FCSTD DOCUMENT  (FreeCAD 0.20R29410 (Git))
Label: PalasFidasFrogExample
License: All rights reserved
LicenseURL: https://en.wikipedia.org/wiki/All_rights_reserved
objects: Part::Feature×547, Part::Box×220, App::Part×142, Part::MultiFuse×119, Part::Cylinder×25, Part::Cut×22, Part::Extrusion×18, Sketcher::SketchObject×17, Part::Fillet×14, Part::FeaturePython×10, Part::Cone×5, Part::Torus×2, Part::Sphere×1, Mesh::Feature×1, Part::Compound×1
note: 1001 computed .brp shape members not serialized (recipe doc carries the construction recipe); baked Part::Feature solids carry a one-line shape summary decoded from their .brp

FEATURE [Sketcher::SketchObject] Sketch
  FullyConstrained = false
  Placement = pos=(0,0,0) rot=(0.57735,-0.57735,-0.57735;2.0944rad)
  sketch-geometry (10):
    g0: LineSegment StartX=-76.5603 StartY=-55.0385 StartZ=0 EndX=-76.5603 EndY=38.9615 EndZ=0
    g1: LineSegment StartX=-76.5603 StartY=-55.0385 StartZ=0 EndX=77.4397 EndY=-55.0385 EndZ=0
    g2: LineSegment StartX=77.4397 StartY=-55.0385 StartZ=0 EndX=77.4397 EndY=1.96148 EndZ=0
    g3: LineSegment StartX=77.4397 StartY=1.96148 StartZ=0 EndX=63.0634 EndY=6.2419 EndZ=0
    g4: LineSegment StartX=63.0634 StartY=6.2419 StartZ=0 EndX=61.4939 EndY=0.970589 EndZ=0
    g5: LineSegment StartX=61.4939 StartY=0.970589 StartZ=0 EndX=48.076 EndY=4.96564 EndZ=0
    g6: LineSegment StartX=48.076 StartY=4.96564 StartZ=0 EndX=40.4859 EndY=2.43786 EndZ=0
    g7: LineSegment StartX=-50.564 StartY=29.5472 StartZ=0 EndX=40.4859 EndY=2.43786 EndZ=0
    g8: LineSegment StartX=-76.5603 StartY=38.9615 StartZ=0 EndX=-58.1062 EndY=33.467 EndZ=0
    g9: LineSegment StartX=-58.1062 StartY=33.467 StartZ=0 EndX=-50.564 EndY=29.5472 EndZ=0
  constraints (27):
    c: Vertical(g0)
    c: Coincident(g1,g0)
    c: Horizontal(g1)
    c: Coincident(g2,g1)
    c: Vertical(g2)
    c: DistanceY(g0,g0) = 94
    c: DistanceX(g1,g1) = 154
    c: DistanceY(g2,g2) = 57
    c: Coincident(g3,g2)
    c: Coincident(g4,g3)
    c: Coincident(g5,g4)
    c: Coincident(g7,g6)
    c: Distance(g4) = 5.5
    c: Distance(g5) = 14
    c: Distance(g3) = 15
    c: Parallel(g7,g3)
    c: Angle(g4,g3) = 1.5708
    c: Parallel(g7,g5)
    c: Distance(g6) = 8
    c: Coincident(g6,g5)
    c: Distance(g7) = 95
    c: Angle(g6,g5) = 2.53073
    c: Coincident(g8,g0)
    c: Coincident(g9,g8)
    c: Coincident(g9,g7)
    c: Parallel(g8,g7)
    c: Distance(g9) = 8.5
FEATURE [Part::Extrusion] Extrude001
  Base = -> Sketch
  Dir = (-1,0,0)
  DirMode = 2
  FaceMakerClass = Part::FaceMakerBullseye
  LengthFwd = 235
  LengthRev = 0
  Placement = pos=(210,0,50) rot=(0,0,1;0rad)
  Solid = true
  Symmetric = false
FEATURE [Part::Extrusion] Extrude
  Base = -> Sketch
  Dir = (-1,0,0)
  DirMode = 2
  FaceMakerClass = Part::FaceMakerBullseye
  LengthFwd = 235
  LengthRev = 0
  Solid = true
  Symmetric = false
FEATURE [Part::Cut] Cut
  Base = -> Extrude
  Tool = -> Extrude001
FEATURE [Part::Cone] Cone
  Angle = 360
  AttacherType = Attacher::AttachEngine3D
  Height = 27
  Placement = pos=(-20,6.5,21) rot=(1,0,0;3.14159rad)
  Radius1 = 0
  Radius2 = 20
FEATURE [Part::Cut] Cut001
  Base = -> Cut
  Tool = -> Cone
FEATURE [Part::Cylinder] Cylinder
  Angle = 360
  AttacherType = Attacher::AttachEngine3D
  FirstAngle = 0
  Height = 2
  Placement = pos=(-20,6.5,-3) rot=(0,0,1;0rad)
  Radius = 10
  SecondAngle = 0
FEATURE [Part::Cylinder] Cylinder001
  Angle = 360
  AttacherType = Attacher::AttachEngine3D
  FirstAngle = 0
  Height = 2
  Placement = pos=(-20,6.5,-5) rot=(0,0,1;0rad)
  Radius = 19.5
  SecondAngle = 0
FEATURE [Part::FeaturePython] Tube  # WARN: FeaturePython — macro-defined, semantics opaque (R4)
  AttacherType = Attacher::AttachEngine3D
  Height = 85
  InnerRadius = 2.5
  OuterRadius = 5
  Placement = pos=(-20,6.5,-3) rot=(0,0,1;0rad)
FEATURE [Sketcher::SketchObject] Sketch001
  FullyConstrained = false
  Placement = pos=(0,0,0) rot=(0.57735,0.57735,0.57735;2.0944rad)
  sketch-geometry (4):
    g0: LineSegment StartX=-44.8885 StartY=-56.9571 StartZ=0 EndX=-44.8885 EndY=-44.9571 EndZ=0
    g1: LineSegment StartX=-44.8885 StartY=-56.9571 StartZ=0 EndX=-26.8885 EndY=-56.9571 EndZ=0
    g2: LineSegment StartX=-26.8885 StartY=-56.9571 StartZ=0 EndX=-26.8885 EndY=-44.9571 EndZ=0
    g3: ArcOfCircle CenterX=-35.8885 CenterY=-44.9571 CenterZ=0 NormalX=0 NormalY=0 NormalZ=1 AngleXU=0 Radius=9 StartAngle=0 EndAngle=3.14159
  constraints (11):
    c: Vertical(g0)
    c: Coincident(g1,g0)
    c: Horizontal(g1)
    c: Coincident(g2,g1)
    c: Vertical(g2)
    c: DistanceY(g0,g0) = 12
    c: DistanceY(g2,g2) = 12
    c: Coincident(g3,g0)
    c: Coincident(g3,g2)
    c: DistanceX(g1,g1) = 18
    c: Angle(g3) = 3.14159
FEATURE [Part::Extrusion] Extrude002  label="inlet"
  Base = -> Sketch001
  Dir = (1,-2e-16,2e-16)
  DirMode = 2
  FaceMakerClass = Part::FaceMakerBullseye
  LengthFwd = 15
  LengthRev = 0
  Placement = pos=(-15,18.5,0) rot=(0,0,1;0rad)
  Solid = true
  Symmetric = false
FEATURE [Part::MultiFuse] Fusion  label="Palas_base"
  Shapes = -> [Cut001,Cylinder,Cylinder001,Tube]
FEATURE [Part::Cut] Cut002
  Base = -> Fusion
  Tool = -> Extrude002
FEATURE [Part::Cylinder] Cylinder002
  Angle = 360
  AttacherType = Attacher::AttachEngine3D
  FirstAngle = 0
  Height = 5
  Placement = pos=(-20,-17.4,-45) rot=(0,1,0;1.5708rad)
  Radius = 9
  SecondAngle = 0
FEATURE [Part::Cut] Cut003  label="Palas_002"
  Base = -> Cut002
  Tool = -> Cylinder002
FEATURE [Part::Cylinder] Cylinder003
  Angle = 360
  AttacherType = Attacher::AttachEngine3D
  FirstAngle = 0
  Height = 15
  Placement = pos=(-35,-17.4,-45) rot=(0,1,0;1.5708rad)
  Radius = 6.5
  SecondAngle = 0
FEATURE [Part::Cut] Cut004
  Base = -> Cut003
  Tool = -> Cylinder003
FEATURE [Part::Feature] Part__Feature  label="USB_Mini_B_SMD_buchse"
  Placement = pos=(1,-56.5,-46.5) rot=(0.57735,0.57735,0.57735;2.0944rad)
  shape: bbox 8.901 x 10 x 3.979 mm, 476 faces (baked)
FEATURE [Part::Box] Box  label="Cube"
  AttacherType = Attacher::AttachEngine3D
  Height = 57
  Length = 5.5
  Placement = pos=(-5,46,-56) rot=(0,0,1;0rad)
  Width = 31.5
FEATURE [Part::MultiFuse] Fusion001  label="Palas003"
  Shapes = -> [Cut004,Part__Feature]
FEATURE [Part::Cut] Cut005  label="Palas"
  Base = -> Fusion001
  Tool = -> Box
FEATURE [Part::Feature] Part__Feature001  label="corps"
  shape: bbox 34 x 13.5 x 21 mm, 889 faces (baked)
FEATURE [Part::Feature] Part__Feature002  label="pin"
  Placement = pos=(-10.5,0,-19) rot=(0,0,1;0rad)
  shape: bbox 0.75 x 9 x 9.5 mm, 29 faces (baked)
FEATURE [Part::Feature] Part__Feature003  label="pin001"
  Placement = pos=(0,0,-19) rot=(0,0,1;0rad)
  shape: bbox 0.75 x 9 x 9.5 mm, 29 faces (baked)
FEATURE [Part::Feature] Part__Feature004  label="pin002"
  Placement = pos=(10.5,0,-19) rot=(0,0,1;0rad)
  shape: bbox 0.75 x 9 x 9.5 mm, 29 faces (baked)
FEATURE [App::Part] Array
  Group = -> [Part__Feature002,Part__Feature003,Part__Feature004]
  Origin = -> Origin001
FEATURE [Part::Feature] Part__Feature005  label="bouton001"
  shape: bbox 22.78 x 10.2 x 12.36 mm, 22 faces (baked)
FEATURE [App::Part] QY603_inter
  Group = -> [Part__Feature001,Array,Part__Feature005]
  Origin = -> Origin002
  Placement = pos=(-6,53,-37) rot=(-0.707107,0,-0.707107;3.14159rad)
FEATURE [Part::Feature] Part__Feature006  label="238-206706"
  shape: bbox 22.46 x 17.88 x 12.7 mm, 94 faces, 0 solids (baked)
FEATURE [Part::Feature] Part__Feature007  label="238-206707"
  shape: bbox 8.001 x 5.836 x 8.001 mm, 28 faces, 0 solids (baked)
FEATURE [Part::Feature] Part__Feature008  label="238-206708"
  shape: bbox 8 x 1.779 x 8 mm, 2 faces, 0 solids (baked)
FEATURE [Part::Feature] Part__Feature009  label="238-206709"
  shape: bbox 2e+100 x 2e+100 x 2e+100 mm, 1 faces, 0 solids (baked)
FEATURE [Part::Feature] Part__Feature010  label="238-206710"
  shape: bbox 8 x 6.139 x 8 mm, 1 faces, 0 solids (baked)
FEATURE [Part::Feature] Part__Feature011  label="238-206711"
  shape: bbox 8 x 1.922 x 8 mm, 1 faces, 0 solids (baked)
FEATURE [Part::Feature] Part__Feature012  label="238-206712"
  shape: bbox 8 x 0.418 x 8 mm, 1 faces, 0 solids (baked)
FEATURE [Part::Feature] Part__Feature013  label="238-206713"
  shape: bbox 0.1933 x 2 x 0.7938 mm, 6 faces, 0 solids (baked)
FEATURE [Part::Feature] Part__Feature014  label="238-206714"
  shape: bbox 0.5393 x 2 x 0.8141 mm, 12 faces, 0 solids (baked)
FEATURE [Part::Feature] Part__Feature015  label="238-206715"
  shape: bbox 0.5393 x 2 x 0.8345 mm, 17 faces, 0 solids (baked)
FEATURE [App::Part] _38_206706  label="dc"
  Group = -> [Part__Feature006,Part__Feature007,Part__Feature008,Part__Feature009,Part__Feature010,Part__Feature011,Part__Feature012,Part__Feature013,Part__Feature014,Part__Feature015]
  Origin = -> Origin003
  Placement = pos=(-7.5,67,-39) rot=(-0.57735,0.57735,-0.57735;4.18879rad)
FEATURE [Part::Box] Box001  label="Cube001"
  AttacherType = Attacher::AttachEngine3D
  Height = 1
  Length = 10
  Placement = pos=(-235,50,-14) rot=(0,0,1;0rad)
  Width = 14
FEATURE [Part::Box] Box002  label="Cube002"
  AttacherType = Attacher::AttachEngine3D
  Height = 1
  Length = 10
  Placement = pos=(-235,35,-14) rot=(0,0,1;0rad)
  Width = 14
FEATURE [Part::Box] Box003  label="Cube003"
  AttacherType = Attacher::AttachEngine3D
  Height = 1
  Length = 10
  Placement = pos=(-235,20,-14) rot=(0,0,1;0rad)
  Width = 14
FEATURE [Part::MultiFuse] Fusion002
  Shapes = -> [Box001,Box002,Box003]
FEATURE [Part::Box] Box004  label="Cube004"
  AttacherType = Attacher::AttachEngine3D
  Height = 1
  Length = 10
  Placement = pos=(-235,50,-14) rot=(0,0,1;0rad)
  Width = 14
FEATURE [Part::Box] Box005  label="Cube005"
  AttacherType = Attacher::AttachEngine3D
  Height = 1
  Length = 10
  Placement = pos=(-235,35,-14) rot=(0,0,1;0rad)
  Width = 14
FEATURE [Part::Box] Box006  label="Cube006"
  AttacherType = Attacher::AttachEngine3D
  Height = 1
  Length = 10
  Placement = pos=(-235,20,-14) rot=(0,0,1;0rad)
  Width = 14
FEATURE [Part::MultiFuse] Fusion003
  Placement = pos=(0,0,-2) rot=(0,0,1;0rad)
  Shapes = -> [Box004,Box005,Box006]
FEATURE [Part::Box] Box007  label="Cube007"
  AttacherType = Attacher::AttachEngine3D
  Height = 1
  Length = 10
  Placement = pos=(-235,50,-14) rot=(0,0,1;0rad)
  Width = 14
FEATURE [Part::Box] Box008  label="Cube008"
  AttacherType = Attacher::AttachEngine3D
  Height = 1
  Length = 10
  Placement = pos=(-235,35,-14) rot=(0,0,1;0rad)
  Width = 14
FEATURE [Part::Box] Box009  label="Cube009"
  AttacherType = Attacher::AttachEngine3D
  Height = 1
  Length = 10
  Placement = pos=(-235,20,-14) rot=(0,0,1;0rad)
  Width = 14
FEATURE [Part::MultiFuse] Fusion004
  Placement = pos=(0,0,-4) rot=(0,0,1;0rad)
  Shapes = -> [Box007,Box008,Box009]
FEATURE [Part::Box] Box010  label="Cube010"
  AttacherType = Attacher::AttachEngine3D
  Height = 1
  Length = 10
  Placement = pos=(-235,50,-14) rot=(0,0,1;0rad)
  Width = 14
FEATURE [Part::Box] Box011  label="Cube011"
  AttacherType = Attacher::AttachEngine3D
  Height = 1
  Length = 10
  Placement = pos=(-235,35,-14) rot=(0,0,1;0rad)
  Width = 14
FEATURE [Part::Box] Box012  label="Cube012"
  AttacherType = Attacher::AttachEngine3D
  Height = 1
  Length = 10
  Placement = pos=(-235,20,-14) rot=(0,0,1;0rad)
  Width = 14
FEATURE [Part::MultiFuse] Fusion005
  Placement = pos=(0,0,-6) rot=(0,0,1;0rad)
  Shapes = -> [Box010,Box011,Box012]
FEATURE [Part::Box] Box013  label="Cube013"
  AttacherType = Attacher::AttachEngine3D
  Height = 1
  Length = 10
  Placement = pos=(-235,50,-14) rot=(0,0,1;0rad)
  Width = 14
FEATURE [Part::Box] Box014  label="Cube014"
  AttacherType = Attacher::AttachEngine3D
  Height = 1
  Length = 10
  Placement = pos=(-235,35,-14) rot=(0,0,1;0rad)
  Width = 14
FEATURE [Part::Box] Box015  label="Cube015"
  AttacherType = Attacher::AttachEngine3D
  Height = 1
  Length = 10
  Placement = pos=(-235,20,-14) rot=(0,0,1;0rad)
  Width = 14
FEATURE [Part::MultiFuse] Fusion006
  Placement = pos=(0,0,-8) rot=(0,0,1;0rad)
  Shapes = -> [Box013,Box014,Box015]
FEATURE [Part::Box] Box016  label="Cube016"
  AttacherType = Attacher::AttachEngine3D
  Height = 1
  Length = 10
  Placement = pos=(-235,50,-14) rot=(0,0,1;0rad)
  Width = 14
FEATURE [Part::Box] Box017  label="Cube017"
  AttacherType = Attacher::AttachEngine3D
  Height = 1
  Length = 10
  Placement = pos=(-235,35,-14) rot=(0,0,1;0rad)
  Width = 14
FEATURE [Part::Box] Box018  label="Cube018"
  AttacherType = Attacher::AttachEngine3D
  Height = 1
  Length = 10
  Placement = pos=(-235,20,-14) rot=(0,0,1;0rad)
  Width = 14
FEATURE [Part::MultiFuse] Fusion007
  Placement = pos=(0,0,-10) rot=(0,0,1;0rad)
  Shapes = -> [Box016,Box017,Box018]
FEATURE [Part::Box] Box019  label="Cube019"
  AttacherType = Attacher::AttachEngine3D
  Height = 1
  Length = 10
  Placement = pos=(-235,50,-14) rot=(0,0,1;0rad)
  Width = 14
FEATURE [Part::Box] Box020  label="Cube020"
  AttacherType = Attacher::AttachEngine3D
  Height = 1
  Length = 10
  Placement = pos=(-235,35,-14) rot=(0,0,1;0rad)
  Width = 14
FEATURE [Part::Box] Box021  label="Cube021"
  AttacherType = Attacher::AttachEngine3D
  Height = 1
  Length = 10
  Placement = pos=(-235,20,-14) rot=(0,0,1;0rad)
  Width = 14
FEATURE [Part::MultiFuse] Fusion008
  Placement = pos=(0,0,-12) rot=(0,0,1;0rad)
  Shapes = -> [Box019,Box020,Box021]
FEATURE [Part::Box] Box022  label="Cube022"
  AttacherType = Attacher::AttachEngine3D
  Height = 1
  Length = 10
  Placement = pos=(-235,50,-14) rot=(0,0,1;0rad)
  Width = 14
FEATURE [Part::Box] Box023  label="Cube023"
  AttacherType = Attacher::AttachEngine3D
  Height = 1
  Length = 10
  Placement = pos=(-235,35,-14) rot=(0,0,1;0rad)
  Width = 14
FEATURE [Part::Box] Box024  label="Cube024"
  AttacherType = Attacher::AttachEngine3D
  Height = 1
  Length = 10
  Placement = pos=(-235,20,-14) rot=(0,0,1;0rad)
  Width = 14
FEATURE [Part::MultiFuse] Fusion009
  Placement = pos=(0,0,-14) rot=(0,0,1;0rad)
  Shapes = -> [Box022,Box023,Box024]
FEATURE [Part::Box] Box025  label="Cube025"
  AttacherType = Attacher::AttachEngine3D
  Height = 1
  Length = 10
  Placement = pos=(-235,50,-14) rot=(0,0,1;0rad)
  Width = 14
FEATURE [Part::Box] Box026  label="Cube026"
  AttacherType = Attacher::AttachEngine3D
  Height = 1
  Length = 10
  Placement = pos=(-235,35,-14) rot=(0,0,1;0rad)
  Width = 14
FEATURE [Part::Box] Box027  label="Cube027"
  AttacherType = Attacher::AttachEngine3D
  Height = 1
  Length = 10
  Placement = pos=(-235,20,-14) rot=(0,0,1;0rad)
  Width = 14
FEATURE [Part::MultiFuse] Fusion010
  Placement = pos=(0,0,-16) rot=(0,0,1;0rad)
  Shapes = -> [Box025,Box026,Box027]
FEATURE [Part::Box] Box028  label="Cube028"
  AttacherType = Attacher::AttachEngine3D
  Height = 1
  Length = 10
  Placement = pos=(-235,50,-14) rot=(0,0,1;0rad)
  Width = 14
FEATURE [Part::Box] Box029  label="Cube029"
  AttacherType = Attacher::AttachEngine3D
  Height = 1
  Length = 10
  Placement = pos=(-235,35,-14) rot=(0,0,1;0rad)
  Width = 14
FEATURE [Part::Box] Box030  label="Cube030"
  AttacherType = Attacher::AttachEngine3D
  Height = 1
  Length = 10
  Placement = pos=(-235,20,-14) rot=(0,0,1;0rad)
  Width = 14
FEATURE [Part::MultiFuse] Fusion011
  Placement = pos=(0,0,-18) rot=(0,0,1;0rad)
  Shapes = -> [Box028,Box029,Box030]
FEATURE [Part::MultiFuse] Fusion012
  Shapes = -> [Fusion002,Fusion003,Fusion004,Fusion005,Fusion006,Fusion007,Fusion008,Fusion009,Fusion010,Fusion011]
FEATURE [Part::Box] Box031  label="Cube031"
  AttacherType = Attacher::AttachEngine3D
  Height = 1
  Length = 10
  Placement = pos=(-235,50,-14) rot=(0,0,1;0rad)
  Width = 14
FEATURE [Part::Box] Box032  label="Cube032"
  AttacherType = Attacher::AttachEngine3D
  Height = 1
  Length = 10
  Placement = pos=(-235,35,-14) rot=(0,0,1;0rad)
  Width = 14
FEATURE [Part::Box] Box033  label="Cube033"
  AttacherType = Attacher::AttachEngine3D
  Height = 1
  Length = 10
  Placement = pos=(-235,20,-14) rot=(0,0,1;0rad)
  Width = 14
FEATURE [Part::Box] Box034  label="Cube034"
  AttacherType = Attacher::AttachEngine3D
  Height = 1
  Length = 10
  Placement = pos=(-235,50,-14) rot=(0,0,1;0rad)
  Width = 14
FEATURE [Part::Box] Box035  label="Cube035"
  AttacherType = Attacher::AttachEngine3D
  Height = 1
  Length = 10
  Placement = pos=(-235,35,-14) rot=(0,0,1;0rad)
  Width = 14
FEATURE [Part::Box] Box036  label="Cube036"
  AttacherType = Attacher::AttachEngine3D
  Height = 1
  Length = 10
  Placement = pos=(-235,20,-14) rot=(0,0,1;0rad)
  Width = 14
FEATURE [Part::Box] Box037  label="Cube037"
  AttacherType = Attacher::AttachEngine3D
  Height = 1
  Length = 10
  Placement = pos=(-235,50,-14) rot=(0,0,1;0rad)
  Width = 14
FEATURE [Part::Box] Box038  label="Cube038"
  AttacherType = Attacher::AttachEngine3D
  Height = 1
  Length = 10
  Placement = pos=(-235,35,-14) rot=(0,0,1;0rad)
  Width = 14
FEATURE [Part::Box] Box039  label="Cube039"
  AttacherType = Attacher::AttachEngine3D
  Height = 1
  Length = 10
  Placement = pos=(-235,20,-14) rot=(0,0,1;0rad)
  Width = 14
FEATURE [Part::Box] Box040  label="Cube040"
  AttacherType = Attacher::AttachEngine3D
  Height = 1
  Length = 10
  Placement = pos=(-235,50,-14) rot=(0,0,1;0rad)
  Width = 14
FEATURE [Part::Box] Box041  label="Cube041"
  AttacherType = Attacher::AttachEngine3D
  Height = 1
  Length = 10
  Placement = pos=(-235,35,-14) rot=(0,0,1;0rad)
  Width = 14
FEATURE [Part::Box] Box042  label="Cube042"
  AttacherType = Attacher::AttachEngine3D
  Height = 1
  Length = 10
  Placement = pos=(-235,20,-14) rot=(0,0,1;0rad)
  Width = 14
FEATURE [Part::Box] Box043  label="Cube043"
  AttacherType = Attacher::AttachEngine3D
  Height = 1
  Length = 10
  Placement = pos=(-235,50,-14) rot=(0,0,1;0rad)
  Width = 14
FEATURE [Part::Box] Box044  label="Cube044"
  AttacherType = Attacher::AttachEngine3D
  Height = 1
  Length = 10
  Placement = pos=(-235,35,-14) rot=(0,0,1;0rad)
  Width = 14
FEATURE [Part::Box] Box045  label="Cube045"
  AttacherType = Attacher::AttachEngine3D
  Height = 1
  Length = 10
  Placement = pos=(-235,20,-14) rot=(0,0,1;0rad)
  Width = 14
FEATURE [Part::Box] Box046  label="Cube046"
  AttacherType = Attacher::AttachEngine3D
  Height = 1
  Length = 10
  Placement = pos=(-235,50,-14) rot=(0,0,1;0rad)
  Width = 14
FEATURE [Part::Box] Box047  label="Cube047"
  AttacherType = Attacher::AttachEngine3D
  Height = 1
  Length = 10
  Placement = pos=(-235,35,-14) rot=(0,0,1;0rad)
  Width = 14
FEATURE [Part::Box] Box048  label="Cube048"
  AttacherType = Attacher::AttachEngine3D
  Height = 1
  Length = 10
  Placement = pos=(-235,20,-14) rot=(0,0,1;0rad)
  Width = 14
FEATURE [Part::Box] Box049  label="Cube049"
  AttacherType = Attacher::AttachEngine3D
  Height = 1
  Length = 10
  Placement = pos=(-235,50,-14) rot=(0,0,1;0rad)
  Width = 14
FEATURE [Part::Box] Box050  label="Cube050"
  AttacherType = Attacher::AttachEngine3D
  Height = 1
  Length = 10
  Placement = pos=(-235,35,-14) rot=(0,0,1;0rad)
  Width = 14
FEATURE [Part::Box] Box051  label="Cube051"
  AttacherType = Attacher::AttachEngine3D
  Height = 1
  Length = 10
  Placement = pos=(-235,20,-14) rot=(0,0,1;0rad)
  Width = 14
FEATURE [Part::Box] Box052  label="Cube052"
  AttacherType = Attacher::AttachEngine3D
  Height = 1
  Length = 10
  Placement = pos=(-235,50,-14) rot=(0,0,1;0rad)
  Width = 14
FEATURE [Part::Box] Box053  label="Cube053"
  AttacherType = Attacher::AttachEngine3D
  Height = 1
  Length = 10
  Placement = pos=(-235,35,-14) rot=(0,0,1;0rad)
  Width = 14
FEATURE [Part::Box] Box054  label="Cube054"
  AttacherType = Attacher::AttachEngine3D
  Height = 1
  Length = 10
  Placement = pos=(-235,20,-14) rot=(0,0,1;0rad)
  Width = 14
FEATURE [Part::Box] Box055  label="Cube055"
  AttacherType = Attacher::AttachEngine3D
  Height = 1
  Length = 10
  Placement = pos=(-235,50,-14) rot=(0,0,1;0rad)
  Width = 14
FEATURE [Part::Box] Box056  label="Cube056"
  AttacherType = Attacher::AttachEngine3D
  Height = 1
  Length = 10
  Placement = pos=(-235,35,-14) rot=(0,0,1;0rad)
  Width = 14
FEATURE [Part::Box] Box057  label="Cube057"
  AttacherType = Attacher::AttachEngine3D
  Height = 1
  Length = 10
  Placement = pos=(-235,20,-14) rot=(0,0,1;0rad)
  Width = 14
FEATURE [Part::Box] Box058  label="Cube058"
  AttacherType = Attacher::AttachEngine3D
  Height = 1
  Length = 10
  Placement = pos=(-235,50,-14) rot=(0,0,1;0rad)
  Width = 14
FEATURE [Part::Box] Box059  label="Cube059"
  AttacherType = Attacher::AttachEngine3D
  Height = 1
  Length = 10
  Placement = pos=(-235,35,-14) rot=(0,0,1;0rad)
  Width = 14
FEATURE [Part::Box] Box060  label="Cube060"
  AttacherType = Attacher::AttachEngine3D
  Height = 1
  Length = 10
  Placement = pos=(-235,20,-14) rot=(0,0,1;0rad)
  Width = 14
FEATURE [Part::MultiFuse] Fusion013
  Shapes = -> [Box031,Box032,Box033]
FEATURE [Part::MultiFuse] Fusion014
  Placement = pos=(0,0,-2) rot=(0,0,1;0rad)
  Shapes = -> [Box034,Box035,Box036]
FEATURE [Part::MultiFuse] Fusion015
  Placement = pos=(0,0,-4) rot=(0,0,1;0rad)
  Shapes = -> [Box037,Box038,Box039]
FEATURE [Part::MultiFuse] Fusion016
  Placement = pos=(0,0,-6) rot=(0,0,1;0rad)
  Shapes = -> [Box040,Box041,Box042]
FEATURE [Part::MultiFuse] Fusion017
  Placement = pos=(0,0,-8) rot=(0,0,1;0rad)
  Shapes = -> [Box043,Box044,Box045]
FEATURE [Part::MultiFuse] Fusion018
  Placement = pos=(0,0,-10) rot=(0,0,1;0rad)
  Shapes = -> [Box046,Box047,Box048]
FEATURE [Part::MultiFuse] Fusion019
  Placement = pos=(0,0,-12) rot=(0,0,1;0rad)
  Shapes = -> [Box049,Box050,Box051]
FEATURE [Part::MultiFuse] Fusion020
  Placement = pos=(0,0,-14) rot=(0,0,1;0rad)
  Shapes = -> [Box052,Box053,Box054]
FEATURE [Part::MultiFuse] Fusion021
  Placement = pos=(0,0,-16) rot=(0,0,1;0rad)
  Shapes = -> [Box055,Box056,Box057]
FEATURE [Part::MultiFuse] Fusion022
  Placement = pos=(0,0,-18) rot=(0,0,1;0rad)
  Shapes = -> [Box058,Box059,Box060]
FEATURE [Part::MultiFuse] Fusion023
  Placement = pos=(0,0,-20) rot=(0,0,1;0rad)
  Shapes = -> [Fusion013,Fusion014,Fusion015,Fusion016,Fusion017,Fusion018,Fusion019,Fusion020,Fusion021,Fusion022]
FEATURE [Part::MultiFuse] Fusion024
  Shapes = -> [Fusion012,Fusion023]
FEATURE [Part::Cut] Cut006
  Base = -> Cut005
  Tool = -> Fusion024
FEATURE [Part::Box] Box062  label="Cube062"
  AttacherType = Attacher::AttachEngine3D
  Height = 1
  Length = 10
  Placement = pos=(-235,35,-14) rot=(0,0,1;0rad)
  Width = 14
FEATURE [Part::Box] Box065  label="Cube065"
  AttacherType = Attacher::AttachEngine3D
  Height = 1
  Length = 10
  Placement = pos=(-235,35,-14) rot=(0,0,1;0rad)
  Width = 14
FEATURE [Part::Box] Box066  label="Cube066"
  AttacherType = Attacher::AttachEngine3D
  Height = 1
  Length = 10
  Placement = pos=(-235,20,-14) rot=(0,0,1;0rad)
  Width = 14
FEATURE [Part::Box] Box068  label="Cube068"
  AttacherType = Attacher::AttachEngine3D
  Height = 1
  Length = 10
  Placement = pos=(-235,35,-14) rot=(0,0,1;0rad)
  Width = 14
FEATURE [Part::Box] Box069  label="Cube069"
  AttacherType = Attacher::AttachEngine3D
  Height = 1
  Length = 10
  Placement = pos=(-235,20,-14) rot=(0,0,1;0rad)
  Width = 14
FEATURE [Part::Box] Box071  label="Cube071"
  AttacherType = Attacher::AttachEngine3D
  Height = 1
  Length = 10
  Placement = pos=(-235,35,-14) rot=(0,0,1;0rad)
  Width = 14
FEATURE [Part::Box] Box072  label="Cube072"
  AttacherType = Attacher::AttachEngine3D
  Height = 1
  Length = 10
  Placement = pos=(-235,20,-14) rot=(0,0,1;0rad)
  Width = 14
FEATURE [Part::Box] Box074  label="Cube074"
  AttacherType = Attacher::AttachEngine3D
  Height = 1
  Length = 10
  Placement = pos=(-235,35,-14) rot=(0,0,1;0rad)
  Width = 14
FEATURE [Part::Box] Box075  label="Cube075"
  AttacherType = Attacher::AttachEngine3D
  Height = 1
  Length = 10
  Placement = pos=(-235,20,-14) rot=(0,0,1;0rad)
  Width = 14
FEATURE [Part::Box] Box077  label="Cube077"
  AttacherType = Attacher::AttachEngine3D
  Height = 1
  Length = 10
  Placement = pos=(-235,35,-14) rot=(0,0,1;0rad)
  Width = 14
FEATURE [Part::Box] Box078  label="Cube078"
  AttacherType = Attacher::AttachEngine3D
  Height = 1
  Length = 10
  Placement = pos=(-235,20,-14) rot=(0,0,1;0rad)
  Width = 14
FEATURE [Part::Box] Box080  label="Cube080"
  AttacherType = Attacher::AttachEngine3D
  Height = 1
  Length = 10
  Placement = pos=(-235,35,-14) rot=(0,0,1;0rad)
  Width = 14
FEATURE [Part::Box] Box081  label="Cube081"
  AttacherType = Attacher::AttachEngine3D
  Height = 1
  Length = 10
  Placement = pos=(-235,20,-14) rot=(0,0,1;0rad)
  Width = 14
FEATURE [Part::Box] Box083  label="Cube083"
  AttacherType = Attacher::AttachEngine3D
  Height = 1
  Length = 10
  Placement = pos=(-235,35,-14) rot=(0,0,1;0rad)
  Width = 14
FEATURE [Part::Box] Box084  label="Cube084"
  AttacherType = Attacher::AttachEngine3D
  Height = 1
  Length = 10
  Placement = pos=(-235,20,-14) rot=(0,0,1;0rad)
  Width = 14
FEATURE [Part::Box] Box086  label="Cube086"
  AttacherType = Attacher::AttachEngine3D
  Height = 1
  Length = 10
  Placement = pos=(-235,35,-14) rot=(0,0,1;0rad)
  Width = 14
FEATURE [Part::Box] Box087  label="Cube087"
  AttacherType = Attacher::AttachEngine3D
  Height = 1
  Length = 10
  Placement = pos=(-235,20,-14) rot=(0,0,1;0rad)
  Width = 14
FEATURE [Part::Box] Box089  label="Cube089"
  AttacherType = Attacher::AttachEngine3D
  Height = 1
  Length = 10
  Placement = pos=(-235,35,-14) rot=(0,0,1;0rad)
  Width = 14
FEATURE [Part::Box] Box090  label="Cube090"
  AttacherType = Attacher::AttachEngine3D
  Height = 1
  Length = 10
  Placement = pos=(-235,20,-14) rot=(0,0,1;0rad)
  Width = 14
FEATURE [Part::Box] Box092  label="Cube092"
  AttacherType = Attacher::AttachEngine3D
  Height = 1
  Length = 10
  Placement = pos=(-235,35,-14) rot=(0,0,1;0rad)
  Width = 14
FEATURE [Part::Box] Box093  label="Cube093"
  AttacherType = Attacher::AttachEngine3D
  Height = 1
  Length = 10
  Placement = pos=(-235,20,-14) rot=(0,0,1;0rad)
  Width = 14
FEATURE [Part::Box] Box095  label="Cube095"
  AttacherType = Attacher::AttachEngine3D
  Height = 1
  Length = 10
  Placement = pos=(-235,35,-14) rot=(0,0,1;0rad)
  Width = 14
FEATURE [Part::Box] Box096  label="Cube096"
  AttacherType = Attacher::AttachEngine3D
  Height = 1
  Length = 10
  Placement = pos=(-235,20,-14) rot=(0,0,1;0rad)
  Width = 14
FEATURE [Part::Box] Box098  label="Cube098"
  AttacherType = Attacher::AttachEngine3D
  Height = 1
  Length = 10
  Placement = pos=(-235,35,-14) rot=(0,0,1;0rad)
  Width = 14
FEATURE [Part::Box] Box099  label="Cube099"
  AttacherType = Attacher::AttachEngine3D
  Height = 1
  Length = 10
  Placement = pos=(-235,20,-14) rot=(0,0,1;0rad)
  Width = 14
FEATURE [Part::Box] Box101  label="Cube101"
  AttacherType = Attacher::AttachEngine3D
  Height = 1
  Length = 10
  Placement = pos=(-235,35,-14) rot=(0,0,1;0rad)
  Width = 14
FEATURE [Part::Box] Box102  label="Cube102"
  AttacherType = Attacher::AttachEngine3D
  Height = 1
  Length = 10
  Placement = pos=(-235,20,-14) rot=(0,0,1;0rad)
  Width = 14
FEATURE [Part::Box] Box104  label="Cube104"
  AttacherType = Attacher::AttachEngine3D
  Height = 1
  Length = 10
  Placement = pos=(-235,35,-14) rot=(0,0,1;0rad)
  Width = 14
FEATURE [Part::Box] Box105  label="Cube105"
  AttacherType = Attacher::AttachEngine3D
  Height = 1
  Length = 10
  Placement = pos=(-235,20,-14) rot=(0,0,1;0rad)
  Width = 14
FEATURE [Part::Box] Box107  label="Cube107"
  AttacherType = Attacher::AttachEngine3D
  Height = 1
  Length = 10
  Placement = pos=(-235,35,-14) rot=(0,0,1;0rad)
  Width = 14
FEATURE [Part::Box] Box108  label="Cube108"
  AttacherType = Attacher::AttachEngine3D
  Height = 1
  Length = 10
  Placement = pos=(-235,20,-14) rot=(0,0,1;0rad)
  Width = 14
FEATURE [Part::Box] Box110  label="Cube110"
  AttacherType = Attacher::AttachEngine3D
  Height = 1
  Length = 10
  Placement = pos=(-235,35,-14) rot=(0,0,1;0rad)
  Width = 14
FEATURE [Part::Box] Box111  label="Cube111"
  AttacherType = Attacher::AttachEngine3D
  Height = 1
  Length = 10
  Placement = pos=(-235,20,-14) rot=(0,0,1;0rad)
  Width = 14
FEATURE [Part::Box] Box113  label="Cube113"
  AttacherType = Attacher::AttachEngine3D
  Height = 1
  Length = 10
  Placement = pos=(-235,35,-14) rot=(0,0,1;0rad)
  Width = 14
FEATURE [Part::Box] Box114  label="Cube114"
  AttacherType = Attacher::AttachEngine3D
  Height = 1
  Length = 10
  Placement = pos=(-235,20,-14) rot=(0,0,1;0rad)
  Width = 14
FEATURE [Part::Box] Box116  label="Cube116"
  AttacherType = Attacher::AttachEngine3D
  Height = 1
  Length = 10
  Placement = pos=(-235,35,-14) rot=(0,0,1;0rad)
  Width = 14
FEATURE [Part::Box] Box117  label="Cube117"
  AttacherType = Attacher::AttachEngine3D
  Height = 1
  Length = 10
  Placement = pos=(-235,20,-14) rot=(0,0,1;0rad)
  Width = 14
FEATURE [Part::Box] Box119  label="Cube119"
  AttacherType = Attacher::AttachEngine3D
  Height = 1
  Length = 10
  Placement = pos=(-235,35,-14) rot=(0,0,1;0rad)
  Width = 14
FEATURE [Part::Box] Box120  label="Cube120"
  AttacherType = Attacher::AttachEngine3D
  Height = 1
  Length = 10
  Placement = pos=(-235,20,-14) rot=(0,0,1;0rad)
  Width = 14
FEATURE [Part::MultiFuse] Fusion026
  Placement = pos=(0,0,-2) rot=(0,0,1;0rad)
  Shapes = -> [Box065,Box066]
FEATURE [Part::MultiFuse] Fusion027
  Placement = pos=(0,0,-4) rot=(0,0,1;0rad)
  Shapes = -> [Box068,Box069]
FEATURE [Part::MultiFuse] Fusion028
  Placement = pos=(0,0,-6) rot=(0,0,1;0rad)
  Shapes = -> [Box071,Box072]
FEATURE [Part::MultiFuse] Fusion029
  Placement = pos=(0,0,-8) rot=(0,0,1;0rad)
  Shapes = -> [Box074,Box075]
FEATURE [Part::MultiFuse] Fusion030
  Placement = pos=(0,0,-10) rot=(0,0,1;0rad)
  Shapes = -> [Box077,Box078]
FEATURE [Part::MultiFuse] Fusion031
  Placement = pos=(0,0,-12) rot=(0,0,1;0rad)
  Shapes = -> [Box080,Box081]
FEATURE [Part::MultiFuse] Fusion032
  Placement = pos=(0,0,-14) rot=(0,0,1;0rad)
  Shapes = -> [Box083,Box084]
FEATURE [Part::MultiFuse] Fusion033
  Placement = pos=(0,0,-16) rot=(0,0,1;0rad)
  Shapes = -> [Box086,Box087]
FEATURE [Part::MultiFuse] Fusion034
  Placement = pos=(0,0,-18) rot=(0,0,1;0rad)
  Shapes = -> [Box089,Box090]
FEATURE [Part::MultiFuse] Fusion036
  Shapes = -> [Box092,Box093]
FEATURE [Part::MultiFuse] Fusion037
  Placement = pos=(0,0,-2) rot=(0,0,1;0rad)
  Shapes = -> [Box095,Box096]
FEATURE [Part::MultiFuse] Fusion038
  Placement = pos=(0,0,-4) rot=(0,0,1;0rad)
  Shapes = -> [Box098,Box099]
FEATURE [Part::MultiFuse] Fusion039
  Placement = pos=(0,0,-6) rot=(0,0,1;0rad)
  Shapes = -> [Box101,Box102]
FEATURE [Part::MultiFuse] Fusion040
  Placement = pos=(0,0,-8) rot=(0,0,1;0rad)
  Shapes = -> [Box104,Box105]
FEATURE [Part::MultiFuse] Fusion041
  Placement = pos=(0,0,-10) rot=(0,0,1;0rad)
  Shapes = -> [Box107,Box108]
FEATURE [Part::MultiFuse] Fusion042
  Placement = pos=(0,0,-12) rot=(0,0,1;0rad)
  Shapes = -> [Box110,Box111]
FEATURE [Part::MultiFuse] Fusion043
  Placement = pos=(0,0,-14) rot=(0,0,1;0rad)
  Shapes = -> [Box113,Box114]
FEATURE [Part::MultiFuse] Fusion044
  Placement = pos=(0,0,-16) rot=(0,0,1;0rad)
  Shapes = -> [Box116,Box117]
FEATURE [Part::MultiFuse] Fusion045
  Placement = pos=(0,0,-18) rot=(0,0,1;0rad)
  Shapes = -> [Box119,Box120]
FEATURE [Part::MultiFuse] Fusion046
  Placement = pos=(0,0,-20) rot=(0,0,1;0rad)
  Shapes = -> [Fusion036,Fusion037,Fusion038,Fusion039,Fusion040,Fusion041,Fusion042,Fusion043,Fusion044,Fusion045]
FEATURE [Part::Box] Box063  label="Cube063"
  AttacherType = Attacher::AttachEngine3D
  Height = 1
  Length = 10
  Placement = pos=(-235,20,-14) rot=(0,0,1;0rad)
  Width = 14
FEATURE [Part::MultiFuse] Fusion025
  Shapes = -> [Box062,Box063]
FEATURE [Part::MultiFuse] Fusion035
  Shapes = -> [Fusion025,Fusion026,Fusion027,Fusion028,Fusion029,Fusion030,Fusion031,Fusion032,Fusion033,Fusion034]
FEATURE [Part::MultiFuse] Fusion047
  Placement = pos=(-253,-157,0) rot=(0,0,-1;1.5708rad)
  Shapes = -> [Fusion035,Fusion046]
FEATURE [Part::Box] Box123  label="Cube123"
  AttacherType = Attacher::AttachEngine3D
  Height = 1
  Length = 10
  Placement = pos=(-235,35,-14) rot=(0,0,1;0rad)
  Width = 14
FEATURE [Part::Box] Box124  label="Cube124"
  AttacherType = Attacher::AttachEngine3D
  Height = 1
  Length = 10
  Placement = pos=(-235,20,-14) rot=(0,0,1;0rad)
  Width = 14
FEATURE [Part::Box] Box125  label="Cube125"
  AttacherType = Attacher::AttachEngine3D
  Height = 1
  Length = 10
  Placement = pos=(-235,35,-14) rot=(0,0,1;0rad)
  Width = 14
FEATURE [Part::Box] Box126  label="Cube126"
  AttacherType = Attacher::AttachEngine3D
  Height = 1
  Length = 10
  Placement = pos=(-235,20,-14) rot=(0,0,1;0rad)
  Width = 14
FEATURE [Part::Box] Box127  label="Cube127"
  AttacherType = Attacher::AttachEngine3D
  Height = 1
  Length = 10
  Placement = pos=(-235,35,-14) rot=(0,0,1;0rad)
  Width = 14
FEATURE [Part::Box] Box128  label="Cube128"
  AttacherType = Attacher::AttachEngine3D
  Height = 1
  Length = 10
  Placement = pos=(-235,20,-14) rot=(0,0,1;0rad)
  Width = 14
FEATURE [Part::Box] Box129  label="Cube129"
  AttacherType = Attacher::AttachEngine3D
  Height = 1
  Length = 10
  Placement = pos=(-235,35,-14) rot=(0,0,1;0rad)
  Width = 14
FEATURE [Part::Box] Box130  label="Cube130"
  AttacherType = Attacher::AttachEngine3D
  Height = 1
  Length = 10
  Placement = pos=(-235,20,-14) rot=(0,0,1;0rad)
  Width = 14
FEATURE [Part::Box] Box131  label="Cube131"
  AttacherType = Attacher::AttachEngine3D
  Height = 1
  Length = 10
  Placement = pos=(-235,35,-14) rot=(0,0,1;0rad)
  Width = 14
FEATURE [Part::Box] Box132  label="Cube132"
  AttacherType = Attacher::AttachEngine3D
  Height = 1
  Length = 10
  Placement = pos=(-235,20,-14) rot=(0,0,1;0rad)
  Width = 14
FEATURE [Part::Box] Box133  label="Cube133"
  AttacherType = Attacher::AttachEngine3D
  Height = 1
  Length = 10
  Placement = pos=(-235,35,-14) rot=(0,0,1;0rad)
  Width = 14
FEATURE [Part::Box] Box134  label="Cube134"
  AttacherType = Attacher::AttachEngine3D
  Height = 1
  Length = 10
  Placement = pos=(-235,20,-14) rot=(0,0,1;0rad)
  Width = 14
FEATURE [Part::Box] Box135  label="Cube135"
  AttacherType = Attacher::AttachEngine3D
  Height = 1
  Length = 10
  Placement = pos=(-235,35,-14) rot=(0,0,1;0rad)
  Width = 14
FEATURE [Part::Box] Box136  label="Cube136"
  AttacherType = Attacher::AttachEngine3D
  Height = 1
  Length = 10
  Placement = pos=(-235,20,-14) rot=(0,0,1;0rad)
  Width = 14
FEATURE [Part::Box] Box137  label="Cube137"
  AttacherType = Attacher::AttachEngine3D
  Height = 1
  Length = 10
  Placement = pos=(-235,35,-14) rot=(0,0,1;0rad)
  Width = 14
FEATURE [Part::Box] Box138  label="Cube138"
  AttacherType = Attacher::AttachEngine3D
  Height = 1
  Length = 10
  Placement = pos=(-235,20,-14) rot=(0,0,1;0rad)
  Width = 14
FEATURE [Part::Box] Box139  label="Cube139"
  AttacherType = Attacher::AttachEngine3D
  Height = 1
  Length = 10
  Placement = pos=(-235,35,-14) rot=(0,0,1;0rad)
  Width = 14
FEATURE [Part::Box] Box140  label="Cube140"
  AttacherType = Attacher::AttachEngine3D
  Height = 1
  Length = 10
  Placement = pos=(-235,20,-14) rot=(0,0,1;0rad)
  Width = 14
FEATURE [Part::Box] Box142  label="Cube142"
  AttacherType = Attacher::AttachEngine3D
  Height = 1
  Length = 10
  Placement = pos=(-235,20,-14) rot=(0,0,1;0rad)
  Width = 14
FEATURE [Part::Box] Box143  label="Cube143"
  AttacherType = Attacher::AttachEngine3D
  Height = 1
  Length = 10
  Placement = pos=(-235,35,-14) rot=(0,0,1;0rad)
  Width = 14
FEATURE [Part::Box] Box144  label="Cube144"
  AttacherType = Attacher::AttachEngine3D
  Height = 1
  Length = 10
  Placement = pos=(-235,20,-14) rot=(0,0,1;0rad)
  Width = 14
FEATURE [Part::Box] Box145  label="Cube145"
  AttacherType = Attacher::AttachEngine3D
  Height = 1
  Length = 10
  Placement = pos=(-235,35,-14) rot=(0,0,1;0rad)
  Width = 14
FEATURE [Part::Box] Box146  label="Cube146"
  AttacherType = Attacher::AttachEngine3D
  Height = 1
  Length = 10
  Placement = pos=(-235,20,-14) rot=(0,0,1;0rad)
  Width = 14
FEATURE [Part::Box] Box147  label="Cube147"
  AttacherType = Attacher::AttachEngine3D
  Height = 1
  Length = 10
  Placement = pos=(-235,35,-14) rot=(0,0,1;0rad)
  Width = 14
FEATURE [Part::Box] Box148  label="Cube148"
  AttacherType = Attacher::AttachEngine3D
  Height = 1
  Length = 10
  Placement = pos=(-235,20,-14) rot=(0,0,1;0rad)
  Width = 14
FEATURE [Part::Box] Box149  label="Cube149"
  AttacherType = Attacher::AttachEngine3D
  Height = 1
  Length = 10
  Placement = pos=(-235,35,-14) rot=(0,0,1;0rad)
  Width = 14
FEATURE [Part::Box] Box150  label="Cube150"
  AttacherType = Attacher::AttachEngine3D
  Height = 1
  Length = 10
  Placement = pos=(-235,20,-14) rot=(0,0,1;0rad)
  Width = 14
FEATURE [Part::Box] Box151  label="Cube151"
  AttacherType = Attacher::AttachEngine3D
  Height = 1
  Length = 10
  Placement = pos=(-235,35,-14) rot=(0,0,1;0rad)
  Width = 14
FEATURE [Part::Box] Box152  label="Cube152"
  AttacherType = Attacher::AttachEngine3D
  Height = 1
  Length = 10
  Placement = pos=(-235,20,-14) rot=(0,0,1;0rad)
  Width = 14
FEATURE [Part::Box] Box153  label="Cube153"
  AttacherType = Attacher::AttachEngine3D
  Height = 1
  Length = 10
  Placement = pos=(-235,35,-14) rot=(0,0,1;0rad)
  Width = 14
FEATURE [Part::Box] Box154  label="Cube154"
  AttacherType = Attacher::AttachEngine3D
  Height = 1
  Length = 10
  Placement = pos=(-235,20,-14) rot=(0,0,1;0rad)
  Width = 14
FEATURE [Part::Box] Box155  label="Cube155"
  AttacherType = Attacher::AttachEngine3D
  Height = 1
  Length = 10
  Placement = pos=(-235,35,-14) rot=(0,0,1;0rad)
  Width = 14
FEATURE [Part::Box] Box156  label="Cube156"
  AttacherType = Attacher::AttachEngine3D
  Height = 1
  Length = 10
  Placement = pos=(-235,20,-14) rot=(0,0,1;0rad)
  Width = 14
FEATURE [Part::Box] Box157  label="Cube157"
  AttacherType = Attacher::AttachEngine3D
  Height = 1
  Length = 10
  Placement = pos=(-235,35,-14) rot=(0,0,1;0rad)
  Width = 14
FEATURE [Part::Box] Box158  label="Cube158"
  AttacherType = Attacher::AttachEngine3D
  Height = 1
  Length = 10
  Placement = pos=(-235,20,-14) rot=(0,0,1;0rad)
  Width = 14
FEATURE [Part::Box] Box159  label="Cube159"
  AttacherType = Attacher::AttachEngine3D
  Height = 1
  Length = 10
  Placement = pos=(-235,35,-14) rot=(0,0,1;0rad)
  Width = 14
FEATURE [Part::Box] Box160  label="Cube160"
  AttacherType = Attacher::AttachEngine3D
  Height = 1
  Length = 10
  Placement = pos=(-235,20,-14) rot=(0,0,1;0rad)
  Width = 14
FEATURE [Part::MultiFuse] Fusion049
  Placement = pos=(0,0,-2) rot=(0,0,1;0rad)
  Shapes = -> [Box123,Box124]
FEATURE [Part::MultiFuse] Fusion050
  Placement = pos=(0,0,-4) rot=(0,0,1;0rad)
  Shapes = -> [Box125,Box126]
FEATURE [Part::MultiFuse] Fusion051
  Placement = pos=(0,0,-6) rot=(0,0,1;0rad)
  Shapes = -> [Box127,Box128]
FEATURE [Part::MultiFuse] Fusion052
  Placement = pos=(0,0,-8) rot=(0,0,1;0rad)
  Shapes = -> [Box129,Box130]
FEATURE [Part::MultiFuse] Fusion053
  Placement = pos=(0,0,-10) rot=(0,0,1;0rad)
  Shapes = -> [Box131,Box132]
FEATURE [Part::MultiFuse] Fusion054
  Placement = pos=(0,0,-12) rot=(0,0,1;0rad)
  Shapes = -> [Box133,Box134]
FEATURE [Part::MultiFuse] Fusion055
  Placement = pos=(0,0,-14) rot=(0,0,1;0rad)
  Shapes = -> [Box135,Box136]
FEATURE [Part::MultiFuse] Fusion056
  Placement = pos=(0,0,-16) rot=(0,0,1;0rad)
  Shapes = -> [Box137,Box138]
FEATURE [Part::MultiFuse] Fusion057
  Placement = pos=(0,0,-18) rot=(0,0,1;0rad)
  Shapes = -> [Box139,Box140]
FEATURE [Part::MultiFuse] Fusion058
  Shapes = -> [Fusion049,Fusion050,Fusion051,Fusion052,Fusion053,Fusion054,Fusion055,Fusion056,Fusion057]
FEATURE [Part::MultiFuse] Fusion060
  Placement = pos=(0,0,-2) rot=(0,0,1;0rad)
  Shapes = -> [Box143,Box144]
FEATURE [Part::MultiFuse] Fusion061
  Placement = pos=(0,0,-4) rot=(0,0,1;0rad)
  Shapes = -> [Box145,Box146]
FEATURE [Part::MultiFuse] Fusion062
  Placement = pos=(0,0,-6) rot=(0,0,1;0rad)
  Shapes = -> [Box147,Box148]
FEATURE [Part::MultiFuse] Fusion063
  Placement = pos=(0,0,-8) rot=(0,0,1;0rad)
  Shapes = -> [Box149,Box150]
FEATURE [Part::MultiFuse] Fusion064
  Placement = pos=(0,0,-10) rot=(0,0,1;0rad)
  Shapes = -> [Box151,Box152]
FEATURE [Part::MultiFuse] Fusion065
  Placement = pos=(0,0,-12) rot=(0,0,1;0rad)
  Shapes = -> [Box153,Box154]
FEATURE [Part::MultiFuse] Fusion067
  Placement = pos=(0,0,-16) rot=(0,0,1;0rad)
  Shapes = -> [Box157,Box158]
FEATURE [Part::MultiFuse] Fusion068
  Placement = pos=(0,0,-18) rot=(0,0,1;0rad)
  Shapes = -> [Box159,Box160]
FEATURE [Part::MultiFuse] Fusion066
  Placement = pos=(0,0,-14) rot=(0,0,1;0rad)
  Shapes = -> [Box155,Box156]
FEATURE [Part::Box] Box141  label="Cube141"
  AttacherType = Attacher::AttachEngine3D
  Height = 1
  Length = 10
  Placement = pos=(-235,35,-14) rot=(0,0,1;0rad)
  Width = 14
FEATURE [Part::MultiFuse] Fusion059
  Shapes = -> [Box141,Box142]
FEATURE [Part::MultiFuse] Fusion069
  Placement = pos=(0,0,-20) rot=(0,0,1;0rad)
  Shapes = -> [Fusion059,Fusion060,Fusion061,Fusion062,Fusion063,Fusion064,Fusion065,Fusion066,Fusion067,Fusion068]
FEATURE [Part::MultiFuse] Fusion070
  Placement = pos=(-253,-157,40) rot=(0,0,-1;1.5708rad)
  Shapes = -> [Fusion058,Fusion069]
FEATURE [Part::MultiFuse] Fusion071  label="vent2"
  Placement = pos=(10,0,4) rot=(0,0,1;0rad)
  Shapes = -> [Fusion047,Fusion070]
FEATURE [Part::Cut] Cut007
  Base = -> Cut006
  Tool = -> Fusion071
FEATURE [Part::Box] Box161  label="Cube161"
  AttacherType = Attacher::AttachEngine3D
  Height = 1
  Length = 10
  Placement = pos=(-235,35,-14) rot=(0,0,1;0rad)
  Width = 14
FEATURE [Part::Box] Box162  label="Cube162"
  AttacherType = Attacher::AttachEngine3D
  Height = 1
  Length = 10
  Placement = pos=(-235,20,-14) rot=(0,0,1;0rad)
  Width = 14
FEATURE [Part::Box] Box163  label="Cube163"
  AttacherType = Attacher::AttachEngine3D
  Height = 1
  Length = 10
  Placement = pos=(-235,35,-14) rot=(0,0,1;0rad)
  Width = 14
FEATURE [Part::Box] Box164  label="Cube164"
  AttacherType = Attacher::AttachEngine3D
  Height = 1
  Length = 10
  Placement = pos=(-235,20,-14) rot=(0,0,1;0rad)
  Width = 14
FEATURE [Part::Box] Box165  label="Cube165"
  AttacherType = Attacher::AttachEngine3D
  Height = 1
  Length = 10
  Placement = pos=(-235,35,-14) rot=(0,0,1;0rad)
  Width = 14
FEATURE [Part::Box] Box166  label="Cube166"
  AttacherType = Attacher::AttachEngine3D
  Height = 1
  Length = 10
  Placement = pos=(-235,20,-14) rot=(0,0,1;0rad)
  Width = 14
FEATURE [Part::Box] Box167  label="Cube167"
  AttacherType = Attacher::AttachEngine3D
  Height = 1
  Length = 10
  Placement = pos=(-235,35,-14) rot=(0,0,1;0rad)
  Width = 14
FEATURE [Part::Box] Box168  label="Cube168"
  AttacherType = Attacher::AttachEngine3D
  Height = 1
  Length = 10
  Placement = pos=(-235,20,-14) rot=(0,0,1;0rad)
  Width = 14
FEATURE [Part::Box] Box169  label="Cube169"
  AttacherType = Attacher::AttachEngine3D
  Height = 1
  Length = 10
  Placement = pos=(-235,35,-14) rot=(0,0,1;0rad)
  Width = 14
FEATURE [Part::Box] Box170  label="Cube170"
  AttacherType = Attacher::AttachEngine3D
  Height = 1
  Length = 10
  Placement = pos=(-235,20,-14) rot=(0,0,1;0rad)
  Width = 14
FEATURE [Part::Box] Box171  label="Cube171"
  AttacherType = Attacher::AttachEngine3D
  Height = 1
  Length = 10
  Placement = pos=(-235,35,-14) rot=(0,0,1;0rad)
  Width = 14
FEATURE [Part::Box] Box172  label="Cube172"
  AttacherType = Attacher::AttachEngine3D
  Height = 1
  Length = 10
  Placement = pos=(-235,20,-14) rot=(0,0,1;0rad)
  Width = 14
FEATURE [Part::Box] Box173  label="Cube173"
  AttacherType = Attacher::AttachEngine3D
  Height = 1
  Length = 10
  Placement = pos=(-235,35,-14) rot=(0,0,1;0rad)
  Width = 14
FEATURE [Part::Box] Box174  label="Cube174"
  AttacherType = Attacher::AttachEngine3D
  Height = 1
  Length = 10
  Placement = pos=(-235,20,-14) rot=(0,0,1;0rad)
  Width = 14
FEATURE [Part::Box] Box175  label="Cube175"
  AttacherType = Attacher::AttachEngine3D
  Height = 1
  Length = 10
  Placement = pos=(-235,35,-14) rot=(0,0,1;0rad)
  Width = 14
FEATURE [Part::Box] Box176  label="Cube176"
  AttacherType = Attacher::AttachEngine3D
  Height = 1
  Length = 10
  Placement = pos=(-235,20,-14) rot=(0,0,1;0rad)
  Width = 14
FEATURE [Part::Box] Box177  label="Cube177"
  AttacherType = Attacher::AttachEngine3D
  Height = 1
  Length = 10
  Placement = pos=(-235,35,-14) rot=(0,0,1;0rad)
  Width = 14
FEATURE [Part::Box] Box178  label="Cube178"
  AttacherType = Attacher::AttachEngine3D
  Height = 1
  Length = 10
  Placement = pos=(-235,20,-14) rot=(0,0,1;0rad)
  Width = 14
FEATURE [Part::Box] Box179  label="Cube179"
  AttacherType = Attacher::AttachEngine3D
  Height = 1
  Length = 10
  Placement = pos=(-235,35,-14) rot=(0,0,1;0rad)
  Width = 14
FEATURE [Part::Box] Box180  label="Cube180"
  AttacherType = Attacher::AttachEngine3D
  Height = 1
  Length = 10
  Placement = pos=(-235,20,-14) rot=(0,0,1;0rad)
  Width = 14
FEATURE [Part::Box] Box181  label="Cube181"
  AttacherType = Attacher::AttachEngine3D
  Height = 1
  Length = 10
  Placement = pos=(-235,35,-14) rot=(0,0,1;0rad)
  Width = 14
FEATURE [Part::Box] Box182  label="Cube182"
  AttacherType = Attacher::AttachEngine3D
  Height = 1
  Length = 10
  Placement = pos=(-235,20,-14) rot=(0,0,1;0rad)
  Width = 14
FEATURE [Part::Box] Box183  label="Cube183"
  AttacherType = Attacher::AttachEngine3D
  Height = 1
  Length = 10
  Placement = pos=(-235,35,-14) rot=(0,0,1;0rad)
  Width = 14
FEATURE [Part::Box] Box184  label="Cube184"
  AttacherType = Attacher::AttachEngine3D
  Height = 1
  Length = 10
  Placement = pos=(-235,20,-14) rot=(0,0,1;0rad)
  Width = 14
FEATURE [Part::Box] Box185  label="Cube185"
  AttacherType = Attacher::AttachEngine3D
  Height = 1
  Length = 10
  Placement = pos=(-235,35,-14) rot=(0,0,1;0rad)
  Width = 14
FEATURE [Part::Box] Box186  label="Cube186"
  AttacherType = Attacher::AttachEngine3D
  Height = 1
  Length = 10
  Placement = pos=(-235,20,-14) rot=(0,0,1;0rad)
  Width = 14
FEATURE [Part::Box] Box187  label="Cube187"
  AttacherType = Attacher::AttachEngine3D
  Height = 1
  Length = 10
  Placement = pos=(-235,35,-14) rot=(0,0,1;0rad)
  Width = 14
FEATURE [Part::Box] Box188  label="Cube188"
  AttacherType = Attacher::AttachEngine3D
  Height = 1
  Length = 10
  Placement = pos=(-235,20,-14) rot=(0,0,1;0rad)
  Width = 14
FEATURE [Part::Box] Box189  label="Cube189"
  AttacherType = Attacher::AttachEngine3D
  Height = 1
  Length = 10
  Placement = pos=(-235,35,-14) rot=(0,0,1;0rad)
  Width = 14
FEATURE [Part::Box] Box190  label="Cube190"
  AttacherType = Attacher::AttachEngine3D
  Height = 1
  Length = 10
  Placement = pos=(-235,20,-14) rot=(0,0,1;0rad)
  Width = 14
FEATURE [Part::Box] Box191  label="Cube191"
  AttacherType = Attacher::AttachEngine3D
  Height = 1
  Length = 10
  Placement = pos=(-235,35,-14) rot=(0,0,1;0rad)
  Width = 14
FEATURE [Part::Box] Box192  label="Cube192"
  AttacherType = Attacher::AttachEngine3D
  Height = 1
  Length = 10
  Placement = pos=(-235,20,-14) rot=(0,0,1;0rad)
  Width = 14
FEATURE [Part::Box] Box193  label="Cube193"
  AttacherType = Attacher::AttachEngine3D
  Height = 1
  Length = 10
  Placement = pos=(-235,35,-14) rot=(0,0,1;0rad)
  Width = 14
FEATURE [Part::Box] Box194  label="Cube194"
  AttacherType = Attacher::AttachEngine3D
  Height = 1
  Length = 10
  Placement = pos=(-235,20,-14) rot=(0,0,1;0rad)
  Width = 14
FEATURE [Part::Box] Box195  label="Cube195"
  AttacherType = Attacher::AttachEngine3D
  Height = 1
  Length = 10
  Placement = pos=(-235,35,-14) rot=(0,0,1;0rad)
  Width = 14
FEATURE [Part::Box] Box196  label="Cube196"
  AttacherType = Attacher::AttachEngine3D
  Height = 1
  Length = 10
  Placement = pos=(-235,20,-14) rot=(0,0,1;0rad)
  Width = 14
FEATURE [Part::Box] Box197  label="Cube197"
  AttacherType = Attacher::AttachEngine3D
  Height = 1
  Length = 10
  Placement = pos=(-235,35,-14) rot=(0,0,1;0rad)
  Width = 14
FEATURE [Part::Box] Box198  label="Cube198"
  AttacherType = Attacher::AttachEngine3D
  Height = 1
  Length = 10
  Placement = pos=(-235,20,-14) rot=(0,0,1;0rad)
  Width = 14
FEATURE [Part::Box] Box199  label="Cube199"
  AttacherType = Attacher::AttachEngine3D
  Height = 1
  Length = 10
  Placement = pos=(-235,35,-14) rot=(0,0,1;0rad)
  Width = 14
FEATURE [Part::Box] Box200  label="Cube200"
  AttacherType = Attacher::AttachEngine3D
  Height = 1
  Length = 10
  Placement = pos=(-235,20,-14) rot=(0,0,1;0rad)
  Width = 14
FEATURE [Part::MultiFuse] Fusion072
  Shapes = -> [Box161,Box162]
FEATURE [Part::MultiFuse] Fusion073
  Placement = pos=(0,0,-2) rot=(0,0,1;0rad)
  Shapes = -> [Box163,Box164]
FEATURE [Part::MultiFuse] Fusion074
  Placement = pos=(0,0,-4) rot=(0,0,1;0rad)
  Shapes = -> [Box165,Box166]
FEATURE [Part::MultiFuse] Fusion075
  Placement = pos=(0,0,-6) rot=(0,0,1;0rad)
  Shapes = -> [Box167,Box168]
FEATURE [Part::MultiFuse] Fusion076
  Placement = pos=(0,0,-8) rot=(0,0,1;0rad)
  Shapes = -> [Box169,Box170]
FEATURE [Part::MultiFuse] Fusion077
  Placement = pos=(0,0,-10) rot=(0,0,1;0rad)
  Shapes = -> [Box171,Box172]
FEATURE [Part::MultiFuse] Fusion078
  Placement = pos=(0,0,-12) rot=(0,0,1;0rad)
  Shapes = -> [Box173,Box174]
FEATURE [Part::MultiFuse] Fusion079
  Placement = pos=(0,0,-14) rot=(0,0,1;0rad)
  Shapes = -> [Box175,Box176]
FEATURE [Part::MultiFuse] Fusion080
  Placement = pos=(0,0,-16) rot=(0,0,1;0rad)
  Shapes = -> [Box177,Box178]
FEATURE [Part::MultiFuse] Fusion081
  Placement = pos=(0,0,-18) rot=(0,0,1;0rad)
  Shapes = -> [Box179,Box180]
FEATURE [Part::MultiFuse] Fusion082
  Shapes = -> [Fusion072,Fusion073,Fusion074,Fusion075,Fusion076,Fusion077,Fusion078,Fusion079,Fusion080,Fusion081]
FEATURE [Part::MultiFuse] Fusion083
  Shapes = -> [Box181,Box182]
FEATURE [Part::MultiFuse] Fusion084
  Placement = pos=(0,0,-2) rot=(0,0,1;0rad)
  Shapes = -> [Box183,Box184]
FEATURE [Part::MultiFuse] Fusion085
  Placement = pos=(0,0,-4) rot=(0,0,1;0rad)
  Shapes = -> [Box185,Box186]
FEATURE [Part::MultiFuse] Fusion086
  Placement = pos=(0,0,-6) rot=(0,0,1;0rad)
  Shapes = -> [Box187,Box188]
FEATURE [Part::MultiFuse] Fusion087
  Placement = pos=(0,0,-8) rot=(0,0,1;0rad)
  Shapes = -> [Box189,Box190]
FEATURE [Part::MultiFuse] Fusion088
  Placement = pos=(0,0,-10) rot=(0,0,1;0rad)
  Shapes = -> [Box191,Box192]
FEATURE [Part::MultiFuse] Fusion089
  Placement = pos=(0,0,-12) rot=(0,0,1;0rad)
  Shapes = -> [Box193,Box194]
FEATURE [Part::MultiFuse] Fusion090
  Placement = pos=(0,0,-14) rot=(0,0,1;0rad)
  Shapes = -> [Box195,Box196]
FEATURE [Part::MultiFuse] Fusion091
  Placement = pos=(0,0,-16) rot=(0,0,1;0rad)
  Shapes = -> [Box197,Box198]
FEATURE [Part::MultiFuse] Fusion092
  Placement = pos=(0,0,-18) rot=(0,0,1;0rad)
  Shapes = -> [Box199,Box200]
FEATURE [Part::MultiFuse] Fusion093
  Placement = pos=(0,0,-20) rot=(0,0,1;0rad)
  Shapes = -> [Fusion083,Fusion084,Fusion085,Fusion086,Fusion087,Fusion088,Fusion089,Fusion090,Fusion091,Fusion092]
FEATURE [Part::MultiFuse] Fusion094
  Placement = pos=(-253,-157,0) rot=(0,0,-1;1.5708rad)
  Shapes = -> [Fusion082,Fusion093]
FEATURE [Part::MultiFuse] Fusion117  label="vent003"
  Placement = pos=(8,77,21) rot=(-1,0,0;1.5708rad)
  Shapes = -> [Fusion094]
FEATURE [Part::Cut] Cut008
  Base = -> Cut007
  Tool = -> Fusion117
FEATURE [Part::Cylinder] Cylinder004
  Angle = 360
  AttacherType = Attacher::AttachEngine3D
  FirstAngle = 0
  Height = 10
  Placement = pos=(-226.5,68,-58) rot=(0,0,1;0rad)
  Radius = 5
  SecondAngle = 0
FEATURE [Part::Fillet] Fillet  label="stand1"
  Base = -> Cylinder004
  Edges = 1 edges r=2: [Edge2]
FEATURE [Part::Cylinder] Cylinder005
  Angle = 360
  AttacherType = Attacher::AttachEngine3D
  FirstAngle = 0
  Height = 10
  Placement = pos=(-226.5,68,-58) rot=(0,0,1;0rad)
  Radius = 5
  SecondAngle = 0
FEATURE [Part::Fillet] Fillet001  label="stand002"
  Base = -> Cylinder005
  Edges = 1 edges r=2: [Edge2]
  Placement = pos=(13,-124,0) rot=(0,0,1;0rad)
FEATURE [Part::Cylinder] Cylinder006
  Angle = 360
  AttacherType = Attacher::AttachEngine3D
  FirstAngle = 0
  Height = 10
  Placement = pos=(-226.5,68,-58) rot=(0,0,1;0rad)
  Radius = 5
  SecondAngle = 0
FEATURE [Part::Fillet] Fillet002  label="stand003"
  Base = -> Cylinder006
  Edges = 1 edges r=2: [Edge2]
  Placement = pos=(205,-124,0) rot=(0,0,1;0rad)
FEATURE [Part::Cylinder] Cylinder007
  Angle = 360
  AttacherType = Attacher::AttachEngine3D
  FirstAngle = 0
  Height = 10
  Placement = pos=(-226.5,68,-58) rot=(0,0,1;0rad)
  Radius = 6
  SecondAngle = 0
FEATURE [Part::Fillet] Fillet003  label="stand004"
  Base = -> Cylinder007
  Edges = 1 edges r=1: [Edge2]
  Placement = pos=(105.5,-123,0) rot=(0,0,1;0rad)
FEATURE [Part::Cylinder] Cylinder008
  Angle = 360
  AttacherType = Attacher::AttachEngine3D
  FirstAngle = 0
  Height = 10
  Placement = pos=(-226.5,68,-58) rot=(0,0,1;0rad)
  Radius = 6
  SecondAngle = 0
FEATURE [Part::Fillet] Fillet004  label="stand005"
  Base = -> Cylinder008
  Edges = 1 edges r=1: [Edge2]
  Placement = pos=(58.25,-120.25,0) rot=(0,0,1;0rad)
FEATURE [Part::Cylinder] Cylinder009
  Angle = 360
  AttacherType = Attacher::AttachEngine3D
  FirstAngle = 0
  Height = 10
  Placement = pos=(-226.5,68,-58) rot=(0,0,1;0rad)
  Radius = 6
  SecondAngle = 0
FEATURE [Part::Fillet] Fillet005  label="stand006"
  Base = -> Cylinder009
  Edges = 1 edges r=1: [Edge2]
  Placement = pos=(211,-2,0) rot=(0,0,1;0rad)
FEATURE [Part::MultiFuse] Fusion118  label="Palas004"
  Shapes = -> [Fillet,Fillet001,Fillet002,Fillet003,Fillet004,Fillet005,Cut008]
FEATURE [App::Part] Part  label="Palas_Base"
  Group = -> [QY603_inter,_38_206706,Extrude,Extrude001,Extrude002,Fusion016,Fusion019,Fusion013,Fusion017,Fusion015,Fusion014,Fusion018,Box054,Box184,Box001,Cone,Cylinder001,Cylinder,Cylinder002,Cylinder003,Cut004,Cut005,Fusion020,Fusion021,Fusion001,Cut,Cut003,Cut001,Cut002,Fusion,Box002,Box003,Box,Tube,Sketch,Box111,Box114,Box110,Box113,Box107,Box108,Box105,Box116,Box117,Box183,Box124,Box125,Box123,Box119,+261 more]
  Origin = -> Origin
  Placement = pos=(70,76,-101) rot=(0,0,1;0rad)
FEATURE [Part::Feature] Part__Feature016  label="Z_-16147B_ZH-16147B-01"
  shape: bbox 438.9 x 219.4 x 405.1 mm, 3210 faces (baked)
FEATURE [Part::Feature] Part__Feature017  label="INSERTS-4"
  Placement = pos=(-180.975,-168.256,-155.575) rot=(0,0,1;0rad)
  shape: bbox 7.519 x 8.463 x 7.519 mm, 71 faces (baked)
FEATURE [Part::Feature] Part__Feature018  label="INSERTS-005"
  Placement = pos=(-170.872,-174.835,-145.472) rot=(0,0,1;3.14159rad)
  shape: bbox 7.519 x 8.463 x 7.519 mm, 71 faces (baked)
FEATURE [Part::Feature] Part__Feature019  label="INSERTS-006"
  Placement = pos=(-205.994,-3.7592,-180.594) rot=(0,0,1;3.14159rad)
  shape: bbox 7.519 x 8.463 x 7.519 mm, 71 faces (baked)
FEATURE [Part::Feature] Part__Feature020  label="INSERTS-007"
  Placement = pos=(-180.975,-168.083,155.575) rot=(1,0,0;3.14159rad)
  shape: bbox 7.519 x 8.463 x 7.519 mm, 71 faces (baked)
FEATURE [Part::Feature] Part__Feature021  label="INSERTS-008"
  Placement = pos=(-170.872,-175.008,145.472) rot=(0,1,0;3.14159rad)
  shape: bbox 7.519 x 8.463 x 7.519 mm, 71 faces (baked)
FEATURE [Part::Feature] Part__Feature022  label="INSERTS-009"
  Placement = pos=(-205.994,-3.93217,180.594) rot=(0,1,0;3.14159rad)
  shape: bbox 7.519 x 8.463 x 7.519 mm, 71 faces (baked)
FEATURE [Part::Feature] Part__Feature023  label="INSERTS-010"
  Placement = pos=(180.975,-168.083,-155.575) rot=(0,0,1;3.14159rad)
  shape: bbox 7.519 x 8.463 x 7.519 mm, 71 faces (baked)
FEATURE [Part::Feature] Part__Feature024  label="INSERTS-011"
  Placement = pos=(170.872,-175.008,-145.472) rot=(0,0,1;0rad)
  shape: bbox 7.519 x 8.463 x 7.519 mm, 71 faces (baked)
FEATURE [Part::Feature] Part__Feature025  label="INSERTS-012"
  Placement = pos=(205.994,-3.93217,-180.594) rot=(0,0,1;0rad)
  shape: bbox 7.519 x 8.463 x 7.519 mm, 71 faces (baked)
FEATURE [Part::Feature] Part__Feature026  label="INSERTS-013"
  Placement = pos=(180.975,-168.256,155.575) rot=(0,1,0;3.14159rad)
  shape: bbox 7.519 x 8.463 x 7.519 mm, 71 faces (baked)
FEATURE [Part::Feature] Part__Feature027  label="INSERTS-014"
  Placement = pos=(170.872,-174.835,145.472) rot=(1,0,0;3.14159rad)
  shape: bbox 7.519 x 8.463 x 7.519 mm, 71 faces (baked)
FEATURE [Part::Feature] Part__Feature028  label="INSERTS-015"
  Placement = pos=(205.994,-3.7592,180.594) rot=(1,0,0;3.14159rad)
  shape: bbox 7.519 x 8.463 x 7.519 mm, 71 faces (baked)
FEATURE [Part::Feature] Part__Feature029  label="LABEL-104"
  Placement = pos=(-1.221e-12,-20.3197,-180.67) rot=(1,0,0;1.56207rad)
  shape: bbox 63.5 x 38.1 x 0.3833 mm, 10 faces (baked)
FEATURE [Part::Feature] Part__Feature030  label="Z_-16141C_ZH-16141C-01"
  shape: bbox 448.9 x 49.63 x 409 mm, 1738 faces (baked)
FEATURE [Part::Feature] Part__Feature031  label="ZH-1614G"
  Placement = pos=(0,0.635,6.9e-15) rot=(0,0,1;0rad)
  shape: bbox 434.5 x 6.35 x 383.7 mm, 136 faces (baked)
FEATURE [Part::Feature] Part__Feature032  label="ZH-01F_ZH-01F-01"
  Placement = pos=(-158.172,-191.294,-145.472) rot=(0,0,1;0rad)
  shape: bbox 75.05 x 15.88 x 54.71 mm, 393 faces (baked)
FEATURE [Part::Feature] Part__Feature033  label="pan cross head_ai_SCREWS-046"
  Placement = pos=(-170.872,-191.294,-145.472) rot=(-0.002139,-0.002139,0.999995;1.5708rad)
  shape: bbox 10.25 x 22.43 x 10.25 mm, 92 faces (baked)
FEATURE [Part::Feature] Part__Feature034  label="pan cross head_ai_SCREWS-047"
  Placement = pos=(-170.872,-191.294,145.472) rot=(0.002139,0.002139,0.999995;1.5708rad)
  shape: bbox 10.25 x 22.43 x 10.25 mm, 92 faces (baked)
FEATURE [Part::Feature] Part__Feature035  label="ZH-01F_ZH-01F-002"
  Placement = pos=(-158.172,-191.294,145.472) rot=(0,0,1;0rad)
  shape: bbox 75.05 x 15.88 x 54.71 mm, 393 faces (baked)
FEATURE [Part::Feature] Part__Feature036  label="pan cross head_ai_SCREWS-048"
  Placement = pos=(170.872,-191.294,-145.472) rot=(0.707106,0.707106,-0.001512;3.14462rad)
  shape: bbox 10.25 x 22.43 x 10.25 mm, 92 faces (baked)
FEATURE [Part::Feature] Part__Feature037  label="pan cross head_ai_SCREWS-049"
  Placement = pos=(170.872,-191.294,145.472) rot=(0.707106,0.707106,0.001512;3.13857rad)
  shape: bbox 10.25 x 22.43 x 10.25 mm, 92 faces (baked)
FEATURE [Part::Feature] Part__Feature038  label="ZH-01F_ZH-01F-003"
  Placement = pos=(158.172,-191.294,-145.472) rot=(0,1,0;3.14159rad)
  shape: bbox 75.05 x 15.88 x 54.71 mm, 393 faces (baked)
FEATURE [Part::Feature] Part__Feature039  label="ZH-01F_ZH-01F-004"
  Placement = pos=(158.172,-191.294,145.472) rot=(0,1,0;3.14159rad)
  shape: bbox 75.05 x 15.88 x 54.71 mm, 393 faces (baked)
FEATURE [Part::Feature] Part__Feature040  label="SCREWS-047_default"
  Placement = pos=(-205.994,12.0142,-180.594) rot=(-1,0,0;1.5708rad)
  shape: bbox 9.234 x 22.51 x 9.177 mm, 32 faces (baked)
FEATURE [Part::Feature] Part__Feature041  label="SCREWS-047_default001"
  Placement = pos=(205.994,12.0142,-180.594) rot=(-1,0,0;1.5708rad)
  shape: bbox 9.234 x 22.51 x 9.177 mm, 32 faces (baked)
FEATURE [Part::Feature] Part__Feature042  label="SCREWS-047_default002"
  Placement = pos=(-205.994,12.0142,180.594) rot=(-1,0,0;1.5708rad)
  shape: bbox 9.234 x 22.51 x 9.177 mm, 32 faces (baked)
FEATURE [Part::Feature] Part__Feature043  label="SCREWS-047_default003"
  Placement = pos=(205.994,12.0142,180.594) rot=(-1,0,0;1.5708rad)
  shape: bbox 9.234 x 22.51 x 9.177 mm, 32 faces (baked)
FEATURE [App::Part] Z__16141CG_ZH_16141CG_01  label="Z_-16141CG_ZH-16141CG-01"
  Group = -> [Part__Feature030,Part__Feature031]
  Origin = -> Origin005
  Placement = pos=(0,144.582,-60.2035) rot=(-1,0,0;0.785398rad)
FEATURE [App::Part] Z__16147BI_ZH_16147BI_01  label="Z_-16147BI_ZH-16147BI-01"
  Group = -> [Part__Feature016,Part__Feature017,Part__Feature018,Part__Feature019,Part__Feature020,Part__Feature021,Part__Feature022,Part__Feature023,Part__Feature024,Part__Feature025,Part__Feature026,Part__Feature027,Part__Feature028,Part__Feature029]
  Origin = -> Origin004
FEATURE [App::Part] ZH_161407_33  label="ZH-161407-33"
  Group = -> [Z__16147BI_ZH_16147BI_01,Z__16141CG_ZH_16141CG_01,Part__Feature032,Part__Feature033,Part__Feature034,Part__Feature035,Part__Feature036,Part__Feature037,Part__Feature038,Part__Feature039,Part__Feature040,Part__Feature041,Part__Feature042,Part__Feature043]
  Origin = -> Origin006
  Placement = pos=(0,0,0) rot=(1,0,0;1.5708rad)
FEATURE [Sketcher::SketchObject] Sketch002
  FullyConstrained = true
  sketch-geometry (66):
    g0: LineSegment StartX=195 StartY=171 StartZ=0 EndX=-195 EndY=171 EndZ=0
    g1: LineSegment StartX=-195 StartY=171 StartZ=0 EndX=-195 EndY=-171 EndZ=0
    g2: LineSegment StartX=-195 StartY=-171 StartZ=0 EndX=195 EndY=-171 EndZ=0
    g3: LineSegment StartX=195 StartY=-171 StartZ=0 EndX=195 EndY=171 EndZ=0
    g4: Circle CenterX=-165 CenterY=-141 CenterZ=0 NormalX=0 NormalY=0 NormalZ=1 AngleXU=0 Radius=2.25
    g5: Circle CenterX=-165 CenterY=-111 CenterZ=0 NormalX=0 NormalY=0 NormalZ=1 AngleXU=0 Radius=2.25
    g6: Circle CenterX=-165 CenterY=-81 CenterZ=0 NormalX=0 NormalY=0 NormalZ=1 AngleXU=0 Radius=2.25
    g7: Circle CenterX=-165 CenterY=-51 CenterZ=0 NormalX=0 NormalY=0 NormalZ=1 AngleXU=0 Radius=2.25
    g8: Circle CenterX=-120 CenterY=-141 CenterZ=0 NormalX=0 NormalY=0 NormalZ=1 AngleXU=0 Radius=1.75
    g9: Circle CenterX=-120 CenterY=-111 CenterZ=0 NormalX=0 NormalY=0 NormalZ=1 AngleXU=0 Radius=1.75
    g10: Circle CenterX=-120 CenterY=-81 CenterZ=0 NormalX=0 NormalY=0 NormalZ=1 AngleXU=0 Radius=1.75
    g11: Circle CenterX=-120 CenterY=-51 CenterZ=0 NormalX=0 NormalY=0 NormalZ=1 AngleXU=0 Radius=1.75
    g12: Circle CenterX=-75 CenterY=-51 CenterZ=0 NormalX=0 NormalY=0 NormalZ=1 AngleXU=0 Radius=2.25
    g13: Circle CenterX=-75 CenterY=-81 CenterZ=0 NormalX=0 NormalY=0 NormalZ=1 AngleXU=0 Radius=2.25
    g14: Circle CenterX=-75 CenterY=-111 CenterZ=0 NormalX=0 NormalY=0 NormalZ=1 AngleXU=0 Radius=2.25
    g15: Circle CenterX=-75 CenterY=-141 CenterZ=0 NormalX=0 NormalY=0 NormalZ=1 AngleXU=0 Radius=2.25
    g16: Circle CenterX=-30 CenterY=-51 CenterZ=0 NormalX=0 NormalY=0 NormalZ=1 AngleXU=0 Radius=1.75
    g17: Circle CenterX=-30 CenterY=-81 CenterZ=0 NormalX=0 NormalY=0 NormalZ=1 AngleXU=0 Radius=1.75
    g18: Circle CenterX=-30 CenterY=-111 CenterZ=0 NormalX=0 NormalY=0 NormalZ=1 AngleXU=0 Radius=1.75
    g19: Circle CenterX=-30 CenterY=-141 CenterZ=0 NormalX=0 NormalY=0 NormalZ=1 AngleXU=0 Radius=1.75
    g20: Circle CenterX=60 CenterY=-51 CenterZ=0 NormalX=0 NormalY=0 NormalZ=1 AngleXU=0 Radius=1.75
    g21: Circle CenterX=60 CenterY=-81 CenterZ=0 NormalX=0 NormalY=0 NormalZ=1 AngleXU=0 Radius=1.75
    g22: Circle CenterX=60 CenterY=-111 CenterZ=0 NormalX=0 NormalY=0 NormalZ=1 AngleXU=0 Radius=1.75
    g23: Circle CenterX=60 CenterY=-141 CenterZ=0 NormalX=0 NormalY=0 NormalZ=1 AngleXU=0 Radius=1.75
    g24: Circle CenterX=15 CenterY=-51 CenterZ=0 NormalX=0 NormalY=0 NormalZ=1 AngleXU=0 Radius=2.25
    g25: Circle CenterX=15 CenterY=-81 CenterZ=0 NormalX=0 NormalY=0 NormalZ=1 AngleXU=0 Radius=2.25
    g26: Circle CenterX=15 CenterY=-111 CenterZ=0 NormalX=0 NormalY=0 NormalZ=1 AngleXU=0 Radius=2.25
    g27: Circle CenterX=15 CenterY=-141 CenterZ=0 NormalX=0 NormalY=0 NormalZ=1 AngleXU=0 Radius=2.25
    g28: Circle CenterX=-180.98 CenterY=155.6 CenterZ=0 NormalX=0 NormalY=0 NormalZ=1 AngleXU=0 Radius=2.5
    g29: Circle CenterX=180.98 CenterY=-155.6 CenterZ=0 NormalX=0 NormalY=0 NormalZ=1 AngleXU=0 Radius=2.5
    g30: Circle CenterX=-180.98 CenterY=-155.6 CenterZ=0 NormalX=0 NormalY=0 NormalZ=1 AngleXU=0 Radius=2.5
    g31: Circle CenterX=105 CenterY=-51 CenterZ=0 NormalX=0 NormalY=0 NormalZ=1 AngleXU=0 Radius=2.25
    g32: Circle CenterX=105 CenterY=-81 CenterZ=0 NormalX=0 NormalY=0 NormalZ=1 AngleXU=0 Radius=2.25
    g33: Circle CenterX=105 CenterY=-111 CenterZ=0 NormalX=0 NormalY=0 NormalZ=1 AngleXU=0 Radius=2.25
    g34: Circle CenterX=105 CenterY=-141 CenterZ=0 NormalX=0 NormalY=0 NormalZ=1 AngleXU=0 Radius=2.25
    g35: Circle CenterX=150 CenterY=-51 CenterZ=0 NormalX=0 NormalY=0 NormalZ=1 AngleXU=0 Radius=1.75
    g36: Circle CenterX=150 CenterY=-81 CenterZ=0 NormalX=0 NormalY=0 NormalZ=1 AngleXU=0 Radius=1.75
    g37: Circle CenterX=150 CenterY=-111 CenterZ=0 NormalX=0 NormalY=0 NormalZ=1 AngleXU=0 Radius=1.75
    g38: Circle CenterX=150 CenterY=-141 CenterZ=0 NormalX=0 NormalY=0 NormalZ=1 AngleXU=0 Radius=1.75
    g39: Circle CenterX=-170.4 CenterY=36 CenterZ=0 NormalX=0 NormalY=0 NormalZ=1 AngleXU=0 Radius=4.6
    g40: Circle CenterX=75 CenterY=36 CenterZ=0 NormalX=0 NormalY=0 NormalZ=1 AngleXU=0 Radius=4.6
    g41: Circle CenterX=-14 CenterY=-7 CenterZ=0 NormalX=0 NormalY=0 NormalZ=1 AngleXU=0 Radius=4.6
    g42: Circle CenterX=-63 CenterY=-7 CenterZ=0 NormalX=0 NormalY=0 NormalZ=1 AngleXU=0 Radius=4.6
    g43: Circle CenterX=-114 CenterY=-7 CenterZ=0 NormalX=0 NormalY=0 NormalZ=1 AngleXU=0 Radius=4.6
    g44: Circle CenterX=-114 CenterY=158 CenterZ=0 NormalX=0 NormalY=0 NormalZ=1 AngleXU=0 Radius=4.6
    g45: Circle CenterX=-63 CenterY=158 CenterZ=0 NormalX=0 NormalY=0 NormalZ=1 AngleXU=0 Radius=4.6
    g46: Circle CenterX=-13 CenterY=157.997 CenterZ=0 NormalX=0 NormalY=0 NormalZ=1 AngleXU=0 Radius=4.6
    g47: Circle CenterX=180.98 CenterY=155.6 CenterZ=0 NormalX=0 NormalY=0 NormalZ=1 AngleXU=0 Radius=2.5
    g48: Circle CenterX=181 CenterY=101.6 CenterZ=0 NormalX=0 NormalY=0 NormalZ=1 AngleXU=0 Radius=1.75
    g49: Circle CenterX=181 CenterY=76.2 CenterZ=0 NormalX=0 NormalY=0 NormalZ=1 AngleXU=0 Radius=1.75
    g50: Circle CenterX=181 CenterY=50.8 CenterZ=0 NormalX=0 NormalY=0 NormalZ=1 AngleXU=0 Radius=1.75
    g51: Circle CenterX=181 CenterY=25.4 CenterZ=0 NormalX=0 NormalY=0 NormalZ=1 AngleXU=0 Radius=1.75
    g52: Circle CenterX=84 CenterY=101.6 CenterZ=0 NormalX=0 NormalY=0 NormalZ=1 AngleXU=0 Radius=1.75
    g53: Circle CenterX=84 CenterY=76.2 CenterZ=0 NormalX=0 NormalY=0 NormalZ=1 AngleXU=0 Radius=1.75
    g54: Circle CenterX=84 CenterY=50.8 CenterZ=0 NormalX=0 NormalY=0 NormalZ=1 AngleXU=0 Radius=1.75
    g55: Circle CenterX=84 CenterY=25.4 CenterZ=0 NormalX=0 NormalY=0 NormalZ=1 AngleXU=0 Radius=1.75
    g56: Circle CenterX=84 CenterY=0 CenterZ=0 NormalX=0 NormalY=0 NormalZ=1 AngleXU=0 Radius=1.75
    g57: Circle CenterX=181 CenterY=7.3e-15 CenterZ=0 NormalX=0 NormalY=0 NormalZ=1 AngleXU=0 Radius=1.75
    g58: Circle CenterX=181 CenterY=127 CenterZ=0 NormalX=0 NormalY=0 NormalZ=1 AngleXU=0 Radius=1.75
    g59: Circle CenterX=155.6 CenterY=127 CenterZ=0 NormalX=0 NormalY=0 NormalZ=1 AngleXU=0 Radius=1.75
    g60: Circle CenterX=130.2 CenterY=127 CenterZ=0 NormalX=0 NormalY=0 NormalZ=1 AngleXU=0 Radius=1.75
    g61: Circle CenterX=104.8 CenterY=127 CenterZ=0 NormalX=0 NormalY=0 NormalZ=1 AngleXU=0 Radius=1.75
    g62: Circle CenterX=84 CenterY=127 CenterZ=0 NormalX=0 NormalY=0 NormalZ=1 AngleXU=0 Radius=1.75
    g63: Circle CenterX=104.8 CenterY=0 CenterZ=0 NormalX=0 NormalY=0 NormalZ=1 AngleXU=0 Radius=1.75
    g64: Circle CenterX=130.2 CenterY=0 CenterZ=0 NormalX=0 NormalY=0 NormalZ=1 AngleXU=0 Radius=1.75
    g65: Circle CenterX=155.6 CenterY=0 CenterZ=0 NormalX=0 NormalY=0 NormalZ=1 AngleXU=0 Radius=1.75
  constraints (173):
    c: Coincident(g0,g1)
    c: Coincident(g1,g2)
    c: Coincident(g2,g3)
    c: Coincident(g3,g0)
    c: Horizontal(g2)
    c: Vertical(g1)
    c: Distance(g0) = 390
    c: DistanceY(g1,g1) = 342
    c: Diameter(g4) = 4.5
    c: Distance(g4,g1) = 30
    c: Distance(g4,g2) = 30
    c: Diameter(g5) = 4.5
    c: Distance(g5,g1) = 30
    c: Distance(g5,g2) = 60
    c: Diameter(g6) = 4.5
    c: Distance(g6,g1) = 30
    c: Distance(g6,g2) = 90
    c: Diameter(g7) = 4.5
    c: Distance(g7,g1) = 30
    c: Distance(g7,g2) = 120
    c: Equal(g11,g10)
    c: Equal(g11,g9)
    c: Equal(g11,g8)
    c: Equal(g11, g16-g23) x8
    c: Diameter(g11) = 3.5
    c: Symmetric(g0,g0,g-2)
    c: Symmetric(g2,g0,g-1)
    c: Distance(g11,g1) = 75
    c: Distance(g10,g1) = 75
    c: Distance(g9,g1) = 75
    c: Distance(g8,g1) = 75
    c: Distance(g12,g1) = 120
    c: Distance(g13,g1) = 120
    c: Distance(g14,g1) = 120
    c: Distance(g15,g1) = 120
    c: Distance(g8,g2) = 30
    c: Distance(g9,g2) = 60
    c: Distance(g10,g2) = 90
    c: Distance(g11,g2) = 120
    c: Distance(g12,g2) = 120
    c: Distance(g13,g2) = 90
    c: Distance(g14,g2) = 60
    c: Distance(g15,g2) = 30
    c: Distance(g16,g1) = 165
    c: Distance(g17,g1) = 165
    c: Distance(g18,g1) = 165
    c: Distance(g19,g1) = 165
    c: Distance(g19,g2) = 30
    c: Distance(g18,g2) = 60
    c: Distance(g17,g2) = 90
    c: Distance(g16,g2) = 120
    c: Distance(g20,g1) = 255
    c: Distance(g21,g1) = 255
    c: Distance(g22,g1) = 255
    c: Distance(g23,g1) = 255
    c: Distance(g23,g2) = 30
    c: Distance(g22,g2) = 60
    c: Distance(g21,g2) = 90
    c: Distance(g20,g2) = 120
    c: Distance(g27,g1) = 210
    c: Distance(g26,g1) = 210
    c: Distance(g25,g1) = 210
    c: Distance(g24,g1) = 210
    c: Distance(g24,g2) = 120
    c: Distance(g25,g2) = 90
    c: Distance(g26,g2) = 60
    c: Distance(g27,g2) = 30
    c: Equal(g12,g13)
    c: Equal(g12,g14)
    c: Equal(g12,g15)
    c: Equal(g12,g27)
    c: Equal(g12,g26)
    c: Equal(g12,g25)
    c: Equal(g12,g24)
    c: Diameter(g12) = 4.5
    c: Diameter(g28) = 5
    c: Distance(g28,g1) = 14.02
    c: Diameter(g29) = 5
    c: Diameter(g30) = 5
    c: Symmetric(g29,g30,g-2)
    c: Distance(g34,g2) = 30
    c: Distance(g33,g2) = 60
    c: Distance(g32,g2) = 90
    c: Distance(g31,g2) = 120
    c: Distance(g31,g1) = 300
    c: Distance(g32,g1) = 300
    c: Distance(g33,g1) = 300
    c: Distance(g34,g1) = 300
    c: Equal(g35,g36)
    c: Equal(g35,g37)
    c: Equal(g35,g38)
    c: Diameter(g35) = 3.5
    c: Distance(g38,g2) = 30
    c: Distance(g37,g2) = 60
    c: Distance(g36,g2) = 90
    c: Distance(g35,g2) = 120
    c: Distance(g35,g1) = 345
    c: Distance(g36,g1) = 345
    c: Distance(g37,g1) = 345
    c: Distance(g38,g1) = 345
    c: Equal(g31,g32)
    c: Equal(g31,g33)
    c: Equal(g31,g34)
    c: Diameter(g31) = 4.5
    c: Distance(g39,g1) = 24.6
    c: Distance(g39,g0) = 135
    c: Equal(g40,g39)
    c: Diameter(g40) = 9.2
    c: Distance(g40,g0) = 135
    c: Distance(g40,g1) = 270
    c: Equal(g45,g44)
    c: Equal(g45,g46)
    c: Equal(g45,g41)
    c: Equal(g45,g42)
    c: Equal(g45,g43)
    c: Diameter(g45) = 9.2
    c: Distance(g43,g1) = 81
    c: Distance(g43,g42) = 51
    c: Distance(g43,g0) = 178
    c: Distance(g42,g0) = 178
    c: Distance(g43,g41) = 100
    c: Distance(g41,g0) = 178
    c: Distance(g44,g1) = 81
    c: Distance(g44,g43) = 165
    c: Distance(g44,g45) = 51
    c: Distance(g45,g42) = 165
    c: Distance(g46,g45) = 50
    c: Distance(g46,g41) = 165
    c: DistanceY(g-1,g28) = 155.6
    c: Symmetric(g28,g30,g-1)
    c: Diameter(g47) = 5
    c: Symmetric(g28,g47,g-2)
    c: PointOnObject(g56,g-1)
    c: Equal(g48, g49-g62) x14
    c: Diameter(g48) = 3.5
    c: Distance(g58,g3) = 14
    c: Distance(g58,g0) = 44
    c: Distance(g48,g3) = 14
    c: Distance(g58,g48) = 25.4
    c: Distance(g48,g49) = 25.4
    c: Distance(g49,g3) = 14
    c: Distance(g50,g49) = 25.4
    c: Distance(g50,g3) = 14
    c: Distance(g51,g50) = 25.4
    c: Distance(g51,g3) = 14
    c: Distance(g51,g57) = 25.4
    c: Distance(g57,g3) = 14
    c: Distance(g59,g0) = 44
    c: Distance(g59,g58) = 25.4
    c: Distance(g59,g60) = 25.4
    c: Distance(g60,g0) = 44
    c: Distance(g61,g0) = 44
    c: Distance(g62,g0) = 44
    c: Distance(g61,g60) = 25.4
    c: Distance(g48,g52) = 97
    c: Distance(g62,g58) = 97
    c: DistanceY(g52,g62) = 25.4
    c: DistanceY(g53,g52) = 25.4
    c: DistanceY(g54,g53) = 25.4
    c: DistanceY(g55,g54) = 25.4
    c: Distance(g53,g49) = 97
    c: Distance(g54,g50) = 97
    c: Distance(g51,g55) = 97
    c: Distance(g55,g56) = 25.4
    c: PointOnObject(g64,g-1)
    c: Diameter(g63) = 3.5
    c: Distance(g57,g65) = 25.4
    c: Diameter(g65) = 3.5
    c: PointOnObject(g65,g-1)
    c: PointOnObject(g63,g-1)
    c: Diameter(g64) = 3.5
    c: Distance(g64,g65) = 25.4
    c: Distance(g64,g63) = 25.4
FEATURE [Part::Extrusion] Extrude003  label="Base"
  Base = -> Sketch002
  Dir = (0,0,1)
  DirMode = 2
  FaceMakerClass = Part::FaceMakerBullseye
  LengthFwd = 6.5
  LengthRev = 0
  Placement = pos=(0,0,-164) rot=(0,0,1;0rad)
  Solid = true
  Symmetric = false
FEATURE [Part::Cone] Cone001
  Angle = 360
  AttacherType = Attacher::AttachEngine3D
  Height = 70.25
  Placement = pos=(-308,0,6.8e-14) rot=(0,1,0;1.5708rad)
  Radius1 = 1.75
  Radius2 = 15.23
FEATURE [Part::Cone] Cone002
  Angle = 360
  AttacherType = Attacher::AttachEngine3D
  Height = 70.25
  Placement = pos=(-308,0,6.8e-14) rot=(0,1,0;1.5708rad)
  Radius1 = 1.5
  Radius2 = 12.95
FEATURE [Part::Cut] Cut009  label="cone"
  Base = -> Cone001
  Tool = -> Cone002
FEATURE [Part::FeaturePython] Tube001  # WARN: FeaturePython — macro-defined, semantics opaque (R4)
  AttacherType = Attacher::AttachEngine3D
  Height = 3
  InnerRadius = 11
  OuterRadius = 13.75
  Placement = pos=(-237.75,0,-1.05e-13) rot=(0,-1,0;1.5708rad)
FEATURE [Part::FeaturePython] Tube002  # WARN: FeaturePython — macro-defined, semantics opaque (R4)
  AttacherType = Attacher::AttachEngine3D
  Height = 3
  InnerRadius = 12.5
  OuterRadius = 13.75
  Placement = pos=(-237.75,0,-1.05e-13) rot=(0,-1,0;1.5708rad)
FEATURE [Part::Cut] Cut010  label="cone_base"
  Base = -> Cut009
  Tool = -> Tube001
FEATURE [Sketcher::SketchObject] Sketch004
  FullyConstrained = true
  Placement = pos=(0,0,0) rot=(0.57735,0.57735,0.57735;2.0944rad)
  sketch-geometry (9):
    g0: LineSegment StartX=-1.4 StartY=12.5849 StartZ=0 EndX=1.4 EndY=12.5849 EndZ=0
    g1: LineSegment StartX=1.4 StartY=12.5849 StartZ=0 EndX=1.4 EndY=0.826805 EndZ=0
    g2: LineSegment StartX=1.4 StartY=0.826805 StartZ=0 EndX=12.027 EndY=-5.30872 EndZ=0
    g3: LineSegment StartX=12.027 StartY=-5.30872 StartZ=0 EndX=10.627 EndY=-7.73359 EndZ=0
    g4: LineSegment StartX=10.627 StartY=-7.73359 StartZ=0 EndX=0 EndY=-1.59807 EndZ=0
    g5: LineSegment StartX=0 StartY=-1.59807 StartZ=0 EndX=-10.5983 EndY=-7.71698 EndZ=0
    g6: LineSegment StartX=-10.5983 StartY=-7.71698 StartZ=0 EndX=-11.9983 EndY=-5.29211 EndZ=0
    g7: LineSegment StartX=-11.9983 StartY=-5.29211 StartZ=0 EndX=-1.4 EndY=0.826805 EndZ=0
    g8: LineSegment StartX=-1.4 StartY=0.826805 StartZ=0 EndX=-1.4 EndY=12.5849 EndZ=0
  constraints (27):
    c: Coincident(g1,g0)
    c: Vertical(g1)
    c: Coincident(g2,g1)
    c: Coincident(g3,g2)
    c: Coincident(g4,g3)
    c: PointOnObject(g4,g-2)
    c: Coincident(g5,g4)
    c: Coincident(g7,g6)
    c: Coincident(g8,g7)
    c: Coincident(g8,g0)
    c: Vertical(g8)
    c: Angle(g2,g1) = 2.0944
    c: Angle(g5,g4) = 2.0944
    c: Angle(g8,g7) = 2.0944
    c: Distance(g0) = 2.8
    c: Coincident(g6,g5)
    c: Distance(g6) = 2.8
    c: Symmetric(g0,g0,g-2)
    c: Distance(g3) = 2.8
    c: Perpendicular(g7,g6)
    c: Perpendicular(g3,g4)
    c: Perpendicular(g5,g6)
    c: Block(g0)
    c: Block(g8)
    c: Block(g1)
    c: Block(g7)
    c: Block(g4)
FEATURE [Part::Extrusion] Extrude004
  Base = -> Sketch004
  Dir = (1,2e-16,-2e-16)
  DirMode = 2
  FaceMakerClass = Part::FaceMakerBullseye
  LengthFwd = 3
  LengthRev = 0
  Placement = pos=(-240.75,0,0) rot=(0,0,1;0rad)
  Solid = true
  Symmetric = false
FEATURE [Part::FeaturePython] Tube003  # WARN: FeaturePython — macro-defined, semantics opaque (R4)
  AttacherType = Attacher::AttachEngine3D
  Height = 17
  InnerRadius = 2
  OuterRadius = 4.08
  Placement = pos=(-240.75,0,0) rot=(0,1,0;1.5708rad)
FEATURE [Part::FeaturePython] Tube004  # WARN: FeaturePython — macro-defined, semantics opaque (R4)
  AttacherType = Attacher::AttachEngine3D
  Height = 9.5
  InnerRadius = 2
  OuterRadius = 4.08
  Placement = pos=(-210.5,0,0) rot=(0,1,0;1.5708rad)
FEATURE [Part::FeaturePython] Tube005  # WARN: FeaturePython — macro-defined, semantics opaque (R4)
  AttacherType = Attacher::AttachEngine3D
  Height = 270
  InnerRadius = 1
  OuterRadius = 2
  Placement = pos=(-304.75,0,0) rot=(0,1,0;1.5708rad)
FEATURE [Part::MultiFuse] Fusion119  label="Inlet02"
  Shapes = -> [Tube002,Cut010,Extrude004,Tube003,Tube004]
FEATURE [Part::MultiFuse] Fusion120  label="Inlet"
  Placement = pos=(-10,0,-30) rot=(0,0,1;0rad)
  Shapes = -> [Fusion119,Tube005]
FEATURE [Part::Feature] Part__Feature044  label="Body"
  shape: bbox 15.5 x 16.75 x 29 mm, 21 faces (baked)
FEATURE [Part::Feature] Part__Feature045  label="Body001"
  Placement = pos=(0,0,2) rot=(0,0,1;0rad)
  shape: bbox 17.44 x 17.44 x 14.25 mm, 14 faces (baked)
FEATURE [Part::Feature] Part__Feature046  label="Body002"
  Placement = pos=(0,0,-5.5) rot=(0,0,1;0rad)
  shape: bbox 19 x 19 x 4.75 mm, 25 faces (baked)
FEATURE [Part::Feature] Part__Feature047  label="Body003"
  shape: bbox 16.75 x 16.75 x 0.9 mm, 4 faces (baked)
FEATURE [App::Part] PG7_Gland1
  Group = -> [Part__Feature044,Part__Feature045,Part__Feature046,Part__Feature047]
  Origin = -> Origin007
  Placement = pos=(-211.5,0,-30) rot=(0,1,0;4.71239rad)
FEATURE [Part::MultiFuse] Fusion121  label="Inlet_PG&"
  Placement = pos=(0,0,-10) rot=(0,0,1;0rad)
  Shapes = -> [Fusion120,PG7_Gland1]
FEATURE [Part::Feature] Part__Feature048  label="Board"
  shape: bbox 25.4 x 25.4 x 1.57 mm, 211 faces (baked)
FEATURE [Part::Feature] Part__Feature049  label="QFN24_4MM"
  Placement = pos=(12.1412,14.4526,1.57) rot=(0,0,1;3.92699rad)
  shape: bbox 5.657 x 5.657 x 0.9 mm, 172 faces (baked)
FEATURE [Part::Feature] Part__Feature050  label="Part 5"
  shape: bbox 0.48 x 0.6603 x 0.6 mm, 14 faces (baked)
FEATURE [Part::Feature] Part__Feature051  label="Part 6"
  shape: bbox 0.48 x 0.6603 x 0.6 mm, 14 faces (baked)
FEATURE [Part::Feature] Part__Feature052  label="Part 4"
  shape: bbox 0.48 x 0.6603 x 0.6 mm, 14 faces (baked)
FEATURE [Part::Feature] Part__Feature053  label="Part 3"
  shape: bbox 0.48 x 0.6603 x 0.6 mm, 14 faces (baked)
FEATURE [Part::Feature] Part__Feature054  label="Part 2"
  shape: bbox 0.48 x 0.6603 x 0.6 mm, 14 faces (baked)
FEATURE [Part::Feature] Part__Feature055  label="Part 1"
  shape: bbox 3 x 1.4 x 1 mm, 10 faces (baked)
FEATURE [Part::Feature] Part__Feature056  label="Pin1"
  shape: bbox 0.6224 x 1.252 x 1.252 mm, 37 faces (baked)
FEATURE [Part::Feature] Part__Feature057  label="Pin2"
  shape: bbox 0.6224 x 1.252 x 1.252 mm, 37 faces (baked)
FEATURE [Part::Feature] Part__Feature058  label="CeramicBody"
  shape: bbox 1.8 x 1.23 x 1.23 mm, 10 faces (baked)
FEATURE [Part::Feature] Part__Feature059  label="0603-NO (1)"
  Placement = pos=(23.241,6.223,1.57) rot=(0,0,1;0rad)
  shape: bbox 1.7 x 0.9 x 0.55 mm, 52 faces, 3 solids (baked)
FEATURE [Part::Feature] Part__Feature060  label="0603-NO (2)"
  Placement = pos=(13.3858,8.4328,1.57) rot=(0,0,1;0rad)
  shape: bbox 1.7 x 0.9 x 0.55 mm, 52 faces, 3 solids (baked)
FEATURE [Part::Feature] Part__Feature061  label="0603-NO (3)"
  Placement = pos=(1.905,18.923,1.57) rot=(0,0,1;3.14159rad)
  shape: bbox 1.7 x 0.9 x 0.55 mm, 52 faces, 3 solids (baked)
FEATURE [Part::Feature] Part__Feature062  label="Pin1 (1)"
  shape: bbox 0.6224 x 1.252 x 1.252 mm, 37 faces (baked)
FEATURE [Part::Feature] Part__Feature063  label="Pin2 (1)"
  shape: bbox 0.6224 x 1.252 x 1.252 mm, 37 faces (baked)
FEATURE [Part::Feature] Part__Feature064  label="CeramicBody (1)"
  shape: bbox 1.8 x 1.23 x 1.23 mm, 10 faces (baked)
FEATURE [Part::Feature] Part__Feature065  label="Pin1 (2)"
  shape: bbox 0.6224 x 1.252 x 1.252 mm, 37 faces (baked)
FEATURE [Part::Feature] Part__Feature066  label="Pin2 (2)"
  shape: bbox 0.6224 x 1.252 x 1.252 mm, 37 faces (baked)
FEATURE [Part::Feature] Part__Feature067  label="CeramicBody (2)"
  shape: bbox 1.8 x 1.23 x 1.23 mm, 10 faces (baked)
FEATURE [Part::Feature] Part__Feature068  label="CHIPLED_0603_NOOUTLINE"
  Placement = pos=(23.368,8.509,1.57) rot=(0,0,1;1.5708rad)
  shape: bbox 1.616 x 0.8 x 0.4 mm, 133 faces (baked)
FEATURE [Part::Feature] Part__Feature069  label="CHIPLED_0603_NOOUTLINE (1)"
  Placement = pos=(1.905,16.764,1.57) rot=(0,0,-1;1.5708rad)
  shape: bbox 1.616 x 0.8 x 0.4 mm, 133 faces (baked)
FEATURE [Part::Feature] Part__Feature070  label="JST_SH4"
  Placement = pos=(22.86,12.7,1.57) rot=(0,0,1;1.5708rad)
  shape: bbox 4.95 x 6 x 2.96 mm, 229 faces, 7 solids (baked)
FEATURE [Part::Feature] Part__Feature071  label="JST_SH4 (1)"
  Placement = pos=(2.54,12.7,1.57) rot=(0,0,-1;1.5708rad)
  shape: bbox 4.95 x 6 x 2.96 mm, 229 faces, 7 solids (baked)
FEATURE [Part::Feature] Part__Feature072  label="NEO3535_REVERSE"
  Placement = pos=(12.7,23.114,0) rot=(0,1,0;3.14159rad)
  shape: bbox 5.88 x 2.8 x 1.78 mm, 41 faces, 5 solids (baked)
FEATURE [Part::Feature] Part__Feature073  label="RESPACK_4X0603"
  Placement = pos=(22.86,18.415,1.57) rot=(0,0,1;3.14159rad)
  shape: bbox 3.2 x 1.6 x 0.61 mm, 172 faces (baked)
FEATURE [Part::Feature] Part__Feature074  label="SOT363"
  Placement = pos=(17.399,12.192,1.57) rot=(0,0,-1;1.5708rad)
  shape: bbox 2.208 x 2.208 x 1.121 mm, 178 faces, 4 solids (baked)
FEATURE [Sketcher::SketchObject] Sketch005
  FullyConstrained = true
  sketch-geometry (39):
    g0: LineSegment StartX=3 StartY=43.5 StartZ=0 EndX=3 EndY=34.5 EndZ=0
    g1: LineSegment StartX=3 StartY=34.5 StartZ=0 EndX=70.5 EndY=34.5 EndZ=0
    g2: LineSegment StartX=3 StartY=43.5 StartZ=0 EndX=10.5 EndY=43.5 EndZ=0
    g3: LineSegment StartX=3 StartY=71 StartZ=0 EndX=10.5 EndY=71 EndZ=0
    g4: LineSegment StartX=3 StartY=71 StartZ=0 EndX=3 EndY=80 EndZ=0
    g5: LineSegment StartX=70.5 StartY=80 StartZ=0 EndX=70.5 EndY=71 EndZ=0
    g6: LineSegment StartX=70.5 StartY=71 StartZ=0 EndX=62.5 EndY=71 EndZ=0
    g7: LineSegment StartX=62.5 StartY=71 StartZ=0 EndX=62.5 EndY=43 EndZ=0
    g8: LineSegment StartX=62.5 StartY=43 StartZ=0 EndX=70.5 EndY=43 EndZ=0
    g9: LineSegment StartX=70.5 StartY=43 StartZ=0 EndX=70.5 EndY=34.5 EndZ=0
    g10: GeomPoint X=70.5 Y=34.5 Z=0
    g11: GeomPoint X=70.5 Y=34.5 Z=0
    g12: GeomPoint X=70.5 Y=34.5 Z=0
    g13: GeomPoint X=70.5 Y=34.5 Z=0
    g14: GeomPoint X=70.5 Y=34.5 Z=0
    g15: LineSegment StartX=10.5 StartY=43.5 StartZ=0 EndX=10.5 EndY=71 EndZ=0
    g16: Circle CenterX=7.5 CenterY=75.5 CenterZ=0 NormalX=0 NormalY=0 NormalZ=1 AngleXU=0 Radius=1.6
    g17: Circle CenterX=7.5 CenterY=39 CenterZ=0 NormalX=0 NormalY=0 NormalZ=1 AngleXU=0 Radius=1.6
    g18: Circle CenterX=66.5 CenterY=39 CenterZ=0 NormalX=0 NormalY=0 NormalZ=1 AngleXU=0 Radius=1.6
    g19: Circle CenterX=66.5 CenterY=75.5 CenterZ=0 NormalX=0 NormalY=0 NormalZ=1 AngleXU=0 Radius=1.6
    g20: Circle CenterX=14.2 CenterY=70.46 CenterZ=0 NormalX=0 NormalY=0 NormalZ=1 AngleXU=0 Radius=1.6
    g21: Circle CenterX=38.54 CenterY=77.84 CenterZ=0 NormalX=0 NormalY=0 NormalZ=1 AngleXU=0 Radius=1.6
    g22: Circle CenterX=58.86 CenterY=77.84 CenterZ=0 NormalX=0 NormalY=0 NormalZ=1 AngleXU=0 Radius=1.6
    g23: Circle CenterX=38.54 CenterY=57.52 CenterZ=0 NormalX=0 NormalY=0 NormalZ=1 AngleXU=0 Radius=1.6
    g24: Circle CenterX=58.86 CenterY=57.52 CenterZ=0 NormalX=0 NormalY=0 NormalZ=1 AngleXU=0 Radius=1.6
    g25: Circle CenterX=38.54 CenterY=52.33 CenterZ=0 NormalX=0 NormalY=0 NormalZ=1 AngleXU=0 Radius=1.6
    g26: Circle CenterX=58.86 CenterY=52.33 CenterZ=0 NormalX=0 NormalY=0 NormalZ=1 AngleXU=0 Radius=1.6
    g27: Circle CenterX=38.54 CenterY=39.63 CenterZ=0 NormalX=0 NormalY=0 NormalZ=1 AngleXU=0 Radius=1.6
    g28: Circle CenterX=58.86 CenterY=39.63 CenterZ=0 NormalX=0 NormalY=0 NormalZ=1 AngleXU=0 Radius=1.6
    g29: Circle CenterX=30.43 CenterY=38.46 CenterZ=0 NormalX=0 NormalY=0 NormalZ=1 AngleXU=0 Radius=1.6
    g30: ArcOfCircle CenterX=48.54 CenterY=70.34 CenterZ=0 NormalX=0 NormalY=0 NormalZ=1 AngleXU=0 Radius=5 StartAngle=-9e-16 EndAngle=3.14159
    g31: ArcOfCircle CenterX=48.54 CenterY=42.63 CenterZ=0 NormalX=0 NormalY=0 NormalZ=1 AngleXU=0 Radius=5 StartAngle=3.14159 EndAngle=6.28319
    g32: LineSegment StartX=43.54 StartY=70.34 StartZ=0 EndX=43.54 EndY=42.63 EndZ=0
    g33: LineSegment StartX=53.54 StartY=42.63 StartZ=0 EndX=53.54 EndY=70.34 EndZ=0
    g34: ArcOfCircle CenterX=22.2 CenterY=70.34 CenterZ=0 NormalX=0 NormalY=0 NormalZ=1 AngleXU=0 Radius=5 StartAngle=0 EndAngle=3.14159
    g35: ArcOfCircle CenterX=22.2 CenterY=42.63 CenterZ=0 NormalX=0 NormalY=0 NormalZ=1 AngleXU=0 Radius=5 StartAngle=3.14159 EndAngle=6.28319
    g36: LineSegment StartX=17.2 StartY=70.34 StartZ=0 EndX=17.2 EndY=42.63 EndZ=0
    g37: LineSegment StartX=27.2 StartY=42.63 StartZ=0 EndX=27.2 EndY=70.34 EndZ=0
    g38: LineSegment StartX=3 StartY=80 StartZ=0 EndX=70.5 EndY=80 EndZ=0
  constraints (103):
    c: Vertical(g0)
    c: Coincident(g1,g0)
    c: Horizontal(g1)
    c: Coincident(g2,g0)
    c: Coincident(g4,g3)
    c: Vertical(g4)
    c: Coincident(g6,g5)
    c: Horizontal(g6)
    c: Coincident(g7,g6)
    c: Vertical(g7)
    c: Horizontal(g8)
    c: Horizontal(g2)
    c: Coincident(g10,g9)
    c: Coincident(g11,g1)
    c: Coincident(g12,g9)
    c: Coincident(g13,g1)
    c: Coincident(g14,g9)
    c: Coincident(g9,g1)
    c: Vertical(g9)
    c: Coincident(g15,g2)
    c: Coincident(g15,g3)
    c: Vertical(g15)
    c: Horizontal(g3)
    c: Vertical(g5)
    c: Coincident(g8,g9)
    c: Coincident(g7,g8)
    c: DistanceX(g8,g8) = 8
    c: Radius(g16) = 1.6
    c: DistanceY(g17) = 39
    c: Radius(g17) = 1.6
    c: DistanceX(g18) = 66.5
    c: DistanceY(g17,g18) = 0
    c: Radius(g18) = 1.6
    c: DistanceX(g19,g18) = 0
    c: Radius(g19) = 1.6
    c: DistanceY(g16) = 75.5
    c: DistanceY(g16,g19) = 0
    c: DistanceY(g3,g5) = 0
    c: Radius(g21) = 1.6
    c: DistanceY(g21,g22) = 0
    c: Radius(g22) = 1.6
    c: DistanceX(g21,g22) = 20.32
    c: DistanceX(g23,g21) = 0
    c: Radius(g23) = 1.6
    c: DistanceY(g23,g21) = 20.32
    c: DistanceY(g24,g23) = 0
    c: DistanceX(g24,g22) = 0
    c: Radius(g24) = 1.6
    c: DistanceX(g25,g23) = 0
    c: Radius(g25) = 1.6
    c: DistanceY(g25,g26) = 0
    c: DistanceX(g24,g26) = 0
    c: Radius(g26) = 1.6
    c: DistanceX(g25,g27) = 0
    c: DistanceX(g28,g26) = 0
    c: DistanceY(g27,g25) = 12.7
    c: DistanceY(g28,g27) = 0
    c: Radius(g28) = 1.6
    c: Radius(g27) = 1.6
    c: Radius(g29) = 1.6
    c: DistanceY(g29,g20) = 32
    c: Radius(g20) = 1.6
    c: Tangent(g30,g32) = -1.5708
    c: Tangent(g32,g31) = -1.5708
    c: Tangent(g31,g33) = -1.5708
    c: Tangent(g33,g30) = -1.5708
    c: Equal(g30,g31)
    c: Vertical(g32)
    c: DistanceY(g27,g31) = 3
    c: Radius(g30) = 5
    c: Tangent(g34,g36) = -1.5708
    c: Tangent(g36,g35) = -1.5708
    c: Tangent(g35,g37) = -1.5708
    c: Tangent(g37,g34) = -1.5708
    c: Equal(g34,g35)
    c: Vertical(g36)
    c: Radius(g34) = 5
    c: DistanceY(g34,g30) = 0
    c: DistanceY(g31,g35) = 0
    c: DistanceX(g16,g17) = 0
    c: DistanceX(g0,g3) = 0
    c: Coincident(g38,g4)
    c: Coincident(g38,g5)
    c: Horizontal(g38)
    c: DistanceX(g29) = 30.43
    c: DistanceX(g20) = 14.2
    c: DistanceY(g20) = 70.46
    c: DistanceX(g27) = 38.54
    c: DistanceY(g27) = 39.63
    c: DistanceY(g23) = 57.52
    c: DistanceY(g3,g16) = 4.5
    c: DistanceY(g16,g4) = 4.5
    c: DistanceY(g0,g17) = 4.5
    c: DistanceX(g0,g17) = 4.5
    c: DistanceX(g17) = 7.5
    c: DistanceY(g17,g0) = 4.5
    c: DistanceX(g16,g3) = 3
    c: DistanceX(g19,g5) = 4
    c: DistanceX(g6,g19) = 4
    c: DistanceY(g18,g8) = 4
    c: DistanceX(g25,g31) = 10
    c: DistanceY(g30,g21) = 7.5
    c: DistanceX(g20,g34) = 8
FEATURE [Part::Extrusion] Extrude005  label="sensorHold"
  Base = -> Sketch005
  Dir = (0,0,1)
  DirMode = 2
  FaceMakerClass = Part::FaceMakerBullseye
  LengthFwd = 4
  LengthRev = 0
  Placement = pos=(0,0,16) rot=(0,0,1;0rad)
  Solid = true
  Symmetric = false
FEATURE [Part::Fillet] Fillet006  label="sensorHold001"
  Base = -> Extrude005
  Edges = 12 edges r=3: [Edge1,Edge2,Edge5,Edge8,Edge11,Edge14,Edge17,Edge20,Edge23,Edge26,Edge29,Edge32]
FEATURE [App::Part] _603_NO  label="0603-NO"
  Group = -> [Part__Feature056,Part__Feature057,Part__Feature058]
  Origin = -> Origin010
  Placement = pos=(16.51,8.382,1.57) rot=(0,0,1;0rad)
FEATURE [App::Part] _6700497  label="36700497"
  Group = -> [Part__Feature050,Part__Feature051,Part__Feature052,Part__Feature053,Part__Feature054,Part__Feature055]
  Origin = -> Origin008
  Placement = pos=(0,0,0) rot=(0,0,1;3.14159rad)
FEATURE [App::Part] SOT23_5  label="SOT23-5"
  Group = -> [_6700497]
  Origin = -> Origin009
  Placement = pos=(2.54,6.985,1.57) rot=(0,0,1;3.14159rad)
FEATURE [App::Part] _805_NO  label="0805-NO"
  Group = -> [Part__Feature062,Part__Feature063,Part__Feature064]
  Origin = -> Origin011
  Placement = pos=(7.874,13.589,1.57) rot=(0,0,1;1.5708rad)
FEATURE [App::Part] _805_NO__1_  label="0805-NO (1)"
  Group = -> [Part__Feature065,Part__Feature066,Part__Feature067]
  Origin = -> Origin012
  Placement = pos=(12.827,6.223,1.57) rot=(0,0,1;3.14159rad)
FEATURE [App::Part] Packages
  Group = -> [Part__Feature049,SOT23_5,_603_NO,Part__Feature059,Part__Feature060,Part__Feature061,_805_NO,_805_NO__1_,Part__Feature068,Part__Feature069,Part__Feature070,Part__Feature071,Part__Feature072,Part__Feature073,Part__Feature074]
  Origin = -> Origin013
FEATURE [App::Part] Adafruit_I2C_QT_Rotary_Encoder_v2  label="gps"
  Group = -> [Part__Feature048,Packages,Sketch005,Extrude005,Fillet006]
  Origin = -> Origin014
  Placement = pos=(-421,98,65) rot=(0,0,1;0rad)
FEATURE [Part::Box] Box202  label="Cube202"
  AttacherType = Attacher::AttachEngine3D
  Height = 50
  Length = 60
  Placement = pos=(-450,39,25) rot=(0,0,1;0rad)
  Width = 90
FEATURE [Part::Box] Box203  label="Cube203"
  AttacherType = Attacher::AttachEngine3D
  Height = 46
  Length = 50
  Placement = pos=(-445,44,30) rot=(0,0,1;0rad)
  Width = 80
FEATURE [Part::Cut] Cut011
  Base = -> Box202
  Tool = -> Box203
FEATURE [Part::Feature] Part__Feature075  label="Body004"
  shape: bbox 15.5 x 16.75 x 29 mm, 21 faces (baked)
FEATURE [Part::Feature] Part__Feature076  label="Body005"
  Placement = pos=(0,0,2) rot=(0,0,1;0rad)
  shape: bbox 17.44 x 17.44 x 14.25 mm, 14 faces (baked)
FEATURE [Part::Feature] Part__Feature077  label="Body006"
  Placement = pos=(0,0,-5.5) rot=(0,0,1;0rad)
  shape: bbox 19 x 19 x 4.75 mm, 25 faces (baked)
FEATURE [Part::Feature] Part__Feature078  label="Body007"
  shape: bbox 16.75 x 16.75 x 0.9 mm, 4 faces (baked)
FEATURE [App::Part] PG7_Gland002
  Group = -> [Part__Feature075,Part__Feature076,Part__Feature077,Part__Feature078]
  Origin = -> Origin016
  Placement = pos=(-433,57,24) rot=(-0.258819,0.965926,0;3.14159rad)
FEATURE [Part::Box] Box204  label="Cube204"
  AttacherType = Attacher::AttachEngine3D
  Height = 4
  Length = 5
  Placement = pos=(-421,118,61) rot=(0,0,1;0rad)
  Width = 6
FEATURE [Part::Box] Box205  label="Cube205"
  AttacherType = Attacher::AttachEngine3D
  Height = 4
  Length = 5
  Placement = pos=(-400,118,61) rot=(0,0,1;0rad)
  Width = 6
FEATURE [Part::Box] Box206  label="Cube206"
  AttacherType = Attacher::AttachEngine3D
  Height = 4
  Length = 6
  Placement = pos=(-401,98,61) rot=(0,0,1;0rad)
  Width = 5
FEATURE [Part::Cylinder] Cylinder101
  Angle = 360
  AttacherType = Attacher::AttachEngine3D
  FirstAngle = 0
  Height = 15
  Placement = pos=(-47.7,61,61.5) rot=(0,0,1;0rad)
  Radius = 3
  SecondAngle = 0
FEATURE [Part::Cylinder] Cylinder102
  Angle = 360
  AttacherType = Attacher::AttachEngine3D
  FirstAngle = 0
  Height = 15
  Placement = pos=(-79.3,61,61.5) rot=(0,0,1;0rad)
  Radius = 3
  SecondAngle = 0
FEATURE [Part::Torus] Torus003
  Angle1 = -180
  Angle2 = 180
  Angle3 = 180
  AttacherType = Attacher::AttachEngine3D
  Placement = pos=(-63.5,61,76.5) rot=(0,0.707107,0.707107;3.14159rad)
  Radius1 = 15.8
  Radius2 = 3
FEATURE [Part::FeaturePython] Tube006  # WARN: FeaturePython — macro-defined, semantics opaque (R4)
  AttacherType = Attacher::AttachEngine3D
  Height = 10
  InnerRadius = 2
  OuterRadius = 4
  Placement = pos=(-76.3,61,59) rot=(0,-1,0;1.5708rad)
FEATURE [Part::FeaturePython] Tube007  # WARN: FeaturePython — macro-defined, semantics opaque (R4)
  AttacherType = Attacher::AttachEngine3D
  Height = 10
  InnerRadius = 2
  OuterRadius = 4
  Placement = pos=(-40.7,61,59) rot=(0,-1,0;1.5708rad)
FEATURE [App::Part] Part002  label="pipe_hold"
  Group = -> [Torus003,Cylinder101,Cylinder102,Tube006,Tube007]
  Origin = -> Origin038
  Placement = pos=(-481,40,-66) rot=(0,0,1;4.71239rad)
FEATURE [Part::Box] Box207  label="Cube207"
  AttacherType = Attacher::AttachEngine3D
  Height = 12
  Length = 10
  Placement = pos=(-425,84,13) rot=(0,0,1;0rad)
  Width = 6.5
FEATURE [Part::Box] Box208  label="Cube208"
  AttacherType = Attacher::AttachEngine3D
  Height = 5.5
  Length = 10
  Placement = pos=(-425,93.5,19) rot=(1,0,0;1.5708rad)
  Width = 6
FEATURE [Part::Box] Box209  label="Cube209"
  AttacherType = Attacher::AttachEngine3D
  Height = 5.5
  Length = 10
  Placement = pos=(-425,119.5,19) rot=(1,0,0;1.5708rad)
  Width = 6
FEATURE [Part::Box] Box210  label="Cube210"
  AttacherType = Attacher::AttachEngine3D
  Height = 12
  Length = 10
  Placement = pos=(-425,117,13) rot=(0,0,1;0rad)
  Width = 6.5
FEATURE [Part::MultiFuse] Fusion122
  Placement = pos=(-15,0,0) rot=(0,0,1;0rad)
  Shapes = -> [Box207,Box208,Box209,Box210,Part002]
FEATURE [Part::Box] Box211  label="Cube211"
  AttacherType = Attacher::AttachEngine3D
  Height = 12
  Length = 10
  Placement = pos=(-425,84,13) rot=(0,0,1;0rad)
  Width = 6.5
FEATURE [Part::Box] Box212  label="Cube212"
  AttacherType = Attacher::AttachEngine3D
  Height = 5.5
  Length = 10
  Placement = pos=(-425,93.5,19) rot=(1,0,0;1.5708rad)
  Width = 6
FEATURE [Part::Box] Box213  label="Cube213"
  AttacherType = Attacher::AttachEngine3D
  Height = 5.5
  Length = 10
  Placement = pos=(-425,119.5,19) rot=(1,0,0;1.5708rad)
  Width = 6
FEATURE [Part::Box] Box214  label="Cube214"
  AttacherType = Attacher::AttachEngine3D
  Height = 12
  Length = 10
  Placement = pos=(-425,117,13) rot=(0,0,1;0rad)
  Width = 6.5
FEATURE [Part::Cylinder] Cylinder103
  Angle = 360
  AttacherType = Attacher::AttachEngine3D
  FirstAngle = 0
  Height = 15
  Placement = pos=(-47.7,61,61.5) rot=(0,0,1;0rad)
  Radius = 3
  SecondAngle = 0
FEATURE [Part::Cylinder] Cylinder104
  Angle = 360
  AttacherType = Attacher::AttachEngine3D
  FirstAngle = 0
  Height = 15
  Placement = pos=(-79.3,61,61.5) rot=(0,0,1;0rad)
  Radius = 3
  SecondAngle = 0
FEATURE [Part::Torus] Torus004
  Angle1 = -180
  Angle2 = 180
  Angle3 = 180
  AttacherType = Attacher::AttachEngine3D
  Placement = pos=(-63.5,61,76.5) rot=(0,0.707107,0.707107;3.14159rad)
  Radius1 = 15.8
  Radius2 = 3
FEATURE [Part::FeaturePython] Tube008  # WARN: FeaturePython — macro-defined, semantics opaque (R4)
  AttacherType = Attacher::AttachEngine3D
  Height = 10
  InnerRadius = 2
  OuterRadius = 4
  Placement = pos=(-76.3,61,59) rot=(0,-1,0;1.5708rad)
FEATURE [Part::FeaturePython] Tube009  # WARN: FeaturePython — macro-defined, semantics opaque (R4)
  AttacherType = Attacher::AttachEngine3D
  Height = 10
  InnerRadius = 2
  OuterRadius = 4
  Placement = pos=(-40.7,61,59) rot=(0,-1,0;1.5708rad)
FEATURE [App::Part] Part003  label="pipe_hold001"
  Group = -> [Torus004,Cylinder103,Cylinder104,Tube008,Tube009]
  Origin = -> Origin039
  Placement = pos=(-481,40,-66) rot=(0,0,1;4.71239rad)
FEATURE [Part::MultiFuse] Fusion123
  Placement = pos=(15,0,0) rot=(0,0,1;0rad)
  Shapes = -> [Box211,Box212,Box213,Box214,Part003]
FEATURE [Part::MultiFuse] Fusion124  label="Holder_Bottom"
  Shapes = -> [Box204,Box205,Box206,Fusion122,Fusion123,Cut011]
FEATURE [Part::Cylinder] Cylinder105
  Angle = 360
  AttacherType = Attacher::AttachEngine3D
  FirstAngle = 0
  Height = 10
  Placement = pos=(-398.15,100.55,100) rot=(0,0,1;0rad)
  Radius = 1.25
  SecondAngle = 0
FEATURE [Part::Cylinder] Cylinder106
  Angle = 360
  AttacherType = Attacher::AttachEngine3D
  FirstAngle = 0
  Height = 10
  Placement = pos=(-418.46,100.54,100) rot=(0,0,1;0rad)
  Radius = 1.25
  SecondAngle = 0
FEATURE [Part::Cylinder] Cylinder107
  Angle = 360
  AttacherType = Attacher::AttachEngine3D
  FirstAngle = 0
  Height = 10
  Placement = pos=(-418.46,120.86,100) rot=(0,0,1;0rad)
  Radius = 1.25
  SecondAngle = 0
FEATURE [Part::Cylinder] Cylinder108
  Angle = 360
  AttacherType = Attacher::AttachEngine3D
  FirstAngle = 0
  Height = 10
  Placement = pos=(-398.14,120.86,100) rot=(0,0,1;0rad)
  Radius = 1.25
  SecondAngle = 0
FEATURE [Part::MultiFuse] Fusion125  label="m2_cylinder"
  Placement = pos=(0,0,-43) rot=(0,0,1;0rad)
  Shapes = -> [Cylinder105,Cylinder106,Cylinder107,Cylinder108]
FEATURE [Part::Cut] Cut012  label="Holder_btm"
  Base = -> Fusion124
  Tool = -> Fusion125
FEATURE [Part::Fillet] Fillet007
  Base = -> Cut012
  Edges = 8 edges r=4: [Edge7,Edge8,Edge9,Edge10,Edge61,Edge63,Edge64,Edge66]
FEATURE [Part::Fillet] Fillet008
  Base = -> Fillet007
  Edges = 72 edges r=1: [Edge5,Edge6,Edge7,Edge8,Edge13,Edge14,Edge15,Edge16,Edge17,Edge18,Edge19,Edge23,Edge24,Edge25,Edge26,Edge27,Edge28,Edge29,Edge34,Edge35,Edge36,Edge37,Edge38,Edge39,Edge40,Edge44,Edge45,Edge46,Edge59,Edge60,Edge61,Edge64,Edge65,Edge67,Edge68,Edge87,Edge89,Edge93,Edge94,Edge95,Edge96,Edge97,Edge98,+29 more]
FEATURE [App::Part] Part001  label="GPS_holder"
  Group = -> [Adafruit_I2C_QT_Rotary_Encoder_v2,PG7_Gland002,Box207,Box202,Box205,Box206,Box203,Box204,Part002,Part003,Cut011,Fusion123,Fusion124,Fusion122,Fusion125,Cylinder107,Cylinder105,Cylinder108,Cylinder106,Box208,Box209,Box211,Box210,Box213,Box214,Box212,Cut012,Fillet007,Fillet008]
  Origin = -> Origin015
FEATURE [Part::Fillet] Fillet009  label="Base_fillet"
  Base = -> Extrude003
  Edges = 4 edges r=30: [Edge1,Edge2,Edge5,Edge8]
FEATURE [Part::Box] Box215  label="Cube215"
  AttacherType = Attacher::AttachEngine3D
  Height = 75
  Length = 85
  Placement = pos=(90,15,0) rot=(0,0,1;0rad)
  Width = 100
FEATURE [Part::Feature] Part__Feature079  label="CUI_VGS-35C-12"
  shape: bbox 82 x 30 x 99 mm, 244 faces (baked)
FEATURE [Part::Feature] Part__Feature080  label="CUI_VGS-35C-013"
  shape: bbox 49.5 x 17 x 16 mm, 923 faces (baked)
FEATURE [Part::Feature] Part__Feature081  label="CUI_VGS-35C-014"
  shape: bbox 4.624 x 1.433 x 4.618 mm, 8 faces (baked)
FEATURE [Part::Feature] Part__Feature082  label="CUI_VGS-35C-015"
  shape: bbox 5.413 x 8.147 x 5.413 mm, 53 faces (baked)
FEATURE [Part::Feature] Part__Feature083  label="CUI_VGS-35C-016"
  shape: bbox 5.8 x 4.834 x 5.8 mm, 40 faces (baked)
FEATURE [Part::Feature] Part__Feature084  label="CUI_VGS-35C-017"
  shape: bbox 3 x 7.6 x 3.04 mm, 12 faces (baked)
FEATURE [Part::Feature] Part__Feature085  label="CUI_VGS-35C-018"
  shape: bbox 81 x 29 x 76 mm, 406 faces (baked)
FEATURE [Part::Feature] Part__Feature086  label="CUI_VGS-35C-019"
  shape: bbox 7 x 0.55 x 7 mm, 6 faces (baked)
FEATURE [Part::Feature] Part__Feature087  label="CUI_VGS-35C-020"
  shape: bbox 6.811 x 11.02 x 8.111 mm, 138 faces (baked)
FEATURE [Part::Feature] Part__Feature088  label="CUI_VGS-35C-021"
  shape: bbox 78.62 x 1.622 x 92.02 mm, 385 faces (baked)
FEATURE [App::Part] CUI_VGS_35C_12  label="CUI_VGS-35C-022"
  Group = -> [Part__Feature079,Part__Feature080,Part__Feature081,Part__Feature082,Part__Feature083,Part__Feature084,Part__Feature085,Part__Feature086,Part__Feature087,Part__Feature088]
  Origin = -> Origin041
  Placement = pos=(131,66,-140) rot=(1,0,0;1.5708rad)
FEATURE [Part::Feature] Part__Feature089  label="CUI_VGS-50C-5"
  shape: bbox 78.62 x 1.622 x 92.02 mm, 385 faces (baked)
FEATURE [Part::Feature] Part__Feature090  label="CUI_VGS-50C-006"
  shape: bbox 82 x 30 x 99 mm, 244 faces (baked)
FEATURE [Part::Feature] Part__Feature091  label="CUI_VGS-50C-007"
  shape: bbox 81 x 29 x 76 mm, 406 faces (baked)
FEATURE [Part::Feature] Part__Feature092  label="CUI_VGS-50C-008"
  shape: bbox 6.811 x 11.02 x 8.111 mm, 138 faces (baked)
FEATURE [Part::Feature] Part__Feature093  label="CUI_VGS-50C-009"
  shape: bbox 3 x 7.6 x 3.04 mm, 12 faces (baked)
FEATURE [Part::Feature] Part__Feature094  label="CUI_VGS-50C-010"
  shape: bbox 5.413 x 8.147 x 5.413 mm, 53 faces (baked)
FEATURE [Part::Feature] Part__Feature095  label="CUI_VGS-50C-011"
  shape: bbox 7 x 0.55 x 7 mm, 6 faces (baked)
FEATURE [Part::Feature] Part__Feature096  label="CUI_VGS-50C-012"
  shape: bbox 4.624 x 1.433 x 4.618 mm, 8 faces (baked)
FEATURE [Part::Feature] Part__Feature097  label="CUI_VGS-50C-013"
  shape: bbox 49.5 x 17 x 16 mm, 923 faces (baked)
FEATURE [Part::Feature] Part__Feature098  label="CUI_VGS-50C-014"
  shape: bbox 5.8 x 4.834 x 5.8 mm, 40 faces (baked)
FEATURE [App::Part] CUI_VGS_50C_5  label="CUI_VGS-50C-015"
  Group = -> [Part__Feature089,Part__Feature090,Part__Feature091,Part__Feature092,Part__Feature093,Part__Feature094,Part__Feature095,Part__Feature096,Part__Feature097,Part__Feature098]
  Origin = -> Origin042
  Placement = pos=(131,88,-85) rot=(1,0,0;1.5708rad)
FEATURE [Sketcher::SketchObject] Sketch006
  FullyConstrained = true
  sketch-geometry (22):
    g0: LineSegment StartX=78.5 StartY=133.75 StartZ=0 EndX=78.5 EndY=118.75 EndZ=0
    g1: LineSegment StartX=78.5 StartY=118.75 StartZ=0 EndX=175 EndY=118.75 EndZ=0
    g2: LineSegment StartX=175 StartY=118.75 StartZ=0 EndX=175 EndY=6.15 EndZ=0
    g3: LineSegment StartX=175 StartY=6.15 StartZ=0 EndX=78.5 EndY=6.15 EndZ=0
    g4: LineSegment StartX=78.5 StartY=6.15 StartZ=0 EndX=78.5 EndY=-8.85 EndZ=0
    g5: LineSegment StartX=78.5 StartY=-8.85 StartZ=0 EndX=189 EndY=-8.85 EndZ=0
    g6: LineSegment StartX=189 StartY=-8.85 StartZ=0 EndX=189 EndY=133.75 EndZ=0
    g7: LineSegment StartX=189 StartY=133.75 StartZ=0 EndX=78.5 EndY=133.75 EndZ=0
    g8: Circle CenterX=84 CenterY=0 CenterZ=0 NormalX=0 NormalY=0 NormalZ=1 AngleXU=0 Radius=1.75
    g9: Circle CenterX=104.8 CenterY=0 CenterZ=0 NormalX=0 NormalY=0 NormalZ=1 AngleXU=0 Radius=1.75
    g10: Circle CenterX=130.2 CenterY=0 CenterZ=0 NormalX=0 NormalY=0 NormalZ=1 AngleXU=0 Radius=1.75
    g11: Circle CenterX=155.6 CenterY=0 CenterZ=0 NormalX=0 NormalY=0 NormalZ=1 AngleXU=0 Radius=1.75
    g12: Circle CenterX=181 CenterY=0 CenterZ=0 NormalX=0 NormalY=0 NormalZ=1 AngleXU=0 Radius=1.75
    g13: Circle CenterX=181 CenterY=25.4 CenterZ=0 NormalX=0 NormalY=0 NormalZ=1 AngleXU=0 Radius=1.75
    g14: Circle CenterX=181 CenterY=50.8 CenterZ=0 NormalX=0 NormalY=0 NormalZ=1 AngleXU=0 Radius=1.75
    g15: Circle CenterX=181 CenterY=76.2 CenterZ=0 NormalX=0 NormalY=0 NormalZ=1 AngleXU=0 Radius=1.75
    g16: Circle CenterX=181 CenterY=101.6 CenterZ=0 NormalX=0 NormalY=0 NormalZ=1 AngleXU=0 Radius=1.75
    g17: Circle CenterX=181 CenterY=127 CenterZ=0 NormalX=0 NormalY=0 NormalZ=1 AngleXU=0 Radius=1.75
    g18: Circle CenterX=155.6 CenterY=127 CenterZ=0 NormalX=0 NormalY=0 NormalZ=1 AngleXU=0 Radius=1.75
    g19: Circle CenterX=130.2 CenterY=127 CenterZ=0 NormalX=0 NormalY=0 NormalZ=1 AngleXU=0 Radius=1.75
    g20: Circle CenterX=104.8 CenterY=127 CenterZ=0 NormalX=0 NormalY=0 NormalZ=1 AngleXU=0 Radius=1.75
    g21: Circle CenterX=84 CenterY=127 CenterZ=0 NormalX=0 NormalY=0 NormalZ=1 AngleXU=0 Radius=1.75
  constraints (60):
    c: Vertical(g0)
    c: Coincident(g1,g0)
    c: Horizontal(g1)
    c: Vertical(g2)
    c: Horizontal(g3)
    c: Vertical(g4)
    c: Horizontal(g5)
    c: Coincident(g6,g5)
    c: Vertical(g6)
    c: Coincident(g7,g0)
    c: Horizontal(g7)
    c: Distance(g0) = 15
    c: Distance(g4) = 15
    c: Coincident(g2,g1)
    c: Coincident(g7,g6)
    c: Coincident(g3,g4)
    c: Coincident(g4,g5)
    c: Distance(g0,g-2) = 78.5
    c: Distance(g3,g-2) = 78.5
    c: Distance(g2,g-2) = 175
    c: Distance(g5,g-2) = 189
    c: Distance(g0,g-1) = 118.75
    c: Distance(g3,g-1) = 6.15
    c: Coincident(g2,g3)
    c: PointOnObject(g8,g-1)
    c: PointOnObject(g9,g-1)
    c: PointOnObject(g10,g-1)
    c: PointOnObject(g11,g-1)
    c: PointOnObject(g12,g-1)
    c: Equal(g8, g9-g12) x4
    c: Diameter(g8) = 3.5
    c: Distance(g12,g6) = 8
    c: Distance(g12,g11) = 25.4
    c: Distance(g10,g11) = 25.4
    c: Distance(g10,g9) = 25.4
    c: Distance(g8,g9) = 20.8
    c: Equal(g13, g14-g17) x4
    c: Diameter(g13) = 3.5
    c: Distance(g13,g6) = 8
    c: Distance(g13,g12) = 25.4
    c: Distance(g14,g6) = 8
    c: Distance(g14,g13) = 25.4
    c: Distance(g15,g14) = 25.4
    c: Distance(g15,g6) = 8
    c: Distance(g16,g6) = 8
    c: Distance(g15,g16) = 25.4
    c: Distance(g17,g16) = 25.4
    c: Distance(g17,g6) = 8
    c: Equal(g18,g19)
    c: Equal(g18,g20)
    c: Equal(g18,g21)
    c: Diameter(g18) = 3.5
    c: Distance(g17,g18) = 25.4
    c: Distance(g19,g18) = 25.4
    c: Distance(g20,g19) = 25.4
    c: Distance(g20,g21) = 20.8
    c: Distance(g18,g-1) = 127
    c: Distance(g19,g-1) = 127
    c: Distance(g20,g-1) = 127
    c: Distance(g21,g-1) = 127
FEATURE [Part::Extrusion] Extrude006  label="power_base"
  Base = -> Sketch006
  Dir = (0,0,1)
  DirMode = 2
  FaceMakerClass = Part::FaceMakerBullseye
  LengthFwd = 10
  LengthRev = 0
  Placement = pos=(0,0,-157) rot=(0,0,1;0rad)
  Solid = true
  Symmetric = false
FEATURE [Sketcher::SketchObject] Sketch007
  FullyConstrained = true
  Placement = pos=(200,0,0) rot=(0.57735,0.57735,0.57735;2.0944rad)
  sketch-geometry (16):
    g0: LineSegment StartX=19 StartY=-147 StartZ=0 EndX=19 EndY=-133 EndZ=0
    g1: LineSegment StartX=19 StartY=-133 StartZ=0 EndX=40 EndY=-133 EndZ=0
    g2: LineSegment StartX=56 StartY=-147 StartZ=0 EndX=19 EndY=-147 EndZ=0
    g3: LineSegment StartX=40 StartY=-78 StartZ=0 EndX=56 EndY=-78 EndZ=0
    g4: LineSegment StartX=56 StartY=-78 StartZ=0 EndX=56 EndY=-147 EndZ=0
    g5: LineSegment StartX=94.75 StartY=-147 StartZ=0 EndX=94.75 EndY=-131.25 EndZ=0
    g6: LineSegment StartX=94.75 StartY=-131.25 StartZ=0 EndX=115.65 EndY=-131.25 EndZ=0
    g7: LineSegment StartX=129.65 StartY=-147 StartZ=0 EndX=94.75 EndY=-147 EndZ=0
    g8: LineSegment StartX=115.65 StartY=-78 StartZ=0 EndX=129.65 EndY=-78 EndZ=0
    g9: LineSegment StartX=129.65 StartY=-78 StartZ=0 EndX=129.65 EndY=-147 EndZ=0
    g10: Circle CenterX=26.1 CenterY=-141.25 CenterZ=0 NormalX=0 NormalY=0 NormalZ=1 AngleXU=0 Radius=1.5
    g11: Circle CenterX=100.5 CenterY=-141.25 CenterZ=0 NormalX=0 NormalY=0 NormalZ=1 AngleXU=0 Radius=1.5
    g12: Circle CenterX=48.1 CenterY=-86.25 CenterZ=0 NormalX=0 NormalY=0 NormalZ=1 AngleXU=0 Radius=1.5
    g13: Circle CenterX=122.5 CenterY=-86.25 CenterZ=0 NormalX=0 NormalY=0 NormalZ=1 AngleXU=0 Radius=1.5
    g14: LineSegment StartX=40 StartY=-78 StartZ=0 EndX=40 EndY=-133 EndZ=0
    g15: LineSegment StartX=115.65 StartY=-78 StartZ=0 EndX=115.65 EndY=-131.25 EndZ=0
  constraints (48):
    c: Vertical(g0)
    c: Coincident(g1,g0)
    c: Horizontal(g1)
    c: Coincident(g2,g0)
    c: Horizontal(g3)
    c: Coincident(g4,g3)
    c: Vertical(g4)
    c: Vertical(g5)
    c: Coincident(g6,g5)
    c: Coincident(g7,g5)
    c: Horizontal(g8)
    c: Coincident(g9,g8)
    c: Vertical(g9)
    c: Distance(g0,g-2) = 19
    c: DistanceY(g0,g0) = 14
    c: Distance(g0,g-1) = 147
    c: Distance(g3,g4) = 69
    c: Horizontal(g7)
    c: Distance(g5,g-1) = 147
    c: Distance(g5,g-2) = 94.75
    c: Distance(g9,g8) = 69
    c: Diameter(g10) = 3
    c: Distance(g10,g-2) = 26.1
    c: Distance(g10,g-1) = 141.25
    c: Distance(g11,g-1) = 141.25
    c: Diameter(g11) = 3
    c: Distance(g11,g10) = 74.4
    c: Equal(g12,g13)
    c: Diameter(g12) = 3
    c: Distance(g12,g-2) = 48.1
    c: Distance(g12,g-1) = 86.25
    c: Distance(g13,g-1) = 86.25
    c: Distance(g13,g12) = 74.4
    c: Coincident(g14,g3)
    c: Vertical(g14)
    c: Coincident(g1,g14)
    c: Coincident(g2,g4)
    c: Horizontal(g2)
    c: Distance(g2) = 37
    c: Distance(g1) = 21
    c: Coincident(g15,g8)
    c: Vertical(g15)
    c: Coincident(g15,g6)
    c: Horizontal(g6)
    c: Distance(g5) = 15.75
    c: Coincident(g9,g7)
    c: Distance(g7) = 34.9
    c: Distance(g6) = 20.9
FEATURE [Part::Extrusion] Extrude007  label="power_hold"
  Base = -> Sketch007
  Dir = (1,0,0)
  DirMode = 2
  FaceMakerClass = Part::FaceMakerBullseye
  LengthFwd = 10
  LengthRev = 0
  Placement = pos=(-15,0,0) rot=(0,0,1;0rad)
  Reversed = true
  Solid = true
  Symmetric = false
FEATURE [Part::MultiFuse] Fusion126  label="Power_holder_raw"
  Shapes = -> [Extrude006,Extrude007]
FEATURE [Part::Fillet] Fillet010  label="Power_Holder"
  Base = -> Fusion126
  Edges = 43 edges: [Edge1 r=4,Edge2 r=4,Edge5 r=4,Edge6 r=1,Edge7 r=1,Edge8 r=4,Edge9 r=1,Edge10 r=1,Edge11 r=1,Edge12 r=1,Edge14 r=1,Edge15 r=1,Edge30 r=1,Edge31 r=1,Edge33 r=1,Edge35 r=4,Edge37 r=4,Edge39 r=4,Edge53 r=4,Edge54 r=4,Edge57 r=4,Edge58 r=4,Edge77 r=4,Edge78 r=1,Edge80 r=1,Edge82 r=1,Edge83 r=1,Edge86 r=4,Edge88 r=4,Edge91 r=1,Edge93 r=1,Edge94 r=1,Edge97 r=4,Edge99 r=1,Edge100 r=1,Edge101 r=1,Edge104 r=1,Edge105 r=1,Edge106 r=1,Edge109 r=4,Edge110 r=4,Edge113 r=4,Edge114 r=4]
FEATURE [App::Part] Part004  label="Power_supply"
  Group = -> [Box215,CUI_VGS_35C_12,CUI_VGS_50C_5,Extrude007,Extrude006,Sketch006,Sketch007,Fusion126,Fillet010]
  Origin = -> Origin040
FEATURE [Part::Cone] Cone005
  Angle = 360
  AttacherType = Attacher::AttachEngine3D
  Height = 82.25
  Placement = pos=(-308,0,6.8e-14) rot=(0,1,0;1.5708rad)
  Radius1 = 0.5
  Radius2 = 19
FEATURE [Part::Cone] Cone006
  Angle = 360
  AttacherType = Attacher::AttachEngine3D
  Height = 82.25
  Placement = pos=(-308,0,6.8e-14) rot=(0,1,0;1.5708rad)
  Radius1 = 0
  Radius2 = 16.25
FEATURE [Part::Cut] Cut015  label="cone002"
  Base = -> Cone005
  Placement = pos=(-10,0,0) rot=(0,0,1;0rad)
  Tool = -> Cone006
FEATURE [Part::Sphere] Sphere
  Angle1 = -90
  Angle2 = 90
  Angle3 = 360
  AttacherType = Attacher::AttachEngine3D
  Placement = pos=(-318,0,0) rot=(0,0,1;0rad)
  Radius = 0.5
FEATURE [Part::MultiFuse] Fusion127
  Placement = pos=(-9,0,-40) rot=(0,0,1;0rad)
  Shapes = -> [Cut015,Sphere]
FEATURE [Sketcher::SketchObject] Sketch008
  FullyConstrained = true
  Placement = pos=(-244.75,0,0) rot=(0.57735,0.57735,0.57735;2.0944rad)
  sketch-geometry (16):
    g0: ArcOfCircle CenterX=0 CenterY=-40 CenterZ=0 NormalX=0 NormalY=0 NormalZ=1 AngleXU=0 Radius=16.25 StartAngle=3.0182 EndAngle=3.26498
    g1: ArcOfCircle CenterX=0 CenterY=-40 CenterZ=0 NormalX=0 NormalY=0 NormalZ=1 AngleXU=0 Radius=16.25 StartAngle=6.1598 EndAngle=6.40658
    g2: ArcOfCircle CenterX=0 CenterY=-40 CenterZ=0 NormalX=0 NormalY=0 NormalZ=1 AngleXU=0 Radius=16.25 StartAngle=4.589 EndAngle=4.83578
    g3: ArcOfCircle CenterX=0 CenterY=-40 CenterZ=0 NormalX=0 NormalY=0 NormalZ=1 AngleXU=0 Radius=16.25 StartAngle=1.44741 EndAngle=1.69419
    g4: ArcOfCircle CenterX=0 CenterY=-40 CenterZ=0 NormalX=0 NormalY=0 NormalZ=1 AngleXU=0 Radius=14.2 StartAngle=6.14187 EndAngle=6.4245
    g5: ArcOfCircle CenterX=0 CenterY=-40 CenterZ=0 NormalX=0 NormalY=0 NormalZ=1 AngleXU=0 Radius=14.2 StartAngle=4.57107 EndAngle=4.8537
    g6: ArcOfCircle CenterX=0 CenterY=-40 CenterZ=0 NormalX=0 NormalY=0 NormalZ=1 AngleXU=0 Radius=14.2 StartAngle=3.00028 EndAngle=3.28291
    g7: ArcOfCircle CenterX=0 CenterY=-40 CenterZ=0 NormalX=0 NormalY=0 NormalZ=1 AngleXU=0 Radius=14.2 StartAngle=1.42948 EndAngle=1.71211
    g8: LineSegment StartX=-2 StartY=-54.0584 StartZ=0 EndX=-2 EndY=-56.1265 EndZ=0
    g9: LineSegment StartX=2 StartY=-56.1265 StartZ=0 EndX=2 EndY=-54.0584 EndZ=0
    g10: LineSegment StartX=14.0584 StartY=-42 StartZ=0 EndX=16.1265 EndY=-42 EndZ=0
    g11: LineSegment StartX=14.0584 StartY=-38 StartZ=0 EndX=16.1265 EndY=-38 EndZ=0
    g12: LineSegment StartX=-16.1265 StartY=-42 StartZ=0 EndX=-14.0584 EndY=-42 EndZ=0
    g13: LineSegment StartX=-16.1265 StartY=-38 StartZ=0 EndX=-14.0584 EndY=-38 EndZ=0
    g14: LineSegment StartX=-2 StartY=-23.8735 StartZ=0 EndX=-2 EndY=-25.9416 EndZ=0
    g15: LineSegment StartX=2 StartY=-25.9416 StartZ=0 EndX=2 EndY=-23.8735 EndZ=0
  constraints (49):
    c: PointOnObject(g0,g-2)
    c: Coincident(g1,g0)
    c: Coincident(g2,g0)
    c: Coincident(g3,g0)
    c: DistanceY(g0) = -40
    c: Equal(g0,g2)
    c: Equal(g0,g1)
    c: Equal(g0,g3)
    c: Diameter(g0) = 32.5
    c: DistanceX(g2,g0) = 2
    c: DistanceX(g0,g2) = 2
    c: DistanceY(g0,g0) = 2
    c: DistanceY(g0,g0) = 2
    c: Vertical(g2,g3)
    c: Vertical(g3,g2)
    c: Horizontal(g1,g0)
    c: Horizontal(g1,g0)
    c: Coincident(g4,g0)
    c: Coincident(g5,g0)
    c: Coincident(g6,g0)
    c: Coincident(g7,g0)
    c: Horizontal(g0,g6)
    c: Horizontal(g6,g0)
    c: Horizontal(g4,g1)
    c: Horizontal(g1,g4)
    c: Vertical(g2,g5)
    c: Vertical(g2,g5)
    c: Vertical(g3,g7)
    c: Vertical(g3,g7)
    c: Equal(g6,g7)
    c: Equal(g6,g4)
    c: Equal(g6,g5)
    c: Diameter(g6) = 28.4
    c: Coincident(g8,g5)
    c: Coincident(g8,g2)
    c: Coincident(g9,g2)
    c: Coincident(g9,g5)
    c: Coincident(g10,g4)
    c: Coincident(g10,g1)
    c: Coincident(g11,g4)
    c: Coincident(g11,g1)
    c: Coincident(g12,g0)
    c: Coincident(g12,g6)
    c: Coincident(g13,g0)
    c: Coincident(g13,g6)
    c: Coincident(g14,g3)
    c: Coincident(g14,g7)
    c: Coincident(g15,g7)
    c: Coincident(g15,g3)
FEATURE [Part::Extrusion] Extrude008
  Base = -> Sketch008
  Dir = (1,-2e-16,2e-16)
  DirMode = 2
  FaceMakerClass = Part::FaceMakerBullseye
  LengthFwd = 3
  LengthRev = 0
  Reversed = true
  Solid = true
  Symmetric = false
FEATURE [Part::MultiFuse] Fusion128
  Shapes = -> [Extrude008,Fusion127]
FEATURE [Part::Fillet] Fillet011  label="Cover"
  Base = -> Fusion128
  Edges = 8 edges r=1.45: [Edge8,Edge28,Edge39,Edge46,Edge53,Edge60,Edge61,Edge62]
FEATURE [Sketcher::SketchObject] Sketch009
  FullyConstrained = true
  sketch-geometry (18):
    g0: LineSegment StartX=157.5 StartY=-43.5 StartZ=0 EndX=-37.5 EndY=-43.5 EndZ=0
    g1: LineSegment StartX=-37.5 StartY=-43.5 StartZ=0 EndX=-37.5 EndY=-148.5 EndZ=0
    g2: LineSegment StartX=-37.5 StartY=-148.5 StartZ=0 EndX=157.5 EndY=-148.5 EndZ=0
    g3: LineSegment StartX=157.5 StartY=-148.5 StartZ=0 EndX=157.5 EndY=-43.5 EndZ=0
    g4: LineSegment StartX=-22.5 StartY=-58.5 StartZ=0 EndX=142.5 EndY=-58.5 EndZ=0
    g5: LineSegment StartX=142.5 StartY=-58.5 StartZ=0 EndX=142.5 EndY=-133.5 EndZ=0
    g6: LineSegment StartX=142.5 StartY=-133.5 StartZ=0 EndX=-22.5 EndY=-133.5 EndZ=0
    g7: LineSegment StartX=-22.5 StartY=-133.5 StartZ=0 EndX=-22.5 EndY=-58.5 EndZ=0
    g8: Circle CenterX=-30 CenterY=-51 CenterZ=0 NormalX=0 NormalY=0 NormalZ=1 AngleXU=0 Radius=1.75
    g9: Circle CenterX=-30 CenterY=-81 CenterZ=0 NormalX=0 NormalY=0 NormalZ=1 AngleXU=0 Radius=1.75
    g10: Circle CenterX=-30 CenterY=-111 CenterZ=0 NormalX=0 NormalY=0 NormalZ=1 AngleXU=0 Radius=1.75
    g11: Circle CenterX=-30 CenterY=-141 CenterZ=0 NormalX=0 NormalY=0 NormalZ=1 AngleXU=0 Radius=1.75
    g12: Circle CenterX=60 CenterY=-141 CenterZ=0 NormalX=0 NormalY=0 NormalZ=1 AngleXU=0 Radius=1.75
    g13: Circle CenterX=150 CenterY=-141 CenterZ=0 NormalX=0 NormalY=0 NormalZ=1 AngleXU=0 Radius=1.75
    g14: Circle CenterX=150 CenterY=-111 CenterZ=0 NormalX=0 NormalY=0 NormalZ=1 AngleXU=0 Radius=1.75
    g15: Circle CenterX=150 CenterY=-81 CenterZ=0 NormalX=0 NormalY=0 NormalZ=1 AngleXU=0 Radius=1.75
    g16: Circle CenterX=150 CenterY=-51 CenterZ=0 NormalX=0 NormalY=0 NormalZ=1 AngleXU=0 Radius=1.75
    g17: Circle CenterX=60 CenterY=-51 CenterZ=0 NormalX=0 NormalY=0 NormalZ=1 AngleXU=0 Radius=1.75
  constraints (46):
    c: Coincident(g0,g1)
    c: Coincident(g1,g2)
    c: Coincident(g2,g3)
    c: Coincident(g3,g0)
    c: Horizontal(g0)
    c: Horizontal(g2)
    c: Vertical(g1)
    c: Vertical(g3)
    c: Distance(g0) = 195
    c: Distance(g0,g-2) = 37.5
    c: Distance(g1) = 105
    c: Distance(g0,g-1) = 43.5
    c: Coincident(g4,g5)
    c: Coincident(g5,g6)
    c: Coincident(g6,g7)
    c: Coincident(g7,g4)
    c: Horizontal(g4)
    c: Horizontal(g6)
    c: Vertical(g5)
    c: Vertical(g7)
    c: Distance(g4,g0) = 15
    c: Distance(g6,g1) = 15
    c: Distance(g5,g3) = 15
    c: Distance(g5,g2) = 15
    c: Equal(g8, g9-g17) x9
    c: Diameter(g8) = 3.5
    c: Distance(g8,g0) = 7.5
    c: Distance(g8,g-2) = 30
    c: Distance(g9,g-2) = 30
    c: Distance(g10,g-2) = 30
    c: Distance(g9,g8) = 30
    c: Distance(g9,g10) = 30
    c: Distance(g10,g11) = 30
    c: Distance(g11,g-2) = 30
    c: Distance(g8,g17) = 90
    c: Distance(g17,g0) = 7.5
    c: Distance(g16,g17) = 90
    c: Distance(g16,g0) = 7.5
    c: Distance(g15,g16) = 30
    c: Distance(g9,g15) = 180
    c: Distance(g14,g10) = 180
    c: Distance(g13,g11) = 180
    c: Distance(g11,g12) = 90
    c: Distance(g17,g12) = 90
    c: Distance(g15,g14) = 30
    c: Distance(g14,g13) = 30
FEATURE [Part::Extrusion] Extrude009  label="Sensor_base"
  Base = -> Sketch009
  Dir = (0,0,1)
  DirMode = 2
  FaceMakerClass = Part::FaceMakerBullseye
  LengthFwd = 15
  LengthRev = 0
  Placement = pos=(0,0,-157) rot=(0,0,1;0rad)
  Solid = true
  Symmetric = false
FEATURE [Sketcher::SketchObject] Sketch010
  FullyConstrained = true
  sketch-geometry (25):
    g0: LineSegment StartX=157.5 StartY=-43.5 StartZ=0 EndX=-37.5 EndY=-43.5 EndZ=0
    g1: LineSegment StartX=-37.5 StartY=-43.5 StartZ=0 EndX=-37.5 EndY=-148.5 EndZ=0
    g2: LineSegment StartX=-37.5 StartY=-148.5 StartZ=0 EndX=157.5 EndY=-148.5 EndZ=0
    g3: LineSegment StartX=157.5 StartY=-148.5 StartZ=0 EndX=157.5 EndY=-43.5 EndZ=0
    g4: LineSegment StartX=-22.5 StartY=-58.5 StartZ=0 EndX=142.5 EndY=-58.5 EndZ=0
    g5: LineSegment StartX=142.5 StartY=-58.5 StartZ=0 EndX=142.5 EndY=-133.5 EndZ=0
    g6: LineSegment StartX=142.5 StartY=-133.5 StartZ=0 EndX=-22.5 EndY=-133.5 EndZ=0
    g7: LineSegment StartX=-22.5 StartY=-133.5 StartZ=0 EndX=-22.5 EndY=-58.5 EndZ=0
    g8: Circle CenterX=-30 CenterY=-51 CenterZ=0 NormalX=0 NormalY=0 NormalZ=1 AngleXU=0 Radius=1.75
    g9: Circle CenterX=-30 CenterY=-81 CenterZ=0 NormalX=0 NormalY=0 NormalZ=1 AngleXU=0 Radius=1.75
    g10: Circle CenterX=-30 CenterY=-111 CenterZ=0 NormalX=0 NormalY=0 NormalZ=1 AngleXU=0 Radius=1.75
    g11: Circle CenterX=-30 CenterY=-141 CenterZ=0 NormalX=0 NormalY=0 NormalZ=1 AngleXU=0 Radius=1.75
    g12: Circle CenterX=60 CenterY=-141 CenterZ=0 NormalX=0 NormalY=0 NormalZ=1 AngleXU=0 Radius=1.75
    g13: Circle CenterX=150 CenterY=-141 CenterZ=0 NormalX=0 NormalY=0 NormalZ=1 AngleXU=0 Radius=1.75
    g14: Circle CenterX=150 CenterY=-111 CenterZ=0 NormalX=0 NormalY=0 NormalZ=1 AngleXU=0 Radius=1.75
    g15: Circle CenterX=150 CenterY=-81 CenterZ=0 NormalX=0 NormalY=0 NormalZ=1 AngleXU=0 Radius=1.75
    g16: Circle CenterX=150 CenterY=-51 CenterZ=0 NormalX=0 NormalY=0 NormalZ=1 AngleXU=0 Radius=1.75
    g17: Circle CenterX=60 CenterY=-51 CenterZ=0 NormalX=0 NormalY=0 NormalZ=1 AngleXU=0 Radius=1.75
    g18: Circle CenterX=7.5 CenterY=-51 CenterZ=0 NormalX=0 NormalY=0 NormalZ=1 AngleXU=0 Radius=1.25
    g19: Circle CenterX=-9.75 CenterY=-141 CenterZ=0 NormalX=0 NormalY=0 NormalZ=1 AngleXU=0 Radius=1.5
    g20: Circle CenterX=10.55 CenterY=-141 CenterZ=0 NormalX=0 NormalY=0 NormalZ=1 AngleXU=0 Radius=1.5
    g21: Circle CenterX=30.8 CenterY=-141 CenterZ=0 NormalX=0 NormalY=0 NormalZ=1 AngleXU=0 Radius=1.5
    g22: Circle CenterX=51.1 CenterY=-141 CenterZ=0 NormalX=0 NormalY=0 NormalZ=1 AngleXU=0 Radius=1.5
    g23: Circle CenterX=71.4 CenterY=-141 CenterZ=0 NormalX=0 NormalY=0 NormalZ=1 AngleXU=0 Radius=1.5
    g24: Circle CenterX=129.4 CenterY=-141 CenterZ=0 NormalX=0 NormalY=0 NormalZ=1 AngleXU=0 Radius=1.5
  constraints (63):
    c: Coincident(g0,g1)
    c: Coincident(g1,g2)
    c: Coincident(g2,g3)
    c: Coincident(g3,g0)
    c: Horizontal(g0)
    c: Horizontal(g2)
    c: Vertical(g1)
    c: Vertical(g3)
    c: Distance(g0) = 195
    c: Distance(g0,g-2) = 37.5
    c: Distance(g1) = 105
    c: Distance(g0,g-1) = 43.5
    c: Coincident(g4,g5)
    c: Coincident(g5,g6)
    c: Coincident(g6,g7)
    c: Coincident(g7,g4)
    c: Horizontal(g4)
    c: Horizontal(g6)
    c: Vertical(g5)
    c: Vertical(g7)
    c: Distance(g4,g0) = 15
    c: Distance(g6,g1) = 15
    c: Distance(g5,g3) = 15
    c: Distance(g5,g2) = 15
    c: Equal(g8, g9-g17) x9
    c: Diameter(g8) = 3.5
    c: Distance(g8,g0) = 7.5
    c: Distance(g8,g-2) = 30
    c: Distance(g9,g-2) = 30
    c: Distance(g10,g-2) = 30
    c: Distance(g9,g8) = 30
    c: Distance(g9,g10) = 30
    c: Distance(g10,g11) = 30
    c: Distance(g11,g-2) = 30
    c: Distance(g8,g17) = 90
    c: Distance(g17,g0) = 7.5
    c: Distance(g16,g17) = 90
    c: Distance(g16,g0) = 7.5
    c: Distance(g15,g16) = 30
    c: Distance(g9,g15) = 180
    c: Distance(g14,g10) = 180
    c: Distance(g13,g11) = 180
    c: Distance(g11,g12) = 90
    c: Distance(g17,g12) = 90
    c: Distance(g15,g14) = 30
    c: Distance(g14,g13) = 30
    c: Diameter(g18) = 2.5
    c: Distance(g18,g0) = 7.5
    c: Distance(g8,g18) = 37.5
    c: Equal(g19, g20-g24) x5
    c: Diameter(g19) = 3
    c: Distance(g19,g2) = 7.5
    c: Distance(g11,g19) = 20.25
    c: Distance(g19,g20) = 20.3
    c: Distance(g20,g2) = 7.5
    c: Distance(g21,g2) = 7.5
    c: Distance(g22,g2) = 7.5
    c: Distance(g20,g21) = 20.25
    c: Distance(g21,g22) = 20.3
    c: Distance(g22,g23) = 20.3
    c: Distance(g23,g2) = 7.5
    c: Distance(g23,g24) = 58
    c: Distance(g24,g2) = 7.5
FEATURE [Part::Extrusion] Extrude010  label="Sensor_top"
  Base = -> Sketch010
  Dir = (0,0,1)
  DirMode = 2
  FaceMakerClass = Part::FaceMakerBullseye
  LengthFwd = 15
  LengthRev = 0
  Placement = pos=(0,0,-77) rot=(0,0,1;0rad)
  Solid = true
  Symmetric = false
FEATURE [Part::Feature] Part__Feature099  label="COZIR"
  Placement = pos=(5.41029,2.97838,5.56111) rot=(0,0,1;0rad)
  shape: bbox 51.61 x 17 x 50.23 mm, 43 faces (baked)
FEATURE [Part::Feature] Part__Feature100  label="COMPOUND"
  shape: bbox 3.14 x 5 x 10.76 mm, 60 faces, 10 solids (baked)
FEATURE [App::Part] COZIR_Sensor_v2  label="COZIR Sensor v2"
  Group = -> [Part__Feature099,Part__Feature100]
  Origin = -> Origin043
  Placement = pos=(8.96345,-74.5,-143) rot=(-0.258819,0,-0.965926;3.14159rad)
FEATURE [Mesh::Feature] _1_001  label="Opc_n3"
  Placement = pos=(-14,-84,-119.5) rot=(0,0,1;0rad)
FEATURE [Part::Feature] Part__Feature101  label="ips7100"
  Placement = pos=(-24,0,222) rot=(0.999993,-0.003655,0;3.14159rad)
  shape: bbox 48.14 x 14.05 x 44.14 mm, 1935 faces (baked)
FEATURE [Part::Compound] Compound  label="ips7100s"
  Links = -> [Part__Feature101]
  Placement = pos=(43,-47,-76) rot=(-0.570657,-0.580668,0.580668;2.0944rad)
FEATURE [Part::Feature] Part__Feature102  label="Board001"
  shape: bbox 25.4 x 25.4 x 1.57 mm, 211 faces (baked)
FEATURE [Part::Feature] Part__Feature103  label="QFN24_4MM001"
  Placement = pos=(12.1412,14.4526,1.57) rot=(0,0,1;3.92699rad)
  shape: bbox 5.657 x 5.657 x 0.9 mm, 172 faces (baked)
FEATURE [Part::Feature] Part__Feature104  label="Part 007"
  shape: bbox 0.48 x 0.6603 x 0.6 mm, 14 faces (baked)
FEATURE [Part::Feature] Part__Feature105  label="Part 008"
  shape: bbox 0.48 x 0.6603 x 0.6 mm, 14 faces (baked)
FEATURE [Part::Feature] Part__Feature106  label="Part 009"
  shape: bbox 0.48 x 0.6603 x 0.6 mm, 14 faces (baked)
FEATURE [Part::Feature] Part__Feature107  label="Part 010"
  shape: bbox 0.48 x 0.6603 x 0.6 mm, 14 faces (baked)
FEATURE [Part::Feature] Part__Feature108  label="Part 011"
  shape: bbox 0.48 x 0.6603 x 0.6 mm, 14 faces (baked)
FEATURE [Part::Feature] Part__Feature109  label="Part 012"
  shape: bbox 3 x 1.4 x 1 mm, 10 faces (baked)
FEATURE [Part::Feature] Part__Feature110  label="Pin003"
  shape: bbox 0.6224 x 1.252 x 1.252 mm, 37 faces (baked)
FEATURE [Part::Feature] Part__Feature111  label="Pin004"
  shape: bbox 0.6224 x 1.252 x 1.252 mm, 37 faces (baked)
FEATURE [Part::Feature] Part__Feature112  label="CeramicBody001"
  shape: bbox 1.8 x 1.23 x 1.23 mm, 10 faces (baked)
FEATURE [Part::Feature] Part__Feature113  label="0603-NO (1)001"
  Placement = pos=(23.241,6.223,1.57) rot=(0,0,1;0rad)
  shape: bbox 1.7 x 0.9 x 0.55 mm, 52 faces, 3 solids (baked)
FEATURE [Part::Feature] Part__Feature114  label="0603-NO (2)001"
  Placement = pos=(13.3858,8.4328,1.57) rot=(0,0,1;0rad)
  shape: bbox 1.7 x 0.9 x 0.55 mm, 52 faces, 3 solids (baked)
FEATURE [Part::Feature] Part__Feature115  label="0603-NO (3)001"
  Placement = pos=(1.905,18.923,1.57) rot=(0,0,1;3.14159rad)
  shape: bbox 1.7 x 0.9 x 0.55 mm, 52 faces, 3 solids (baked)
FEATURE [Part::Feature] Part__Feature116  label="Pin1 (1)001"
  shape: bbox 0.6224 x 1.252 x 1.252 mm, 37 faces (baked)
FEATURE [Part::Feature] Part__Feature117  label="Pin2 (1)001"
  shape: bbox 0.6224 x 1.252 x 1.252 mm, 37 faces (baked)
FEATURE [Part::Feature] Part__Feature118  label="CeramicBody (1)001"
  shape: bbox 1.8 x 1.23 x 1.23 mm, 10 faces (baked)
FEATURE [Part::Feature] Part__Feature119  label="Pin1 (2)001"
  shape: bbox 0.6224 x 1.252 x 1.252 mm, 37 faces (baked)
FEATURE [Part::Feature] Part__Feature120  label="Pin2 (2)001"
  shape: bbox 0.6224 x 1.252 x 1.252 mm, 37 faces (baked)
FEATURE [Part::Feature] Part__Feature121  label="CeramicBody (2)001"
  shape: bbox 1.8 x 1.23 x 1.23 mm, 10 faces (baked)
FEATURE [Part::Feature] Part__Feature122  label="CHIPLED_0603_NOOUTLINE001"
  Placement = pos=(23.368,8.509,1.57) rot=(0,0,1;1.5708rad)
  shape: bbox 1.616 x 0.8 x 0.4 mm, 133 faces (baked)
FEATURE [Part::Feature] Part__Feature123  label="CHIPLED_0603_NOOUTLINE (1)001"
  Placement = pos=(1.905,16.764,1.57) rot=(0,0,-1;1.5708rad)
  shape: bbox 1.616 x 0.8 x 0.4 mm, 133 faces (baked)
FEATURE [Part::Feature] Part__Feature124  label="JST_SH005"
  Placement = pos=(22.86,12.7,1.57) rot=(0,0,1;1.5708rad)
  shape: bbox 4.95 x 6 x 2.96 mm, 229 faces, 7 solids (baked)
FEATURE [Part::Feature] Part__Feature125  label="JST_SH4 (1)001"
  Placement = pos=(2.54,12.7,1.57) rot=(0,0,-1;1.5708rad)
  shape: bbox 4.95 x 6 x 2.96 mm, 229 faces, 7 solids (baked)
FEATURE [Part::Feature] Part__Feature126  label="NEO3535_REVERSE001"
  Placement = pos=(12.7,23.114,0) rot=(0,1,0;3.14159rad)
  shape: bbox 5.88 x 2.8 x 1.78 mm, 41 faces, 5 solids (baked)
FEATURE [Part::Feature] Part__Feature127  label="RESPACK_4X0604"
  Placement = pos=(22.86,18.415,1.57) rot=(0,0,1;3.14159rad)
  shape: bbox 3.2 x 1.6 x 0.61 mm, 172 faces (baked)
FEATURE [Part::Feature] Part__Feature128  label="SOT364"
  Placement = pos=(17.399,12.192,1.57) rot=(0,0,-1;1.5708rad)
  shape: bbox 2.208 x 2.208 x 1.121 mm, 178 faces, 4 solids (baked)
FEATURE [Sketcher::SketchObject] Sketch011
  FullyConstrained = true
  sketch-geometry (39):
    g0: LineSegment StartX=3 StartY=43.5 StartZ=0 EndX=3 EndY=34.5 EndZ=0
    g1: LineSegment StartX=3 StartY=34.5 StartZ=0 EndX=70.5 EndY=34.5 EndZ=0
    g2: LineSegment StartX=3 StartY=43.5 StartZ=0 EndX=10.5 EndY=43.5 EndZ=0
    g3: LineSegment StartX=3 StartY=71 StartZ=0 EndX=10.5 EndY=71 EndZ=0
    g4: LineSegment StartX=3 StartY=71 StartZ=0 EndX=3 EndY=80 EndZ=0
    g5: LineSegment StartX=70.5 StartY=80 StartZ=0 EndX=70.5 EndY=71 EndZ=0
    g6: LineSegment StartX=70.5 StartY=71 StartZ=0 EndX=62.5 EndY=71 EndZ=0
    g7: LineSegment StartX=62.5 StartY=71 StartZ=0 EndX=62.5 EndY=43 EndZ=0
    g8: LineSegment StartX=62.5 StartY=43 StartZ=0 EndX=70.5 EndY=43 EndZ=0
    g9: LineSegment StartX=70.5 StartY=43 StartZ=0 EndX=70.5 EndY=34.5 EndZ=0
    g10: GeomPoint X=70.5 Y=34.5 Z=0
    g11: GeomPoint X=70.5 Y=34.5 Z=0
    g12: GeomPoint X=70.5 Y=34.5 Z=0
    g13: GeomPoint X=70.5 Y=34.5 Z=0
    g14: GeomPoint X=70.5 Y=34.5 Z=0
    g15: LineSegment StartX=10.5 StartY=43.5 StartZ=0 EndX=10.5 EndY=71 EndZ=0
    g16: Circle CenterX=7.5 CenterY=75.5 CenterZ=0 NormalX=0 NormalY=0 NormalZ=1 AngleXU=0 Radius=1.6
    g17: Circle CenterX=7.5 CenterY=39 CenterZ=0 NormalX=0 NormalY=0 NormalZ=1 AngleXU=0 Radius=1.6
    g18: Circle CenterX=66.5 CenterY=39 CenterZ=0 NormalX=0 NormalY=0 NormalZ=1 AngleXU=0 Radius=1.6
    g19: Circle CenterX=66.5 CenterY=75.5 CenterZ=0 NormalX=0 NormalY=0 NormalZ=1 AngleXU=0 Radius=1.6
    g20: Circle CenterX=14.2 CenterY=70.46 CenterZ=0 NormalX=0 NormalY=0 NormalZ=1 AngleXU=0 Radius=1.6
    g21: Circle CenterX=38.54 CenterY=77.84 CenterZ=0 NormalX=0 NormalY=0 NormalZ=1 AngleXU=0 Radius=1.6
    g22: Circle CenterX=58.86 CenterY=77.84 CenterZ=0 NormalX=0 NormalY=0 NormalZ=1 AngleXU=0 Radius=1.6
    g23: Circle CenterX=38.54 CenterY=57.52 CenterZ=0 NormalX=0 NormalY=0 NormalZ=1 AngleXU=0 Radius=1.6
    g24: Circle CenterX=58.86 CenterY=57.52 CenterZ=0 NormalX=0 NormalY=0 NormalZ=1 AngleXU=0 Radius=1.6
    g25: Circle CenterX=38.54 CenterY=52.33 CenterZ=0 NormalX=0 NormalY=0 NormalZ=1 AngleXU=0 Radius=1.6
    g26: Circle CenterX=58.86 CenterY=52.33 CenterZ=0 NormalX=0 NormalY=0 NormalZ=1 AngleXU=0 Radius=1.6
    g27: Circle CenterX=38.54 CenterY=39.63 CenterZ=0 NormalX=0 NormalY=0 NormalZ=1 AngleXU=0 Radius=1.6
    g28: Circle CenterX=58.86 CenterY=39.63 CenterZ=0 NormalX=0 NormalY=0 NormalZ=1 AngleXU=0 Radius=1.6
    g29: Circle CenterX=30.43 CenterY=38.46 CenterZ=0 NormalX=0 NormalY=0 NormalZ=1 AngleXU=0 Radius=1.6
    g30: ArcOfCircle CenterX=48.54 CenterY=70.34 CenterZ=0 NormalX=0 NormalY=0 NormalZ=1 AngleXU=0 Radius=5 StartAngle=-9e-16 EndAngle=3.14159
    g31: ArcOfCircle CenterX=48.54 CenterY=42.63 CenterZ=0 NormalX=0 NormalY=0 NormalZ=1 AngleXU=0 Radius=5 StartAngle=3.14159 EndAngle=6.28319
    g32: LineSegment StartX=43.54 StartY=70.34 StartZ=0 EndX=43.54 EndY=42.63 EndZ=0
    g33: LineSegment StartX=53.54 StartY=42.63 StartZ=0 EndX=53.54 EndY=70.34 EndZ=0
    g34: ArcOfCircle CenterX=22.2 CenterY=70.34 CenterZ=0 NormalX=0 NormalY=0 NormalZ=1 AngleXU=0 Radius=5 StartAngle=0 EndAngle=3.14159
    g35: ArcOfCircle CenterX=22.2 CenterY=42.63 CenterZ=0 NormalX=0 NormalY=0 NormalZ=1 AngleXU=0 Radius=5 StartAngle=3.14159 EndAngle=6.28319
    g36: LineSegment StartX=17.2 StartY=70.34 StartZ=0 EndX=17.2 EndY=42.63 EndZ=0
    g37: LineSegment StartX=27.2 StartY=42.63 StartZ=0 EndX=27.2 EndY=70.34 EndZ=0
    g38: LineSegment StartX=3 StartY=80 StartZ=0 EndX=70.5 EndY=80 EndZ=0
  constraints (103):
    c: Vertical(g0)
    c: Coincident(g1,g0)
    c: Horizontal(g1)
    c: Coincident(g2,g0)
    c: Coincident(g4,g3)
    c: Vertical(g4)
    c: Coincident(g6,g5)
    c: Horizontal(g6)
    c: Coincident(g7,g6)
    c: Vertical(g7)
    c: Horizontal(g8)
    c: Horizontal(g2)
    c: Coincident(g10,g9)
    c: Coincident(g11,g1)
    c: Coincident(g12,g9)
    c: Coincident(g13,g1)
    c: Coincident(g14,g9)
    c: Coincident(g9,g1)
    c: Vertical(g9)
    c: Coincident(g15,g2)
    c: Coincident(g15,g3)
    c: Vertical(g15)
    c: Horizontal(g3)
    c: Vertical(g5)
    c: Coincident(g8,g9)
    c: Coincident(g7,g8)
    c: DistanceX(g8,g8) = 8
    c: Radius(g16) = 1.6
    c: DistanceY(g17) = 39
    c: Radius(g17) = 1.6
    c: DistanceX(g18) = 66.5
    c: DistanceY(g17,g18) = 0
    c: Radius(g18) = 1.6
    c: DistanceX(g19,g18) = 0
    c: Radius(g19) = 1.6
    c: DistanceY(g16) = 75.5
    c: DistanceY(g16,g19) = 0
    c: DistanceY(g3,g5) = 0
    c: Radius(g21) = 1.6
    c: DistanceY(g21,g22) = 0
    c: Radius(g22) = 1.6
    c: DistanceX(g21,g22) = 20.32
    c: DistanceX(g23,g21) = 0
    c: Radius(g23) = 1.6
    c: DistanceY(g23,g21) = 20.32
    c: DistanceY(g24,g23) = 0
    c: DistanceX(g24,g22) = 0
    c: Radius(g24) = 1.6
    c: DistanceX(g25,g23) = 0
    c: Radius(g25) = 1.6
    c: DistanceY(g25,g26) = 0
    c: DistanceX(g24,g26) = 0
    c: Radius(g26) = 1.6
    c: DistanceX(g25,g27) = 0
    c: DistanceX(g28,g26) = 0
    c: DistanceY(g27,g25) = 12.7
    c: DistanceY(g28,g27) = 0
    c: Radius(g28) = 1.6
    c: Radius(g27) = 1.6
    c: Radius(g29) = 1.6
    c: DistanceY(g29,g20) = 32
    c: Radius(g20) = 1.6
    c: Tangent(g30,g32) = -1.5708
    c: Tangent(g32,g31) = -1.5708
    c: Tangent(g31,g33) = -1.5708
    c: Tangent(g33,g30) = -1.5708
    c: Equal(g30,g31)
    c: Vertical(g32)
    c: DistanceY(g27,g31) = 3
    c: Radius(g30) = 5
    c: Tangent(g34,g36) = -1.5708
    c: Tangent(g36,g35) = -1.5708
    c: Tangent(g35,g37) = -1.5708
    c: Tangent(g37,g34) = -1.5708
    c: Equal(g34,g35)
    c: Vertical(g36)
    c: Radius(g34) = 5
    c: DistanceY(g34,g30) = 0
    c: DistanceY(g31,g35) = 0
    c: DistanceX(g16,g17) = 0
    c: DistanceX(g0,g3) = 0
    c: Coincident(g38,g4)
    c: Coincident(g38,g5)
    c: Horizontal(g38)
    c: DistanceX(g29) = 30.43
    c: DistanceX(g20) = 14.2
    c: DistanceY(g20) = 70.46
    c: DistanceX(g27) = 38.54
    c: DistanceY(g27) = 39.63
    c: DistanceY(g23) = 57.52
    c: DistanceY(g3,g16) = 4.5
    c: DistanceY(g16,g4) = 4.5
    c: DistanceY(g0,g17) = 4.5
    c: DistanceX(g0,g17) = 4.5
    c: DistanceX(g17) = 7.5
    c: DistanceY(g17,g0) = 4.5
    c: DistanceX(g16,g3) = 3
    c: DistanceX(g19,g5) = 4
    c: DistanceX(g6,g19) = 4
    c: DistanceY(g18,g8) = 4
    c: DistanceX(g25,g31) = 10
    c: DistanceY(g30,g21) = 7.5
    c: DistanceX(g20,g34) = 8
FEATURE [Part::Extrusion] Extrude011  label="sensorHold002"
  Base = -> Sketch011
  Dir = (0,0,1)
  DirMode = 2
  FaceMakerClass = Part::FaceMakerBullseye
  LengthFwd = 4
  LengthRev = 0
  Placement = pos=(0,0,16) rot=(0,0,1;0rad)
  Solid = true
  Symmetric = false
FEATURE [Part::Fillet] Fillet012  label="sensorHold003"
  Base = -> Extrude011
  Edges = 12 edges r=3: [Edge1,Edge2,Edge5,Edge8,Edge11,Edge14,Edge17,Edge20,Edge23,Edge26,Edge29,Edge32]
FEATURE [App::Part] _603_NO001  label="0603-NO001"
  Group = -> [Part__Feature110,Part__Feature111,Part__Feature112]
  Origin = -> Origin046
  Placement = pos=(16.51,8.382,1.57) rot=(0,0,1;0rad)
FEATURE [App::Part] _6700498  label="36700497001"
  Group = -> [Part__Feature104,Part__Feature105,Part__Feature106,Part__Feature107,Part__Feature108,Part__Feature109]
  Origin = -> Origin044
  Placement = pos=(0,0,0) rot=(0,0,1;3.14159rad)
FEATURE [App::Part] SOT23_006  label="SOT23-006"
  Group = -> [_6700498]
  Origin = -> Origin045
  Placement = pos=(2.54,6.985,1.57) rot=(0,0,1;3.14159rad)
FEATURE [App::Part] _805_NO001  label="0805-NO001"
  Group = -> [Part__Feature116,Part__Feature117,Part__Feature118]
  Origin = -> Origin047
  Placement = pos=(7.874,13.589,1.57) rot=(0,0,1;1.5708rad)
FEATURE [App::Part] _805_NO__1_001  label="0805-NO (1)001"
  Group = -> [Part__Feature119,Part__Feature120,Part__Feature121]
  Origin = -> Origin048
  Placement = pos=(12.827,6.223,1.57) rot=(0,0,1;3.14159rad)
FEATURE [App::Part] Packages001
  Group = -> [Part__Feature103,SOT23_006,_603_NO001,Part__Feature113,Part__Feature114,Part__Feature115,_805_NO001,_805_NO__1_001,Part__Feature122,Part__Feature123,Part__Feature124,Part__Feature125,Part__Feature126,Part__Feature127,Part__Feature128]
  Origin = -> Origin049
FEATURE [App::Part] Adafruit_I2C_QT_Rotary_Encoder_v003  label="GPS"
  Group = -> [Part__Feature102,Packages001,Sketch011,Extrude011,Fillet012]
  Origin = -> Origin050
  Placement = pos=(15,-118.125,-66.5) rot=(0,0,1;4.71239rad)
FEATURE [Part::Feature] Part__Feature334  label="CAPC-0805-T0.95-BN v012"
  Placement = pos=(-5.48627,2.66154,1.6) rot=(0,0,-1;1.5708rad)
  shape: bbox 1.35 x 2.1 x 0.95 mm, 42 faces (baked)
FEATURE [Part::Feature] Part__Feature335  label="CAPC-0805-T0.95-BN v013"
  Placement = pos=(-3.43627,2.66154,1.6) rot=(0,0,-1;1.5708rad)
  shape: bbox 1.35 x 2.1 x 0.95 mm, 42 faces (baked)
FEATURE [Part::Feature] Part__Feature336  label="CAPC-0603-T0.9-BN v009"
  Placement = pos=(-1.69987,-3.28475,1.6) rot=(0,0,1;0rad)
  shape: bbox 1.7 x 0.9 x 0.9 mm, 42 faces (baked)
FEATURE [Part::Feature] Part__Feature337  label="BODY_MF06A003"
  Placement = pos=(0,0,0.762) rot=(0.57735,-0.57735,-0.57735;2.0944rad)
  shape: bbox 1.601 x 2.921 x 1.016 mm, 42 faces (baked)
FEATURE [Part::Feature] Part__Feature338  label="LEAD_MF06A018"
  Placement = pos=(-0.9652,-0.9525,0.1016) rot=(0.57735,-0.57735,-0.57735;2.0944rad)
  shape: bbox 0.6223 x 0.3749 x 0.8636 mm, 14 faces (baked)
FEATURE [Part::Feature] Part__Feature339  label="LEAD_MF06A019"
  Placement = pos=(-0.9652,0,0.1016) rot=(0.57735,-0.57735,-0.57735;2.0944rad)
  shape: bbox 0.6223 x 0.3749 x 0.8636 mm, 14 faces (baked)
FEATURE [Part::Feature] Part__Feature340  label="LEAD_MF06A020"
  Placement = pos=(-0.9652,0.9525,0.1016) rot=(0.57735,-0.57735,-0.57735;2.0944rad)
  shape: bbox 0.6223 x 0.3749 x 0.8636 mm, 14 faces (baked)
FEATURE [Part::Feature] Part__Feature341  label="LEAD_MF06A021"
  Placement = pos=(0.9652,-0.9525,0.1016) rot=(0.57735,0.57735,0.57735;2.0944rad)
  shape: bbox 0.6223 x 0.3749 x 0.8636 mm, 14 faces (baked)
FEATURE [Part::Feature] Part__Feature342  label="LEAD_MF06A022"
  Placement = pos=(0.9652,0,0.1016) rot=(0.57735,0.57735,0.57735;2.0944rad)
  shape: bbox 0.6223 x 0.3749 x 0.8636 mm, 14 faces (baked)
FEATURE [Part::Feature] Part__Feature343  label="LEAD_MF06A023"
  Placement = pos=(0.9652,0.9525,0.1016) rot=(0.57735,0.57735,0.57735;2.0944rad)
  shape: bbox 0.6223 x 0.3749 x 0.8636 mm, 14 faces (baked)
FEATURE [Part::Feature] Part__Feature344  label="SOT363 v005"
  Placement = pos=(4.97054,-0.645171,1.675) rot=(0,0,1;3.14159rad)
  shape: bbox 2.1 x 2 x 1.1 mm, 94 faces, 7 solids (baked)
FEATURE [Part::Feature] Part__Feature345  label="LED 0603 single color v005"
  Placement = pos=(-9.18406,3.72778,1.60762) rot=(0,0,1;1.5708rad)
  shape: bbox 1.961 x 0.7932 x 0.7145 mm, 63 faces, 5 solids (baked)
FEATURE [Part::Feature] Part__Feature346  label="RESC-0603 v007"
  Placement = pos=(4.83432,-3.67461,1.6) rot=(0,0,1;0rad)
  shape: bbox 1.7 x 0.9 x 0.55 mm, 52 faces, 3 solids (baked)
FEATURE [Part::Feature] Part__Feature347  label="RESC-0603 v008"
  Placement = pos=(-7.14949,3.61248,1.6) rot=(0,0,-1;1.5708rad)
  shape: bbox 0.9 x 1.7 x 0.55 mm, 52 faces, 3 solids (baked)
FEATURE [Part::Feature] Part__Feature348  label="Printed Circuit Board004"
  shape: bbox 25.4 x 17.78 x 1.6 mm, 42 faces (baked)
FEATURE [Part::Feature] Part__Feature349  label="EAHC2835WD009"
  shape: bbox 3.513 x 2.813 x 0.7485 mm, 108 faces, 4 solids (baked)
FEATURE [Part::Feature] Part__Feature350  label="AS7341 v005"
  Placement = pos=(0,-0.339822,1.6) rot=(0,0,1;0rad)
  shape: bbox 2 x 3.1 x 1.1 mm, 267 faces, 26 solids (baked)
FEATURE [Part::Feature] Part__Feature351  label="CAPC-0805-T0.95-BN v014"
  Placement = pos=(-5.01759,-3.15294,1.6) rot=(0,0,1;0rad)
  shape: bbox 2.1 x 1.35 x 0.95 mm, 42 faces (baked)
FEATURE [Part::Feature] Part__Feature352  label="YC164_RESPACK v007"
  Placement = pos=(2.99591,1.52916,1.6) rot=(0,0,1;0rad)
  shape: bbox 3.2 x 1.6 x 0.61 mm, 172 faces (baked)
FEATURE [Part::Feature] Part__Feature353  label="qwicc v009"
  Placement = pos=(-10.8364,0.0607456,1.65) rot=(0,0,-1;1.5708rad)
  shape: bbox 4.95 x 6 x 2.96 mm, 229 faces, 7 solids (baked)
FEATURE [Part::Feature] Part__Feature354  label="qwicc v010"
  Placement = pos=(10.8256,0.00556102,1.65) rot=(0,0,1;1.5708rad)
  shape: bbox 4.95 x 6 x 2.96 mm, 229 faces, 7 solids (baked)
FEATURE [App::Part] sot_23_6_v005  label="sot-23-6 v005"
  Group = -> [Part__Feature337,Part__Feature338,Part__Feature339,Part__Feature340,Part__Feature341,Part__Feature342,Part__Feature343]
  Origin = -> Origin019
  Placement = pos=(-4.47945,-0.603742,1.69152) rot=(0,0,1;0rad)
FEATURE [App::Part] Adafruit_AS7341_STEMMA_QT_v005  label="bme280"
  Group = -> [Part__Feature348,Part__Feature349,Part__Feature350,Part__Feature351,Part__Feature334,Part__Feature335,Part__Feature336,sot_23_6_v005,Part__Feature344,Part__Feature345,Part__Feature346,Part__Feature347,Part__Feature352,Part__Feature353,Part__Feature354]
  Origin = -> Origin020
  Placement = pos=(77.5,-121,-146.5) rot=(0,0,1;3.14159rad)
FEATURE [Part::Feature] Part__Feature355  label="Printed Circuit Board"
  shape: bbox 25.4 x 17.78 x 1.6 mm, 53 faces (baked)
FEATURE [Part::Feature] Part__Feature356  label="ICM-20948-9axis-IMU v2"
  Placement = pos=(-0.10588,0.00770028,1.6) rot=(0,0,-1;1.5708rad)
  shape: bbox 0.2 x 0.3 x 0.15 mm, 8 faces (baked)
FEATURE [Part::Feature] Part__Feature357  label="ICM-20948-9axis-IMU v003"
  Placement = pos=(-0.10588,0.00770028,1.6) rot=(0,0,-1;1.5708rad)
  shape: bbox 0.2 x 0.3 x 0.15 mm, 8 faces (baked)
FEATURE [Part::Feature] Part__Feature358  label="ICM-20948-9axis-IMU v004"
  Placement = pos=(-0.10588,0.00770028,1.6) rot=(0,0,-1;1.5708rad)
  shape: bbox 0.2 x 0.3 x 0.15 mm, 8 faces (baked)
FEATURE [Part::Feature] Part__Feature359  label="ICM-20948-9axis-IMU v005"
  Placement = pos=(-0.10588,0.00770028,1.6) rot=(0,0,-1;1.5708rad)
  shape: bbox 0.2 x 0.3 x 0.15 mm, 10 faces (baked)
FEATURE [Part::Feature] Part__Feature360  label="ICM-20948-9axis-IMU v006"
  Placement = pos=(-0.10588,0.00770028,1.6) rot=(0,0,-1;1.5708rad)
  shape: bbox 0.2 x 0.3 x 0.15 mm, 8 faces (baked)
FEATURE [Part::Feature] Part__Feature361  label="ICM-20948-9axis-IMU v007"
  Placement = pos=(-0.10588,0.00770028,1.6) rot=(0,0,-1;1.5708rad)
  shape: bbox 0.2 x 0.3 x 0.15 mm, 10 faces (baked)
FEATURE [Part::Feature] Part__Feature362  label="ICM-20948-9axis-IMU v008"
  Placement = pos=(-0.10588,0.00770028,1.6) rot=(0,0,-1;1.5708rad)
  shape: bbox 0.3 x 0.2 x 0.15 mm, 8 faces (baked)
FEATURE [Part::Feature] Part__Feature363  label="ICM-20948-9axis-IMU v009"
  Placement = pos=(-0.10588,0.00770028,1.6) rot=(0,0,-1;1.5708rad)
  shape: bbox 0.3 x 0.2 x 0.15 mm, 8 faces (baked)
FEATURE [Part::Feature] Part__Feature364  label="ICM-20948-9axis-IMU v010"
  Placement = pos=(-0.10588,0.00770028,1.6) rot=(0,0,-1;1.5708rad)
  shape: bbox 0.3 x 0.2 x 0.15 mm, 8 faces (baked)
FEATURE [Part::Feature] Part__Feature365  label="ICM-20948-9axis-IMU v011"
  Placement = pos=(-0.10588,0.00770028,1.6) rot=(0,0,-1;1.5708rad)
  shape: bbox 0.3 x 0.2 x 0.15 mm, 8 faces (baked)
FEATURE [Part::Feature] Part__Feature366  label="ICM-20948-9axis-IMU v012"
  Placement = pos=(-0.10588,0.00770028,1.6) rot=(0,0,-1;1.5708rad)
  shape: bbox 0.3 x 0.2 x 0.15 mm, 10 faces (baked)
FEATURE [Part::Feature] Part__Feature367  label="ICM-20948-9axis-IMU v013"
  Placement = pos=(-0.10588,0.00770028,1.6) rot=(0,0,-1;1.5708rad)
  shape: bbox 0.3 x 0.2 x 0.15 mm, 10 faces (baked)
FEATURE [Part::Feature] Part__Feature368  label="ICM-20948-9axis-IMU v014"
  Placement = pos=(-0.10588,0.00770028,1.6) rot=(0,0,-1;1.5708rad)
  shape: bbox 0.2 x 0.3 x 0.15 mm, 8 faces (baked)
FEATURE [Part::Feature] Part__Feature369  label="ICM-20948-9axis-IMU v015"
  Placement = pos=(-0.10588,0.00770028,1.6) rot=(0,0,-1;1.5708rad)
  shape: bbox 0.2 x 0.3 x 0.15 mm, 8 faces (baked)
FEATURE [Part::Feature] Part__Feature370  label="ICM-20948-9axis-IMU v016"
  Placement = pos=(-0.10588,0.00770028,1.6) rot=(0,0,-1;1.5708rad)
  shape: bbox 0.2 x 0.3 x 0.15 mm, 8 faces (baked)
FEATURE [Part::Feature] Part__Feature371  label="ICM-20948-9axis-IMU v017"
  Placement = pos=(-0.10588,0.00770028,1.6) rot=(0,0,-1;1.5708rad)
  shape: bbox 0.2 x 0.3 x 0.15 mm, 8 faces (baked)
FEATURE [Part::Feature] Part__Feature372  label="ICM-20948-9axis-IMU v018"
  Placement = pos=(-0.10588,0.00770028,1.6) rot=(0,0,-1;1.5708rad)
  shape: bbox 0.3 x 0.2 x 0.15 mm, 8 faces (baked)
FEATURE [Part::Feature] Part__Feature373  label="ICM-20948-9axis-IMU v019"
  Placement = pos=(-0.10588,0.00770028,1.6) rot=(0,0,-1;1.5708rad)
  shape: bbox 0.2 x 0.3 x 0.15 mm, 10 faces (baked)
FEATURE [Part::Feature] Part__Feature374  label="ICM-20948-9axis-IMU v020"
  Placement = pos=(-0.10588,0.00770028,1.6) rot=(0,0,-1;1.5708rad)
  shape: bbox 0.3 x 0.2 x 0.15 mm, 8 faces (baked)
FEATURE [Part::Feature] Part__Feature375  label="ICM-20948-9axis-IMU v021"
  Placement = pos=(-0.10588,0.00770028,1.6) rot=(0,0,-1;1.5708rad)
  shape: bbox 0.2 x 0.3 x 0.15 mm, 10 faces (baked)
FEATURE [Part::Feature] Part__Feature376  label="ICM-20948-9axis-IMU v022"
  Placement = pos=(-0.10588,0.00770028,1.6) rot=(0,0,-1;1.5708rad)
  shape: bbox 0.3 x 0.2 x 0.15 mm, 8 faces (baked)
FEATURE [Part::Feature] Part__Feature377  label="ICM-20948-9axis-IMU v023"
  Placement = pos=(-0.10588,0.00770028,1.6) rot=(0,0,-1;1.5708rad)
  shape: bbox 0.3 x 0.2 x 0.15 mm, 8 faces (baked)
FEATURE [Part::Feature] Part__Feature378  label="ICM-20948-9axis-IMU v024"
  Placement = pos=(-0.10588,0.00770028,1.6) rot=(0,0,-1;1.5708rad)
  shape: bbox 0.3 x 0.2 x 0.15 mm, 10 faces (baked)
FEATURE [Part::Feature] Part__Feature379  label="ICM-20948-9axis-IMU v025"
  Placement = pos=(-0.10588,0.00770028,1.6) rot=(0,0,-1;1.5708rad)
  shape: bbox 0.3 x 0.2 x 0.15 mm, 10 faces (baked)
FEATURE [Part::Feature] Part__Feature380  label="ICM-20948-9axis-IMU v026"
  Placement = pos=(-0.10588,0.00770028,1.6) rot=(0,0,-1;1.5708rad)
  shape: bbox 1.7 x 1.54 x 0.15 mm, 10 faces (baked)
FEATURE [Part::Feature] Part__Feature381  label="ICM-20948-9axis-IMU v027"
  Placement = pos=(-0.10588,0.00770028,1.6) rot=(0,0,-1;1.5708rad)
  shape: bbox 3 x 3 x 1 mm, 177 faces (baked)
FEATURE [App::Part] ICM_20948_9axis_IMU_v2  label="ICM-20948-9axis-IMU v028"
  Group = -> [Part__Feature356,Part__Feature357,Part__Feature358,Part__Feature359,Part__Feature360,Part__Feature361,Part__Feature362,Part__Feature363,Part__Feature364,Part__Feature365,Part__Feature366,Part__Feature367,Part__Feature368,Part__Feature369,Part__Feature370,Part__Feature371,Part__Feature372,Part__Feature373,Part__Feature374,Part__Feature375,Part__Feature376,Part__Feature377,Part__Feature378,+3 more]
  Origin = -> Origin051
FEATURE [Part::Feature] Part__Feature382  label="SOT23-5 v1"
  Placement = pos=(-5.22064,-0.331862,1.57965) rot=(0,0,-1;1.5708rad)
  shape: bbox 3 x 1.65 x 1.1 mm, 34 faces (baked)
FEATURE [Part::Feature] Part__Feature383  label="SOT23-5 v002"
  Placement = pos=(-5.22064,-0.331862,1.57965) rot=(0,0,-1;1.5708rad)
  shape: bbox 0.6 x 0.6498 x 0.8933 mm, 7 faces (baked)
FEATURE [Part::Feature] Part__Feature384  label="SOT23-5 v003"
  Placement = pos=(-5.22064,-0.331862,1.57965) rot=(0,0,-1;1.5708rad)
  shape: bbox 0.6 x 0.6498 x 0.8933 mm, 7 faces (baked)
FEATURE [Part::Feature] Part__Feature385  label="SOT23-5 v004"
  Placement = pos=(-5.22064,-0.331862,1.57965) rot=(0,0,-1;1.5708rad)
  shape: bbox 0.6 x 0.6498 x 0.8933 mm, 7 faces (baked)
FEATURE [Part::Feature] Part__Feature386  label="SOT23-5 v005"
  Placement = pos=(-5.22064,-0.331862,1.57965) rot=(0,0,-1;1.5708rad)
  shape: bbox 0.6 x 0.6498 x 0.8933 mm, 7 faces (baked)
FEATURE [Part::Feature] Part__Feature387  label="SOT23-5 v006"
  Placement = pos=(-5.22064,-0.331862,1.57965) rot=(0,0,-1;1.5708rad)
  shape: bbox 0.6 x 0.6498 x 0.8933 mm, 7 faces (baked)
FEATURE [Part::Feature] Part__Feature388  label="COMPOUND020"
  shape: bbox 0.28 x 0.28 x 2e-07 mm, 1 faces, 0 solids (baked)
FEATURE [Part::Feature] Part__Feature389  label="COMPOUND001"
  shape: bbox 1.155 x 2.1 x 0.77 mm, 34 faces, 0 solids (baked)
FEATURE [App::Part] COMPOUND  label="COMPOUND002"
  Group = -> [Part__Feature388,Part__Feature389]
  Origin = -> Origin053
FEATURE [Part::Feature] Part__Feature390  label="COMPOUND003"
  shape: bbox 0.4549 x 0.42 x 0.6253 mm, 7 faces (baked)
FEATURE [Part::Feature] Part__Feature391  label="COMPOUND004"
  shape: bbox 0.4549 x 0.42 x 0.6253 mm, 7 faces (baked)
FEATURE [Part::Feature] Part__Feature392  label="COMPOUND005"
  shape: bbox 0.4549 x 0.42 x 0.6253 mm, 7 faces (baked)
FEATURE [Part::Feature] Part__Feature393  label="COMPOUND006"
  shape: bbox 0.4549 x 0.42 x 0.6253 mm, 7 faces (baked)
FEATURE [Part::Feature] Part__Feature394  label="COMPOUND007"
  shape: bbox 0.4549 x 0.42 x 0.6253 mm, 7 faces (baked)
FEATURE [Part::Feature] Part__Feature395  label="COMPOUND008"
  shape: bbox 0.4549 x 0.42 x 0.6253 mm, 7 faces (baked)
FEATURE [App::Part] COMPOUND001  label="COMPOUND009"
  Group = -> [Part__Feature390,Part__Feature391,Part__Feature392,Part__Feature393,Part__Feature394,Part__Feature395]
  Origin = -> Origin054
FEATURE [Part::Feature] Part__Feature396  label="COMPOUND010"
  shape: bbox 0.28 x 0.28 x 2e-07 mm, 1 faces, 0 solids (baked)
FEATURE [Part::Feature] Part__Feature397  label="COMPOUND011"
  shape: bbox 1.155 x 2.1 x 0.77 mm, 34 faces, 0 solids (baked)
FEATURE [App::Part] COMPOUND002  label="COMPOUND012"
  Group = -> [Part__Feature396,Part__Feature397]
  Origin = -> Origin056
FEATURE [Part::Feature] Part__Feature398  label="COMPOUND013"
  shape: bbox 0.4549 x 0.42 x 0.6253 mm, 7 faces (baked)
FEATURE [Part::Feature] Part__Feature399  label="COMPOUND014"
  shape: bbox 0.4549 x 0.42 x 0.6253 mm, 7 faces (baked)
FEATURE [Part::Feature] Part__Feature400  label="COMPOUND015"
  shape: bbox 0.4549 x 0.42 x 0.6253 mm, 7 faces (baked)
FEATURE [Part::Feature] Part__Feature401  label="COMPOUND016"
  shape: bbox 0.4549 x 0.42 x 0.6253 mm, 7 faces (baked)
FEATURE [Part::Feature] Part__Feature402  label="COMPOUND017"
  shape: bbox 0.4549 x 0.42 x 0.6253 mm, 7 faces (baked)
FEATURE [Part::Feature] Part__Feature403  label="COMPOUND018"
  shape: bbox 0.4549 x 0.42 x 0.6253 mm, 7 faces (baked)
FEATURE [App::Part] COMPOUND003  label="COMPOUND019"
  Group = -> [Part__Feature398,Part__Feature399,Part__Feature400,Part__Feature401,Part__Feature402,Part__Feature403]
  Origin = -> Origin057
FEATURE [Part::Feature] Part__Feature404  label="LED 0603 single color v1"
  Placement = pos=(-9.1591,3.69227,1.60762) rot=(0,0,1;1.5708rad)
  shape: bbox 0.508 x 0.5866 x 0.00762 mm, 5 faces (baked)
FEATURE [Part::Feature] Part__Feature405  label="LED 0603 single color v002"
  Placement = pos=(-9.1591,3.69227,1.60762) rot=(0,0,1;1.5708rad)
  shape: bbox 0.6279 x 0.7678 x 0.3665 mm, 16 faces (baked)
FEATURE [Part::Feature] Part__Feature406  label="LED 0603 single color v003"
  Placement = pos=(-9.1591,3.69227,1.60762) rot=(0,0,1;1.5708rad)
  shape: bbox 0.6279 x 0.7678 x 0.3665 mm, 16 faces (baked)
FEATURE [Part::Feature] Part__Feature407  label="LED 0603 single color v004"
  Placement = pos=(-9.1591,3.69227,1.60762) rot=(0,0,1;1.5708rad)
  shape: bbox 1.961 x 0.7932 x 0.3601 mm, 18 faces (baked)
FEATURE [Part::Feature] Part__Feature408  label="LED 0603 single color v007"
  Placement = pos=(-9.1591,3.69227,1.60762) rot=(0,0,1;1.5708rad)
  shape: bbox 1.092 x 0.7874 x 0.4064 mm, 8 faces (baked)
FEATURE [App::Part] LED_0603_single_color_v1  label="LED 0603 single color v006"
  Group = -> [Part__Feature404,Part__Feature405,Part__Feature406,Part__Feature407,Part__Feature408]
  Origin = -> Origin059
FEATURE [Part::Feature] Part__Feature409  label="Cathode"
  shape: bbox 1.4 x 0.65 x 0.7 mm, 14 faces (baked)
FEATURE [Part::Feature] Part__Feature410  label="Anode"
  shape: bbox 1.4 x 0.65 x 0.7 mm, 14 faces (baked)
FEATURE [Part::Feature] Part__Feature411  label="Cathode Bar"
  shape: bbox 0.3 x 1.3 x 0.01 mm, 6 faces (baked)
FEATURE [Part::Feature] Part__Feature412  label="Body008"
  shape: bbox 1.95 x 1.5 x 1.05 mm, 38 faces (baked)
FEATURE [Part::Feature] Part__Feature413  label="CAPC-0603-T0.9-BN v1"
  Placement = pos=(-1.65403,3.12991,1.6) rot=(0,0,1;0rad)
  shape: bbox 1.7 x 0.9 x 0.9 mm, 42 faces (baked)
FEATURE [Part::Feature] Part__Feature414  label="CAPC-0603-T0.9-BN v002"
  Placement = pos=(-2.94143,-0.250998,1.6) rot=(0,0,1;1.5708rad)
  shape: bbox 0.9 x 1.7 x 0.9 mm, 42 faces (baked)
FEATURE [Part::Feature] Part__Feature415  label="CAPC-0805-T0.95-BN v1"
  Placement = pos=(-4.93215,2.96802,1.6) rot=(0,0,1;0rad)
  shape: bbox 2.1 x 1.35 x 0.95 mm, 42 faces (baked)
FEATURE [Part::Feature] Part__Feature416  label="CAPC-0805-T0.95-BN v002"
  Placement = pos=(-6.10128,-3.2862,1.6) rot=(0,0,1;0rad)
  shape: bbox 2.1 x 1.35 x 0.95 mm, 42 faces (baked)
FEATURE [Part::Feature] Part__Feature417  label="RESC-0603 v1"
  Placement = pos=(-7.25133,3.55479,1.6) rot=(0,0,-1;1.5708rad)
  shape: bbox 0.9 x 0.4 x 0.53 mm, 18 faces (baked)
FEATURE [Part::Feature] Part__Feature418  label="RESC-0603 v002"
  Placement = pos=(-7.25133,3.55479,1.6) rot=(0,0,-1;1.5708rad)
  shape: bbox 0.9 x 0.4 x 0.53 mm, 18 faces (baked)
FEATURE [Part::Feature] Part__Feature419  label="RESC-0603 v003"
  Placement = pos=(-7.25133,3.55479,1.6) rot=(0,0,-1;1.5708rad)
  shape: bbox 0.9 x 1.64 x 0.52 mm, 16 faces (baked)
FEATURE [Part::Feature] Part__Feature420  label="RESC-0603 v005"
  Placement = pos=(-2.6456,-3.67699,1.6) rot=(0,0,1;0rad)
  shape: bbox 0.4 x 0.9 x 0.53 mm, 18 faces (baked)
FEATURE [Part::Feature] Part__Feature421  label="RESC-0603 v006"
  Placement = pos=(-2.6456,-3.67699,1.6) rot=(0,0,1;0rad)
  shape: bbox 0.4 x 0.9 x 0.53 mm, 18 faces (baked)
FEATURE [Part::Feature] Part__Feature422  label="RESC-0603 v009"
  Placement = pos=(-2.6456,-3.67699,1.6) rot=(0,0,1;0rad)
  shape: bbox 1.64 x 0.9 x 0.52 mm, 16 faces (baked)
FEATURE [Part::Feature] Part__Feature423  label="YC164_RESPACK v1"
  Placement = pos=(3.93663,0.00430864,1.6) rot=(0,0,-1;1.5708rad)
  shape: bbox 1.6 x 3.2 x 0.61 mm, 172 faces (baked)
FEATURE [Part::Feature] Part__Feature424  label="YC164_RESPACK v002"
  Placement = pos=(3.66041,4.82408,1.6) rot=(0,0,-1;1.5708rad)
  shape: bbox 1.6 x 3.2 x 0.61 mm, 172 faces (baked)
FEATURE [Part::Feature] Part__Feature425  label="qwicc v1"
  Placement = pos=(-8.62344,0.00769078,1.295) rot=(0.57735,-0.57735,-0.57735;2.0944rad)
  shape: bbox 1.5 x 0.2 x 1.25 mm, 25 faces (baked)
FEATURE [Part::Feature] Part__Feature426  label="qwicc v002"
  Placement = pos=(-8.62344,0.00769078,1.295) rot=(0.57735,-0.57735,-0.57735;2.0944rad)
  shape: bbox 3.7 x 0.2 x 2.46 mm, 20 faces (baked)
FEATURE [Part::Feature] Part__Feature427  label="qwicc v003"
  Placement = pos=(-8.62344,0.00769078,1.295) rot=(0.57735,-0.57735,-0.57735;2.0944rad)
  shape: bbox 3.7 x 0.2 x 2.46 mm, 20 faces (baked)
FEATURE [Part::Feature] Part__Feature428  label="qwicc v004"
  Placement = pos=(-8.62344,0.00769078,1.295) rot=(0.57735,-0.57735,-0.57735;2.0944rad)
  shape: bbox 3.7 x 0.2 x 2.46 mm, 20 faces (baked)
FEATURE [Part::Feature] Part__Feature429  label="qwicc v005"
  Placement = pos=(-8.62344,0.00769078,1.295) rot=(0.57735,-0.57735,-0.57735;2.0944rad)
  shape: bbox 1.5 x 0.2 x 1.25 mm, 25 faces (baked)
FEATURE [Part::Feature] Part__Feature430  label="qwicc v006"
  Placement = pos=(-8.62344,0.00769078,1.295) rot=(0.57735,-0.57735,-0.57735;2.0944rad)
  shape: bbox 3.7 x 0.2 x 2.46 mm, 20 faces (baked)
FEATURE [Part::Feature] Part__Feature431  label="qwicc v007"
  Placement = pos=(-8.62344,0.00769078,1.295) rot=(0.57735,-0.57735,-0.57735;2.0944rad)
  shape: bbox 4.25 x 6 x 2.9 mm, 99 faces (baked)
FEATURE [Part::Feature] Part__Feature432  label="qwicc v011"
  Placement = pos=(8.56116,0.0089391,1.295) rot=(0.57735,0.57735,0.57735;2.0944rad)
  shape: bbox 1.5 x 0.2 x 1.25 mm, 25 faces (baked)
FEATURE [Part::Feature] Part__Feature433  label="qwicc v012"
  Placement = pos=(8.56116,0.0089391,1.295) rot=(0.57735,0.57735,0.57735;2.0944rad)
  shape: bbox 3.7 x 0.2 x 2.46 mm, 20 faces (baked)
FEATURE [Part::Feature] Part__Feature434  label="qwicc v013"
  Placement = pos=(8.56116,0.0089391,1.295) rot=(0.57735,0.57735,0.57735;2.0944rad)
  shape: bbox 3.7 x 0.2 x 2.46 mm, 20 faces (baked)
FEATURE [Part::Feature] Part__Feature435  label="qwicc v014"
  Placement = pos=(8.56116,0.0089391,1.295) rot=(0.57735,0.57735,0.57735;2.0944rad)
  shape: bbox 3.7 x 0.2 x 2.46 mm, 20 faces (baked)
FEATURE [Part::Feature] Part__Feature436  label="qwicc v015"
  Placement = pos=(8.56116,0.0089391,1.295) rot=(0.57735,0.57735,0.57735;2.0944rad)
  shape: bbox 1.5 x 0.2 x 1.25 mm, 25 faces (baked)
FEATURE [Part::Feature] Part__Feature437  label="qwicc v016"
  Placement = pos=(8.56116,0.0089391,1.295) rot=(0.57735,0.57735,0.57735;2.0944rad)
  shape: bbox 3.7 x 0.2 x 2.46 mm, 20 faces (baked)
FEATURE [Part::Feature] Part__Feature438  label="qwicc v017"
  Placement = pos=(8.56116,0.0089391,1.295) rot=(0.57735,0.57735,0.57735;2.0944rad)
  shape: bbox 4.25 x 6 x 2.9 mm, 99 faces (baked)
FEATURE [App::Part] RESC_0603_v002  label="RESC-0603 v010"
  Group = -> [Part__Feature420,Part__Feature421,Part__Feature422]
  Origin = -> Origin063
FEATURE [App::Part] RESC_0603_v1  label="RESC-0603 v004"
  Group = -> [Part__Feature417,Part__Feature418,Part__Feature419]
  Origin = -> Origin062
FEATURE [App::Part] SOD_323  label="SOD-323"
  Group = -> [Part__Feature409,Part__Feature410,Part__Feature411,Part__Feature412]
  Origin = -> Origin060
FEATURE [App::Part] SOD_323_v1  label="SOD-323 v1"
  Group = -> [SOD_323]
  Origin = -> Origin061
  Placement = pos=(7.02114,3.54357,1.6) rot=(0,0,1;1.5708rad)
FEATURE [App::Part] SOT23_5_v1  label="SOT23-5 v007"
  Group = -> [Part__Feature382,Part__Feature383,Part__Feature384,Part__Feature385,Part__Feature386,Part__Feature387]
  Origin = -> Origin052
FEATURE [App::Part] SOT23_6_v004  label="SOT23-6 v004"
  Group = -> [COMPOUND002,COMPOUND003]
  Origin = -> Origin058
  Placement = pos=(1.87935,3.54648,1.22426) rot=(0,0,1;0rad)
FEATURE [App::Part] SOT23_6_v3  label="SOT23-6 v3"
  Group = -> [COMPOUND,COMPOUND001]
  Origin = -> Origin055
  Placement = pos=(2.41278,-3.39005,1.22426) rot=(0,0,1;3.14159rad)
FEATURE [App::Part] qwicc_v002  label="qwicc v018"
  Group = -> [Part__Feature432,Part__Feature433,Part__Feature434,Part__Feature435,Part__Feature436,Part__Feature437,Part__Feature438]
  Origin = -> Origin065
FEATURE [App::Part] qwicc_v1  label="qwicc v008"
  Group = -> [Part__Feature425,Part__Feature426,Part__Feature427,Part__Feature428,Part__Feature429,Part__Feature430,Part__Feature431]
  Origin = -> Origin064
FEATURE [App::Part] Adafruit_ICM20948_STEMMA_QT_v4  label="Gyro"
  Group = -> [Part__Feature355,ICM_20948_9axis_IMU_v2,SOT23_5_v1,SOT23_6_v3,SOT23_6_v004,LED_0603_single_color_v1,SOD_323_v1,Part__Feature413,Part__Feature414,Part__Feature415,Part__Feature416,RESC_0603_v1,RESC_0603_v002,Part__Feature423,Part__Feature424,qwicc_v1,qwicc_v002]
  Origin = -> Origin066
  Placement = pos=(77.5,-99.65,-146.5) rot=(0,0,1;0rad)
FEATURE [Part::Feature] Part__Feature439  label="PCB, Raspberry Pi Zero 2 W"
  shape: bbox 65 x 1.6 x 30 mm, 230 faces (baked)
FEATURE [Part::Feature] Part__Feature440  label="RP3A0-AU 2105 201221C, Raspberry Pi Zero 2 W"
  Placement = pos=(-5.5,0.8,1) rot=(0,0,1;0rad)
  shape: bbox 15 x 1 x 15 mm, 6 faces (baked)
FEATURE [Part::Feature] Part__Feature441  label="MicroUSB Port, Raspberry Pi Zero 2 W"
  Placement = pos=(8.9,0.8,13) rot=(0,0,1;0rad)
  shape: bbox 8.008 x 2.958 x 5.47 mm, 784 faces (baked)
FEATURE [Part::Feature] Part__Feature442  label="MicroUSB Port, Raspberry Pi Zero 2 W001"
  Placement = pos=(8.9,0.8,13) rot=(0,0,1;0rad)
  shape: bbox 6.984 x 2.156 x 3.939 mm, 206 faces (baked)
FEATURE [Part::Feature] Part__Feature443  label="MicroUSB Port, Raspberry Pi Zero 2 W002"
  Placement = pos=(8.9,0.8,13) rot=(0,0,1;0rad)
  shape: bbox 0.37 x 1.716 x 4 mm, 43 faces (baked)
FEATURE [Part::Feature] Part__Feature444  label="MicroUSB Port, Raspberry Pi Zero 2 W003"
  Placement = pos=(8.9,0.8,13) rot=(0,0,1;0rad)
  shape: bbox 0.37 x 1.716 x 4 mm, 43 faces (baked)
FEATURE [Part::Feature] Part__Feature445  label="MicroUSB Port, Raspberry Pi Zero 2 W004"
  Placement = pos=(8.9,0.8,13) rot=(0,0,1;0rad)
  shape: bbox 0.37 x 1.716 x 4 mm, 43 faces (baked)
FEATURE [Part::Feature] Part__Feature446  label="MicroUSB Port, Raspberry Pi Zero 2 W005"
  Placement = pos=(8.9,0.8,13) rot=(0,0,1;0rad)
  shape: bbox 0.37 x 1.716 x 4 mm, 43 faces (baked)
FEATURE [Part::Feature] Part__Feature447  label="MicroUSB Port, Raspberry Pi Zero 2 W006"
  Placement = pos=(8.9,0.8,13) rot=(0,0,1;0rad)
  shape: bbox 0.37 x 1.716 x 4 mm, 43 faces (baked)
FEATURE [App::Part] MicroUSB_Port__Raspberry_Pi_Zero_2_W  label="MicroUSB Port, Raspberry Pi Zero 2 W007"
  Group = -> [Part__Feature441,Part__Feature442,Part__Feature443,Part__Feature444,Part__Feature445,Part__Feature446,Part__Feature447]
  Origin = -> Origin067
FEATURE [Part::Feature] Part__Feature448  label="SD Card Slot, Raspberry Pi Zero 2 W"
  Placement = pos=(-25.5,0.8,-2) rot=(0,-1,0;1.5708rad)
  shape: bbox 11.4 x 1.45 x 11.95 mm, 216 faces (baked)
FEATURE [Part::Feature] Part__Feature449  label="SD Card Slot, Raspberry Pi Zero 2 W001"
  Placement = pos=(-25.5,0.8,-2) rot=(0,-1,0;1.5708rad)
  shape: bbox 7.946 x 0.8923 x 0.34 mm, 22 faces (baked)
FEATURE [Part::Feature] Part__Feature450  label="SD Card Slot, Raspberry Pi Zero 2 W002"
  Placement = pos=(-25.5,0.8,-2) rot=(0,-1,0;1.5708rad)
  shape: bbox 7.946 x 0.8923 x 0.34 mm, 22 faces (baked)
FEATURE [Part::Feature] Part__Feature451  label="SD Card Slot, Raspberry Pi Zero 2 W003"
  Placement = pos=(-25.5,0.8,-2) rot=(0,-1,0;1.5708rad)
  shape: bbox 7.946 x 0.8923 x 0.34 mm, 22 faces (baked)
FEATURE [Part::Feature] Part__Feature452  label="SD Card Slot, Raspberry Pi Zero 2 W004"
  Placement = pos=(-25.5,0.8,-2) rot=(0,-1,0;1.5708rad)
  shape: bbox 7.946 x 0.8923 x 0.34 mm, 22 faces (baked)
FEATURE [Part::Feature] Part__Feature453  label="SD Card Slot, Raspberry Pi Zero 2 W005"
  Placement = pos=(-25.5,0.8,-2) rot=(0,-1,0;1.5708rad)
  shape: bbox 7.946 x 0.8923 x 0.34 mm, 22 faces (baked)
FEATURE [Part::Feature] Part__Feature454  label="SD Card Slot, Raspberry Pi Zero 2 W006"
  Placement = pos=(-25.5,0.8,-2) rot=(0,-1,0;1.5708rad)
  shape: bbox 7.946 x 0.8923 x 0.34 mm, 22 faces (baked)
FEATURE [Part::Feature] Part__Feature455  label="SD Card Slot, Raspberry Pi Zero 2 W007"
  Placement = pos=(-25.5,0.8,-2) rot=(0,-1,0;1.5708rad)
  shape: bbox 7.946 x 0.8923 x 0.34 mm, 22 faces (baked)
FEATURE [Part::Feature] Part__Feature456  label="SD Card Slot, Raspberry Pi Zero 2 W008"
  Placement = pos=(-25.5,0.8,-2) rot=(0,-1,0;1.5708rad)
  shape: bbox 7.946 x 0.8923 x 0.34 mm, 22 faces (baked)
FEATURE [Part::Feature] Part__Feature457  label="SD Card Slot, Raspberry Pi Zero 2 W009"
  Placement = pos=(-25.5,0.8,-2) rot=(0,-1,0;1.5708rad)
  shape: bbox 10.28 x 1.3 x 11.71 mm, 80 faces (baked)
FEATURE [Part::Feature] Part__Feature458  label="Wireless Module Cover, Raspberry Pi Zero 2 W"
  Placement = pos=(11,0.8,1.5) rot=(0,0,1;0rad)
  shape: bbox 12.6 x 1.6 x 12.6 mm, 70 faces (baked)
FEATURE [Part::Feature] Part__Feature459  label="Crystal Resonator, Raspberry Pi Zero 2 W"
  Placement = pos=(-17.5,0.8,-1.5) rot=(0,0,1;0rad)
  shape: bbox 2.2 x 0.6 x 3.2 mm, 18 faces (baked)
FEATURE [Part::Feature] Part__Feature460  label="LED, Raspberry Pi Zero 2 W"
  Placement = pos=(27.5,0.8,7.8) rot=(0,0,1;0rad)
  shape: bbox 1.2 x 0.4 x 0.8 mm, 6 faces (baked)
FEATURE [Part::Feature] Part__Feature461  label="Diode, Schottky, Raspberry Pi Zero 2 W"
  Placement = pos=(-11,0.8,12) rot=(0,0,1;0rad)
  shape: bbox 1.8 x 1 x 3.7 mm, 14 faces (baked)
FEATURE [Part::Feature] Part__Feature462  label="54548-2271, 22 Pin FPC Connector, Raspberry Pi Zero 2 W"
  Placement = pos=(28.75,0.82,0) rot=(0,1,0;1.5708rad)
  shape: bbox 5 x 1.2 x 16.2 mm, 1331 faces (baked)
FEATURE [Part::Feature] Part__Feature463  label="Mini HDMI Receptacle Port, Raspberry Pi Zero 2 W"
  Placement = pos=(-20.1,2.65,15) rot=(0,0,1;0rad)
  shape: bbox 12.9 x 4.054 x 7.704 mm, 656 faces (baked)
FEATURE [Part::Feature] Part__Feature464  label="PAM2306AYPKE, Switching Voltage Regulators Dual PWM Step-Down 40uA 1A
 1.5MHz, Raspberry Pi Zero 2 W"
  Placement = pos=(23,0.8,1) rot=(0,-1,0;1.5708rad)
  shape: bbox 3 x 1.002 x 3.4 mm, 217 faces (baked)
FEATURE [Part::Feature] Part__Feature465  label="RT9081A-1BGQZA, Fixed LDO Voltage Regulator, 0.8V-5.5Vin, 140mV drop,
 1.25Vout, 0.5Aout, Raspberry Pi Zero 2 W_default"
  Placement = pos=(14.8,0.8,-7.2) rot=(0,0,1;0rad)
  shape: bbox 1.2 x 0.1 x 1.2 mm, 6 faces (baked)
FEATURE [Part::Feature] Part__Feature466  label="RT8088AWSC, IC Reg Buck Prog 3A Sync 15WLCSP, Raspberry Pi Zero 2 W_d
efault"
  Placement = pos=(20,0.8,-3.6) rot=(0,0,1;0rad)
  shape: bbox 1.36 x 0.4 x 2.16 mm, 6 faces (baked)
FEATURE [Part::Feature] Part__Feature467  label="SMD Inductor, Configurable, Raspberry Pi Zero 2 W_L1"
  Placement = pos=(20.5,0.8,7.5) rot=(0,0,1;0rad)
  shape: bbox 4 x 1.8 x 4 mm, 6 faces (baked)
FEATURE [Part::Feature] Part__Feature468  label="SMD Inductor, Configurable, Raspberry Pi Zero 2 W_L2"
  Placement = pos=(24.5,0.8,-2) rot=(0,0,1;0rad)
  shape: bbox 2.5 x 1.2 x 2 mm, 6 faces (baked)
FEATURE [Part::Feature] Part__Feature469  label="SMD Capacitor, Configurable, Raspberry Pi Zero 2 W_C1"
  Placement = pos=(24.9,0.8,7.7) rot=(0,0,1;0rad)
  shape: bbox 1.2 x 0.45 x 1.2 mm, 6 faces (baked)
FEATURE [Part::Feature] Part__Feature470  label="SMD Capacitor, Configurable, Raspberry Pi Zero 2 W_C002"
  Placement = pos=(24.9,0.8,7.7) rot=(0,0,1;0rad)
  shape: bbox 1.2 x 0.45 x 0.4 mm, 6 faces (baked)
FEATURE [Part::Feature] Part__Feature471  label="SMD Capacitor, Configurable, Raspberry Pi Zero 2 W_C003"
  Placement = pos=(24.9,0.8,7.7) rot=(0,0,1;0rad)
  shape: bbox 1.2 x 0.45 x 0.4 mm, 6 faces (baked)
FEATURE [Part::Feature] Part__Feature472  label="MicroUSB Port, Raspberry Pi Zero 2 W008"
  Placement = pos=(21.5,0.8,13) rot=(0,0,1;0rad)
  shape: bbox 8.008 x 2.958 x 5.47 mm, 784 faces (baked)
FEATURE [Part::Feature] Part__Feature473  label="MicroUSB Port, Raspberry Pi Zero 2 W009"
  Placement = pos=(21.5,0.8,13) rot=(0,0,1;0rad)
  shape: bbox 6.984 x 2.156 x 3.939 mm, 206 faces (baked)
FEATURE [Part::Feature] Part__Feature474  label="MicroUSB Port, Raspberry Pi Zero 2 W010"
  Placement = pos=(21.5,0.8,13) rot=(0,0,1;0rad)
  shape: bbox 0.37 x 1.716 x 4 mm, 43 faces (baked)
FEATURE [Part::Feature] Part__Feature475  label="MicroUSB Port, Raspberry Pi Zero 2 W011"
  Placement = pos=(21.5,0.8,13) rot=(0,0,1;0rad)
  shape: bbox 0.37 x 1.716 x 4 mm, 43 faces (baked)
FEATURE [Part::Feature] Part__Feature476  label="MicroUSB Port, Raspberry Pi Zero 2 W012"
  Placement = pos=(21.5,0.8,13) rot=(0,0,1;0rad)
  shape: bbox 0.37 x 1.716 x 4 mm, 43 faces (baked)
FEATURE [Part::Feature] Part__Feature477  label="MicroUSB Port, Raspberry Pi Zero 2 W013"
  Placement = pos=(21.5,0.8,13) rot=(0,0,1;0rad)
  shape: bbox 0.37 x 1.716 x 4 mm, 43 faces (baked)
FEATURE [Part::Feature] Part__Feature478  label="MicroUSB Port, Raspberry Pi Zero 2 W014"
  Placement = pos=(21.5,0.8,13) rot=(0,0,1;0rad)
  shape: bbox 0.37 x 1.716 x 4 mm, 43 faces (baked)
FEATURE [App::Part] MicroUSB_Port__Raspberry_Pi_Zero_2_W001  label="MicroUSB Port, Raspberry Pi Zero 2 W015"
  Group = -> [Part__Feature472,Part__Feature473,Part__Feature474,Part__Feature475,Part__Feature476,Part__Feature477,Part__Feature478]
  Origin = -> Origin070
FEATURE [Part::Feature] Part__Feature479  label="SMD Capacitor, Configurable, Raspberry Pi Zero 2 W_C3"
  Placement = pos=(20.5,0.8,3) rot=(0,0,1;0rad)
  shape: bbox 0.85 x 0.45 x 1 mm, 6 faces (baked)
FEATURE [Part::Feature] Part__Feature480  label="SMD Capacitor, Configurable, Raspberry Pi Zero 2 W_C005"
  Placement = pos=(20.5,0.8,3) rot=(0,0,1;0rad)
  shape: bbox 0.85 x 0.45 x 0.275 mm, 6 faces (baked)
FEATURE [Part::Feature] Part__Feature481  label="SMD Capacitor, Configurable, Raspberry Pi Zero 2 W_C006"
  Placement = pos=(20.5,0.8,3) rot=(0,0,1;0rad)
  shape: bbox 0.85 x 0.45 x 0.275 mm, 6 faces (baked)
FEATURE [Part::Feature] Part__Feature482  label="SMD Capacitor, Configurable, Raspberry Pi Zero 2 W_C008"
  Placement = pos=(18.7,0.8,3) rot=(0,0,1;0rad)
  shape: bbox 0.85 x 0.45 x 1 mm, 6 faces (baked)
FEATURE [Part::Feature] Part__Feature483  label="SMD Capacitor, Configurable, Raspberry Pi Zero 2 W_C009"
  Placement = pos=(18.7,0.8,3) rot=(0,0,1;0rad)
  shape: bbox 0.85 x 0.45 x 0.275 mm, 6 faces (baked)
FEATURE [Part::Feature] Part__Feature484  label="SMD Capacitor, Configurable, Raspberry Pi Zero 2 W_C010"
  Placement = pos=(18.7,0.8,3) rot=(0,0,1;0rad)
  shape: bbox 0.85 x 0.45 x 0.275 mm, 6 faces (baked)
FEATURE [Part::Feature] Part__Feature485  label="SMD Capacitor, Configurable, Raspberry Pi Zero 2 W_C012"
  Placement = pos=(27.3,0.8,2.2) rot=(0,0,1;0rad)
  shape: bbox 1.2 x 0.45 x 1.2 mm, 6 faces (baked)
FEATURE [Part::Feature] Part__Feature486  label="SMD Capacitor, Configurable, Raspberry Pi Zero 2 W_C013"
  Placement = pos=(27.3,0.8,2.2) rot=(0,0,1;0rad)
  shape: bbox 1.2 x 0.45 x 0.4 mm, 6 faces (baked)
FEATURE [Part::Feature] Part__Feature487  label="SMD Capacitor, Configurable, Raspberry Pi Zero 2 W_C014"
  Placement = pos=(27.3,0.8,2.2) rot=(0,0,1;0rad)
  shape: bbox 1.2 x 0.45 x 0.4 mm, 6 faces (baked)
FEATURE [Part::Feature] Part__Feature488  label="SMD Capacitor, Configurable, Raspberry Pi Zero 2 W_C016"
  Placement = pos=(25.7,0.8,2.2) rot=(0,0,1;0rad)
  shape: bbox 0.85 x 0.45 x 1 mm, 6 faces (baked)
FEATURE [Part::Feature] Part__Feature489  label="SMD Capacitor, Configurable, Raspberry Pi Zero 2 W_C017"
  Placement = pos=(25.7,0.8,2.2) rot=(0,0,1;0rad)
  shape: bbox 0.85 x 0.45 x 0.275 mm, 6 faces (baked)
FEATURE [Part::Feature] Part__Feature490  label="SMD Capacitor, Configurable, Raspberry Pi Zero 2 W_C018"
  Placement = pos=(25.7,0.8,2.2) rot=(0,0,1;0rad)
  shape: bbox 0.85 x 0.45 x 0.275 mm, 6 faces (baked)
FEATURE [Part::Feature] Part__Feature491  label="SMD Capacitor, Configurable, Raspberry Pi Zero 2 W_C020"
  Placement = pos=(22.8,0.8,-5.1) rot=(0,1,0;1.5708rad)
  shape: bbox 1.2 x 0.45 x 1.2 mm, 6 faces (baked)
FEATURE [Part::Feature] Part__Feature492  label="SMD Capacitor, Configurable, Raspberry Pi Zero 2 W_C021"
  Placement = pos=(22.8,0.8,-5.1) rot=(0,1,0;1.5708rad)
  shape: bbox 0.4 x 0.45 x 1.2 mm, 6 faces (baked)
FEATURE [Part::Feature] Part__Feature493  label="SMD Capacitor, Configurable, Raspberry Pi Zero 2 W_C022"
  Placement = pos=(22.8,0.8,-5.1) rot=(0,1,0;1.5708rad)
  shape: bbox 0.4 x 0.45 x 1.2 mm, 6 faces (baked)
FEATURE [Part::Feature] Part__Feature494  label="SMD Capacitor, Configurable, Raspberry Pi Zero 2 W_C024"
  Placement = pos=(20,0.8,-6.4) rot=(0,1,0;1.5708rad)
  shape: bbox 1 x 0.45 x 0.85 mm, 6 faces (baked)
FEATURE [Part::Feature] Part__Feature495  label="SMD Capacitor, Configurable, Raspberry Pi Zero 2 W_C025"
  Placement = pos=(20,0.8,-6.4) rot=(0,1,0;1.5708rad)
  shape: bbox 0.275 x 0.45 x 0.85 mm, 6 faces (baked)
FEATURE [Part::Feature] Part__Feature496  label="SMD Capacitor, Configurable, Raspberry Pi Zero 2 W_C026"
  Placement = pos=(20,0.8,-6.4) rot=(0,1,0;1.5708rad)
  shape: bbox 0.275 x 0.45 x 0.85 mm, 6 faces (baked)
FEATURE [Part::Feature] Part__Feature497  label="SMD Capacitor, Configurable, Raspberry Pi Zero 2 W_C028"
  Placement = pos=(15.8,0.8,-6.1) rot=(0,1,0;1.5708rad)
  shape: bbox 1 x 0.45 x 0.85 mm, 6 faces (baked)
FEATURE [Part::Feature] Part__Feature498  label="SMD Capacitor, Configurable, Raspberry Pi Zero 2 W_C029"
  Placement = pos=(15.8,0.8,-6.1) rot=(0,1,0;1.5708rad)
  shape: bbox 0.275 x 0.45 x 0.85 mm, 6 faces (baked)
FEATURE [Part::Feature] Part__Feature499  label="SMD Capacitor, Configurable, Raspberry Pi Zero 2 W_C030"
  Placement = pos=(15.8,0.8,-6.1) rot=(0,1,0;1.5708rad)
  shape: bbox 0.275 x 0.45 x 0.85 mm, 6 faces (baked)
FEATURE [Part::Feature] Part__Feature500  label="SMD Capacitor, Configurable, Raspberry Pi Zero 2 W_C032"
  Placement = pos=(13,0.8,-6.1) rot=(0,1,0;1.5708rad)
  shape: bbox 1 x 0.45 x 0.85 mm, 6 faces (baked)
FEATURE [Part::Feature] Part__Feature501  label="SMD Capacitor, Configurable, Raspberry Pi Zero 2 W_C033"
  Placement = pos=(13,0.8,-6.1) rot=(0,1,0;1.5708rad)
  shape: bbox 0.275 x 0.45 x 0.85 mm, 6 faces (baked)
FEATURE [Part::Feature] Part__Feature502  label="SMD Capacitor, Configurable, Raspberry Pi Zero 2 W_C034"
  Placement = pos=(13,0.8,-6.1) rot=(0,1,0;1.5708rad)
  shape: bbox 0.275 x 0.45 x 0.85 mm, 6 faces (baked)
FEATURE [Part::Feature] Part__Feature503  label="SMD Capacitor, Configurable, Raspberry Pi Zero 2 W_C036"
  Placement = pos=(14.8,0.8,12.5) rot=(0,0,1;0rad)
  shape: bbox 0.85 x 0.45 x 1 mm, 6 faces (baked)
FEATURE [Part::Feature] Part__Feature504  label="SMD Capacitor, Configurable, Raspberry Pi Zero 2 W_C037"
  Placement = pos=(14.8,0.8,12.5) rot=(0,0,1;0rad)
  shape: bbox 0.85 x 0.45 x 0.275 mm, 6 faces (baked)
FEATURE [Part::Feature] Part__Feature505  label="SMD Capacitor, Configurable, Raspberry Pi Zero 2 W_C038"
  Placement = pos=(14.8,0.8,12.5) rot=(0,0,1;0rad)
  shape: bbox 0.85 x 0.45 x 0.275 mm, 6 faces (baked)
FEATURE [Part::Feature] Part__Feature506  label="SMD Capacitor, Configurable, Raspberry Pi Zero 2 W_C2"
  Placement = pos=(-9.5,0.8,10.4) rot=(0,0,1;0rad)
  shape: bbox 0.3 x 0.25 x 0.4 mm, 6 faces (baked)
FEATURE [Part::Feature] Part__Feature507  label="SMD Capacitor, Configurable, Raspberry Pi Zero 2 W_C040"
  Placement = pos=(-9.5,0.8,10.4) rot=(0,0,1;0rad)
  shape: bbox 0.3 x 0.25 x 0.1 mm, 6 faces (baked)
FEATURE [Part::Feature] Part__Feature508  label="SMD Capacitor, Configurable, Raspberry Pi Zero 2 W_C041"
  Placement = pos=(-9.5,0.8,10.4) rot=(0,0,1;0rad)
  shape: bbox 0.3 x 0.25 x 0.1 mm, 6 faces (baked)
FEATURE [Part::Feature] Part__Feature509  label="SMD Capacitor, Configurable, Raspberry Pi Zero 2 W_C10"
  Placement = pos=(-31.4,0.8,6) rot=(0,0,1;0rad)
  shape: bbox 0.5 x 0.35 x 0.6 mm, 6 faces (baked)
FEATURE [Part::Feature] Part__Feature510  label="SMD Capacitor, Configurable, Raspberry Pi Zero 2 W_C043"
  Placement = pos=(-31.4,0.8,6) rot=(0,0,1;0rad)
  shape: bbox 0.5 x 0.35 x 0.2 mm, 6 faces (baked)
FEATURE [Part::Feature] Part__Feature511  label="SMD Capacitor, Configurable, Raspberry Pi Zero 2 W_C044"
  Placement = pos=(-31.4,0.8,6) rot=(0,0,1;0rad)
  shape: bbox 0.5 x 0.35 x 0.2 mm, 6 faces (baked)
FEATURE [Part::Feature] Part__Feature512  label="SMD Capacitor, Configurable, Raspberry Pi Zero 2 W_C046"
  Placement = pos=(-6.1,0.8,13.7) rot=(0,1,0;1.5708rad)
  shape: bbox 0.6 x 0.35 x 0.5 mm, 6 faces (baked)
FEATURE [Part::Feature] Part__Feature513  label="SMD Capacitor, Configurable, Raspberry Pi Zero 2 W_C047"
  Placement = pos=(-6.1,0.8,13.7) rot=(0,1,0;1.5708rad)
  shape: bbox 0.2 x 0.35 x 0.5 mm, 6 faces (baked)
FEATURE [Part::Feature] Part__Feature514  label="SMD Capacitor, Configurable, Raspberry Pi Zero 2 W_C048"
  Placement = pos=(-6.1,0.8,13.7) rot=(0,1,0;1.5708rad)
  shape: bbox 0.2 x 0.35 x 0.5 mm, 6 faces (baked)
FEATURE [Part::Feature] Part__Feature515  label="SMD Capacitor, Configurable, Raspberry Pi Zero 2 W_C050"
  Placement = pos=(-2.9,0.8,13.7) rot=(0,1,0;1.5708rad)
  shape: bbox 0.6 x 0.35 x 0.5 mm, 6 faces (baked)
FEATURE [Part::Feature] Part__Feature516  label="SMD Capacitor, Configurable, Raspberry Pi Zero 2 W_C051"
  Placement = pos=(-2.9,0.8,13.7) rot=(0,1,0;1.5708rad)
  shape: bbox 0.2 x 0.35 x 0.5 mm, 6 faces (baked)
FEATURE [Part::Feature] Part__Feature517  label="SMD Capacitor, Configurable, Raspberry Pi Zero 2 W_C052"
  Placement = pos=(-2.9,0.8,13.7) rot=(0,1,0;1.5708rad)
  shape: bbox 0.2 x 0.35 x 0.5 mm, 6 faces (baked)
FEATURE [Part::Feature] Part__Feature518  label="SMD Capacitor, Configurable, Raspberry Pi Zero 2 W_C054"
  Placement = pos=(-6.1,0.8,11.9) rot=(0,1,0;1.5708rad)
  shape: bbox 0.6 x 0.35 x 0.5 mm, 6 faces (baked)
FEATURE [Part::Feature] Part__Feature519  label="SMD Capacitor, Configurable, Raspberry Pi Zero 2 W_C055"
  Placement = pos=(-6.1,0.8,11.9) rot=(0,1,0;1.5708rad)
  shape: bbox 0.2 x 0.35 x 0.5 mm, 6 faces (baked)
FEATURE [Part::Feature] Part__Feature520  label="SMD Capacitor, Configurable, Raspberry Pi Zero 2 W_C056"
  Placement = pos=(-6.1,0.8,11.9) rot=(0,1,0;1.5708rad)
  shape: bbox 0.2 x 0.35 x 0.5 mm, 6 faces (baked)
FEATURE [Part::Feature] Part__Feature521  label="SMD Capacitor, Configurable, Raspberry Pi Zero 2 W_C058"
  Placement = pos=(-2.9,0.8,11.9) rot=(0,1,0;1.5708rad)
  shape: bbox 0.6 x 0.35 x 0.5 mm, 6 faces (baked)
FEATURE [Part::Feature] Part__Feature522  label="SMD Capacitor, Configurable, Raspberry Pi Zero 2 W_C059"
  Placement = pos=(-2.9,0.8,11.9) rot=(0,1,0;1.5708rad)
  shape: bbox 0.2 x 0.35 x 0.5 mm, 6 faces (baked)
FEATURE [Part::Feature] Part__Feature523  label="SMD Capacitor, Configurable, Raspberry Pi Zero 2 W_C060"
  Placement = pos=(-2.9,0.8,11.9) rot=(0,1,0;1.5708rad)
  shape: bbox 0.2 x 0.35 x 0.5 mm, 6 faces (baked)
FEATURE [Part::Feature] Part__Feature524  label="SMD Capacitor, Configurable, Raspberry Pi Zero 2 W_C062"
  Placement = pos=(-4.6,0.8,9.5) rot=(0,1,0;1.5708rad)
  shape: bbox 0.6 x 0.35 x 0.5 mm, 6 faces (baked)
FEATURE [Part::Feature] Part__Feature525  label="SMD Capacitor, Configurable, Raspberry Pi Zero 2 W_C063"
  Placement = pos=(-4.6,0.8,9.5) rot=(0,1,0;1.5708rad)
  shape: bbox 0.2 x 0.35 x 0.5 mm, 6 faces (baked)
FEATURE [Part::Feature] Part__Feature526  label="SMD Capacitor, Configurable, Raspberry Pi Zero 2 W_C064"
  Placement = pos=(-4.6,0.8,9.5) rot=(0,1,0;1.5708rad)
  shape: bbox 0.2 x 0.35 x 0.5 mm, 6 faces (baked)
FEATURE [Part::Feature] Part__Feature527  label="SMD Capacitor, Configurable, Raspberry Pi Zero 2 W_C066"
  Placement = pos=(-7.3,0.8,8.9) rot=(0,1,0;1.5708rad)
  shape: bbox 0.6 x 0.35 x 0.5 mm, 6 faces (baked)
FEATURE [Part::Feature] Part__Feature528  label="SMD Capacitor, Configurable, Raspberry Pi Zero 2 W_C067"
  Placement = pos=(-7.3,0.8,8.9) rot=(0,1,0;1.5708rad)
  shape: bbox 0.2 x 0.35 x 0.5 mm, 6 faces (baked)
FEATURE [Part::Feature] Part__Feature529  label="SMD Capacitor, Configurable, Raspberry Pi Zero 2 W_C068"
  Placement = pos=(-7.3,0.8,8.9) rot=(0,1,0;1.5708rad)
  shape: bbox 0.2 x 0.35 x 0.5 mm, 6 faces (baked)
FEATURE [Part::Feature] Part__Feature530  label="SMD Capacitor, Configurable, Raspberry Pi Zero 2 W_C070"
  Placement = pos=(-4.6,0.8,8.8) rot=(0,1,0;1.5708rad)
  shape: bbox 0.4 x 0.25 x 0.3 mm, 6 faces (baked)
FEATURE [Part::Feature] Part__Feature531  label="SMD Capacitor, Configurable, Raspberry Pi Zero 2 W_C071"
  Placement = pos=(-4.6,0.8,8.8) rot=(0,1,0;1.5708rad)
  shape: bbox 0.1 x 0.25 x 0.3 mm, 6 faces (baked)
FEATURE [Part::Feature] Part__Feature532  label="SMD Capacitor, Configurable, Raspberry Pi Zero 2 W_C072"
  Placement = pos=(-4.6,0.8,8.8) rot=(0,1,0;1.5708rad)
  shape: bbox 0.1 x 0.25 x 0.3 mm, 6 faces (baked)
FEATURE [Part::Feature] Part__Feature533  label="SMD Capacitor, Configurable, Raspberry Pi Zero 2 W_C074"
  Placement = pos=(2.9,0.8,-1.5) rot=(0,1,0;3.14159rad)
  shape: bbox 0.5 x 0.35 x 0.6 mm, 6 faces (baked)
FEATURE [Part::Feature] Part__Feature534  label="SMD Capacitor, Configurable, Raspberry Pi Zero 2 W_C075"
  Placement = pos=(2.9,0.8,-1.5) rot=(0,1,0;3.14159rad)
  shape: bbox 0.5 x 0.35 x 0.2 mm, 6 faces (baked)
FEATURE [Part::Feature] Part__Feature535  label="SMD Capacitor, Configurable, Raspberry Pi Zero 2 W_C076"
  Placement = pos=(2.9,0.8,-1.5) rot=(0,1,0;3.14159rad)
  shape: bbox 0.5 x 0.35 x 0.2 mm, 6 faces (baked)
FEATURE [Part::Feature] Part__Feature536  label="SMD Capacitor, Configurable, Raspberry Pi Zero 2 W_C078"
  Placement = pos=(3.1,0.8,0.3) rot=(0,1,0;1.5708rad)
  shape: bbox 0.6 x 0.35 x 0.5 mm, 6 faces (baked)
FEATURE [Part::Feature] Part__Feature537  label="SMD Capacitor, Configurable, Raspberry Pi Zero 2 W_C079"
  Placement = pos=(3.1,0.8,0.3) rot=(0,1,0;1.5708rad)
  shape: bbox 0.2 x 0.35 x 0.5 mm, 6 faces (baked)
FEATURE [Part::Feature] Part__Feature538  label="SMD Capacitor, Configurable, Raspberry Pi Zero 2 W_C080"
  Placement = pos=(3.1,0.8,0.3) rot=(0,1,0;1.5708rad)
  shape: bbox 0.2 x 0.35 x 0.5 mm, 6 faces (baked)
FEATURE [Part::Feature] Part__Feature539  label="SMD Capacitor, Configurable, Raspberry Pi Zero 2 W_C082"
  Placement = pos=(-2.4,0.8,8.8) rot=(0,1,0;1.5708rad)
  shape: bbox 0.4 x 0.25 x 0.3 mm, 6 faces (baked)
FEATURE [Part::Feature] Part__Feature540  label="SMD Capacitor, Configurable, Raspberry Pi Zero 2 W_C083"
  Placement = pos=(-2.4,0.8,8.8) rot=(0,1,0;1.5708rad)
  shape: bbox 0.1 x 0.25 x 0.3 mm, 6 faces (baked)
FEATURE [Part::Feature] Part__Feature541  label="SMD Capacitor, Configurable, Raspberry Pi Zero 2 W_C084"
  Placement = pos=(-2.4,0.8,8.8) rot=(0,1,0;1.5708rad)
  shape: bbox 0.1 x 0.25 x 0.3 mm, 6 faces (baked)
FEATURE [Part::Feature] Part__Feature542  label="SMD Capacitor, Configurable, Raspberry Pi Zero 2 W_C086"
  Placement = pos=(-9.7,0.8,8.8) rot=(0,1,0;1.5708rad)
  shape: bbox 0.4 x 0.25 x 0.3 mm, 6 faces (baked)
FEATURE [Part::Feature] Part__Feature543  label="SMD Capacitor, Configurable, Raspberry Pi Zero 2 W_C087"
  Placement = pos=(-9.7,0.8,8.8) rot=(0,1,0;1.5708rad)
  shape: bbox 0.1 x 0.25 x 0.3 mm, 6 faces (baked)
FEATURE [Part::Feature] Part__Feature544  label="SMD Capacitor, Configurable, Raspberry Pi Zero 2 W_C088"
  Placement = pos=(-9.7,0.8,8.8) rot=(0,1,0;1.5708rad)
  shape: bbox 0.1 x 0.25 x 0.3 mm, 6 faces (baked)
FEATURE [Part::Feature] Part__Feature545  label="SMD Capacitor, Configurable, Raspberry Pi Zero 2 W_C090"
  Placement = pos=(-8.5,0.8,9.2) rot=(0,1,0;3.14159rad)
  shape: bbox 0.3 x 0.25 x 0.4 mm, 6 faces (baked)
FEATURE [Part::Feature] Part__Feature546  label="SMD Capacitor, Configurable, Raspberry Pi Zero 2 W_C091"
  Placement = pos=(-8.5,0.8,9.2) rot=(0,1,0;3.14159rad)
  shape: bbox 0.3 x 0.25 x 0.1 mm, 6 faces (baked)
FEATURE [Part::Feature] Part__Feature547  label="SMD Capacitor, Configurable, Raspberry Pi Zero 2 W_C092"
  Placement = pos=(-8.5,0.8,9.2) rot=(0,1,0;3.14159rad)
  shape: bbox 0.3 x 0.25 x 0.1 mm, 6 faces (baked)
FEATURE [Part::Feature] Part__Feature548  label="SMD Capacitor, Configurable, Raspberry Pi Zero 2 W_C094"
  Placement = pos=(3.1,0.8,2.2) rot=(0,1,0;3.14159rad)
  shape: bbox 0.3 x 0.25 x 0.4 mm, 6 faces (baked)
FEATURE [Part::Feature] Part__Feature549  label="SMD Capacitor, Configurable, Raspberry Pi Zero 2 W_C095"
  Placement = pos=(3.1,0.8,2.2) rot=(0,1,0;3.14159rad)
  shape: bbox 0.3 x 0.25 x 0.1 mm, 6 faces (baked)
FEATURE [Part::Feature] Part__Feature550  label="SMD Capacitor, Configurable, Raspberry Pi Zero 2 W_C096"
  Placement = pos=(3.1,0.8,2.2) rot=(0,1,0;3.14159rad)
  shape: bbox 0.3 x 0.25 x 0.1 mm, 6 faces (baked)
FEATURE [Part::Feature] Part__Feature551  label="SMD Capacitor, Configurable, Raspberry Pi Zero 2 W_C098"
  Placement = pos=(3,0.8,3.7) rot=(0,1,0;3.14159rad)
  shape: bbox 0.3 x 0.25 x 0.4 mm, 6 faces (baked)
FEATURE [Part::Feature] Part__Feature552  label="SMD Capacitor, Configurable, Raspberry Pi Zero 2 W_C099"
  Placement = pos=(3,0.8,3.7) rot=(0,1,0;3.14159rad)
  shape: bbox 0.3 x 0.25 x 0.1 mm, 6 faces (baked)
FEATURE [Part::Feature] Part__Feature553  label="SMD Capacitor, Configurable, Raspberry Pi Zero 2 W_C100"
  Placement = pos=(3,0.8,3.7) rot=(0,1,0;3.14159rad)
  shape: bbox 0.3 x 0.25 x 0.1 mm, 6 faces (baked)
FEATURE [Part::Feature] Part__Feature554  label="SMD Capacitor, Configurable, Raspberry Pi Zero 2 W_C102"
  Placement = pos=(3,0.8,5.5) rot=(0,1,0;3.14159rad)
  shape: bbox 0.3 x 0.25 x 0.4 mm, 6 faces (baked)
FEATURE [Part::Feature] Part__Feature555  label="SMD Capacitor, Configurable, Raspberry Pi Zero 2 W_C103"
  Placement = pos=(3,0.8,5.5) rot=(0,1,0;3.14159rad)
  shape: bbox 0.3 x 0.25 x 0.1 mm, 6 faces (baked)
FEATURE [Part::Feature] Part__Feature556  label="SMD Capacitor, Configurable, Raspberry Pi Zero 2 W_C104"
  Placement = pos=(3,0.8,5.5) rot=(0,1,0;3.14159rad)
  shape: bbox 0.3 x 0.25 x 0.1 mm, 6 faces (baked)
FEATURE [Part::Feature] Part__Feature557  label="SMD Capacitor, Configurable, Raspberry Pi Zero 2 W_C106"
  Placement = pos=(-27.8,0.8,7.8) rot=(0,1,0;1.5708rad)
  shape: bbox 0.6 x 0.35 x 0.5 mm, 6 faces (baked)
FEATURE [Part::Feature] Part__Feature558  label="SMD Capacitor, Configurable, Raspberry Pi Zero 2 W_C107"
  Placement = pos=(-27.8,0.8,7.8) rot=(0,1,0;1.5708rad)
  shape: bbox 0.2 x 0.35 x 0.5 mm, 6 faces (baked)
FEATURE [Part::Feature] Part__Feature559  label="SMD Capacitor, Configurable, Raspberry Pi Zero 2 W_C108"
  Placement = pos=(-27.8,0.8,7.8) rot=(0,1,0;1.5708rad)
  shape: bbox 0.2 x 0.35 x 0.5 mm, 6 faces (baked)
FEATURE [Part::Feature] Part__Feature560  label="SMD Capacitor, Configurable, Raspberry Pi Zero 2 W_C110"
  Placement = pos=(-12.7,0.8,13.7) rot=(0,1,0;1.5708rad)
  shape: bbox 0.4 x 0.25 x 0.3 mm, 6 faces (baked)
FEATURE [Part::Feature] Part__Feature561  label="SMD Capacitor, Configurable, Raspberry Pi Zero 2 W_C111"
  Placement = pos=(-12.7,0.8,13.7) rot=(0,1,0;1.5708rad)
  shape: bbox 0.1 x 0.25 x 0.3 mm, 6 faces (baked)
FEATURE [Part::Feature] Part__Feature562  label="SMD Capacitor, Configurable, Raspberry Pi Zero 2 W_C112"
  Placement = pos=(-12.7,0.8,13.7) rot=(0,1,0;1.5708rad)
  shape: bbox 0.1 x 0.25 x 0.3 mm, 6 faces (baked)
FEATURE [Part::Feature] Part__Feature563  label="SMD Capacitor, Configurable, Raspberry Pi Zero 2 W_C114"
  Placement = pos=(-17.7,0.8,-3.8) rot=(0,1,0;1.5708rad)
  shape: bbox 0.6 x 0.35 x 0.5 mm, 6 faces (baked)
FEATURE [Part::Feature] Part__Feature564  label="SMD Capacitor, Configurable, Raspberry Pi Zero 2 W_C115"
  Placement = pos=(-17.7,0.8,-3.8) rot=(0,1,0;1.5708rad)
  shape: bbox 0.2 x 0.35 x 0.5 mm, 6 faces (baked)
FEATURE [Part::Feature] Part__Feature565  label="SMD Capacitor, Configurable, Raspberry Pi Zero 2 W_C116"
  Placement = pos=(-17.7,0.8,-3.8) rot=(0,1,0;1.5708rad)
  shape: bbox 0.2 x 0.35 x 0.5 mm, 6 faces (baked)
FEATURE [Part::Feature] Part__Feature566  label="SMD Capacitor, Configurable, Raspberry Pi Zero 2 W_C118"
  Placement = pos=(-17.5,0.8,1) rot=(0,1,0;1.5708rad)
  shape: bbox 0.6 x 0.35 x 0.5 mm, 6 faces (baked)
FEATURE [Part::Feature] Part__Feature567  label="SMD Capacitor, Configurable, Raspberry Pi Zero 2 W_C119"
  Placement = pos=(-17.5,0.8,1) rot=(0,1,0;1.5708rad)
  shape: bbox 0.2 x 0.35 x 0.5 mm, 6 faces (baked)
FEATURE [Part::Feature] Part__Feature129  label="SMD Capacitor, Configurable, Raspberry Pi Zero 2 W_C120"
  Placement = pos=(-17.5,0.8,1) rot=(0,1,0;1.5708rad)
  shape: bbox 0.2 x 0.35 x 0.5 mm, 6 faces (baked)
FEATURE [Part::Feature] Part__Feature130  label="SMD Capacitor, Configurable, Raspberry Pi Zero 2 W_C122"
  Placement = pos=(-7.7,0.8,-7.4) rot=(0,1,0;1.5708rad)
  shape: bbox 0.4 x 0.25 x 0.3 mm, 6 faces (baked)
FEATURE [Part::Feature] Part__Feature131  label="SMD Capacitor, Configurable, Raspberry Pi Zero 2 W_C123"
  Placement = pos=(-7.7,0.8,-7.4) rot=(0,1,0;1.5708rad)
  shape: bbox 0.1 x 0.25 x 0.3 mm, 6 faces (baked)
FEATURE [Part::Feature] Part__Feature132  label="SMD Capacitor, Configurable, Raspberry Pi Zero 2 W_C124"
  Placement = pos=(-7.7,0.8,-7.4) rot=(0,1,0;1.5708rad)
  shape: bbox 0.1 x 0.25 x 0.3 mm, 6 faces (baked)
FEATURE [Part::Feature] Part__Feature133  label="SMD Capacitor, Configurable, Raspberry Pi Zero 2 W_C126"
  Placement = pos=(-5.4,0.8,-7.5) rot=(0,1,0;3.14159rad)
  shape: bbox 0.3 x 0.25 x 0.4 mm, 6 faces (baked)
FEATURE [Part::Feature] Part__Feature134  label="SMD Capacitor, Configurable, Raspberry Pi Zero 2 W_C127"
  Placement = pos=(-5.4,0.8,-7.5) rot=(0,1,0;3.14159rad)
  shape: bbox 0.3 x 0.25 x 0.1 mm, 6 faces (baked)
FEATURE [Part::Feature] Part__Feature135  label="SMD Capacitor, Configurable, Raspberry Pi Zero 2 W_C128"
  Placement = pos=(-5.4,0.8,-7.5) rot=(0,1,0;3.14159rad)
  shape: bbox 0.3 x 0.25 x 0.1 mm, 6 faces (baked)
FEATURE [Part::Feature] Part__Feature136  label="SMD Capacitor, Configurable, Raspberry Pi Zero 2 W_C130"
  Placement = pos=(-0.15,0.8,9) rot=(0,1,0;3.14159rad)
  shape: bbox 0.3 x 0.25 x 0.4 mm, 6 faces (baked)
FEATURE [Part::Feature] Part__Feature137  label="SMD Capacitor, Configurable, Raspberry Pi Zero 2 W_C131"
  Placement = pos=(-0.15,0.8,9) rot=(0,1,0;3.14159rad)
  shape: bbox 0.3 x 0.25 x 0.1 mm, 6 faces (baked)
FEATURE [Part::Feature] Part__Feature138  label="SMD Capacitor, Configurable, Raspberry Pi Zero 2 W_C132"
  Placement = pos=(-0.15,0.8,9) rot=(0,1,0;3.14159rad)
  shape: bbox 0.3 x 0.25 x 0.1 mm, 6 faces (baked)
FEATURE [Part::Feature] Part__Feature139  label="SMD Capacitor, Configurable, Raspberry Pi Zero 2 W_C134"
  Placement = pos=(-1.3,0.8,8.8) rot=(0,1,0;1.5708rad)
  shape: bbox 0.4 x 0.25 x 0.3 mm, 6 faces (baked)
FEATURE [Part::Feature] Part__Feature140  label="SMD Capacitor, Configurable, Raspberry Pi Zero 2 W_C135"
  Placement = pos=(-1.3,0.8,8.8) rot=(0,1,0;1.5708rad)
  shape: bbox 0.1 x 0.25 x 0.3 mm, 6 faces (baked)
FEATURE [Part::Feature] Part__Feature141  label="SMD Capacitor, Configurable, Raspberry Pi Zero 2 W_C136"
  Placement = pos=(-1.3,0.8,8.8) rot=(0,1,0;1.5708rad)
  shape: bbox 0.1 x 0.25 x 0.3 mm, 6 faces (baked)
FEATURE [Part::Feature] Part__Feature142  label="SMD Capacitor, Configurable, Raspberry Pi Zero 2 W_C138"
  Placement = pos=(-15,0.8,6.4) rot=(0,1,0;1.5708rad)
  shape: bbox 0.6 x 0.35 x 0.5 mm, 6 faces (baked)
FEATURE [Part::Feature] Part__Feature143  label="SMD Capacitor, Configurable, Raspberry Pi Zero 2 W_C139"
  Placement = pos=(-15,0.8,6.4) rot=(0,1,0;1.5708rad)
  shape: bbox 0.2 x 0.35 x 0.5 mm, 6 faces (baked)
FEATURE [Part::Feature] Part__Feature144  label="SMD Capacitor, Configurable, Raspberry Pi Zero 2 W_C140"
  Placement = pos=(-15,0.8,6.4) rot=(0,1,0;1.5708rad)
  shape: bbox 0.2 x 0.35 x 0.5 mm, 6 faces (baked)
FEATURE [Part::Feature] Part__Feature145  label="SMD Capacitor, Configurable, Raspberry Pi Zero 2 W_C142"
  Placement = pos=(-14.2,0.8,-2.1) rot=(0,1,0;1.5708rad)
  shape: bbox 0.4 x 0.25 x 0.3 mm, 6 faces (baked)
FEATURE [Part::Feature] Part__Feature146  label="SMD Capacitor, Configurable, Raspberry Pi Zero 2 W_C143"
  Placement = pos=(-14.2,0.8,-2.1) rot=(0,1,0;1.5708rad)
  shape: bbox 0.1 x 0.25 x 0.3 mm, 6 faces (baked)
FEATURE [Part::Feature] Part__Feature147  label="SMD Capacitor, Configurable, Raspberry Pi Zero 2 W_C144"
  Placement = pos=(-14.2,0.8,-2.1) rot=(0,1,0;1.5708rad)
  shape: bbox 0.1 x 0.25 x 0.3 mm, 6 faces (baked)
FEATURE [Part::Feature] Part__Feature148  label="SMD Capacitor, Configurable, Raspberry Pi Zero 2 W_C146"
  Placement = pos=(-15,0.8,-1) rot=(0,0,1;0rad)
  shape: bbox 0.5 x 0.35 x 0.6 mm, 6 faces (baked)
FEATURE [Part::Feature] Part__Feature149  label="SMD Capacitor, Configurable, Raspberry Pi Zero 2 W_C147"
  Placement = pos=(-15,0.8,-1) rot=(0,0,1;0rad)
  shape: bbox 0.5 x 0.35 x 0.2 mm, 6 faces (baked)
FEATURE [Part::Feature] Part__Feature150  label="SMD Capacitor, Configurable, Raspberry Pi Zero 2 W_C148"
  Placement = pos=(-15,0.8,-1) rot=(0,0,1;0rad)
  shape: bbox 0.5 x 0.35 x 0.2 mm, 6 faces (baked)
FEATURE [Part::Feature] Part__Feature151  label="SMD Capacitor, Configurable, Raspberry Pi Zero 2 W_C150"
  Placement = pos=(-14.9,0.8,1.1) rot=(0,0,1;0rad)
  shape: bbox 0.5 x 0.35 x 0.6 mm, 6 faces (baked)
FEATURE [Part::Feature] Part__Feature152  label="SMD Capacitor, Configurable, Raspberry Pi Zero 2 W_C151"
  Placement = pos=(-14.9,0.8,1.1) rot=(0,0,1;0rad)
  shape: bbox 0.5 x 0.35 x 0.2 mm, 6 faces (baked)
FEATURE [Part::Feature] Part__Feature153  label="SMD Capacitor, Configurable, Raspberry Pi Zero 2 W_C152"
  Placement = pos=(-14.9,0.8,1.1) rot=(0,0,1;0rad)
  shape: bbox 0.5 x 0.35 x 0.2 mm, 6 faces (baked)
FEATURE [Part::Feature] Part__Feature154  label="SMD Capacitor, Configurable, Raspberry Pi Zero 2 W_C154"
  Placement = pos=(-14.3,0.8,-7.2) rot=(0,1,0;1.5708rad)
  shape: bbox 0.4 x 0.25 x 0.3 mm, 6 faces (baked)
FEATURE [Part::Feature] Part__Feature155  label="SMD Capacitor, Configurable, Raspberry Pi Zero 2 W_C155"
  Placement = pos=(-14.3,0.8,-7.2) rot=(0,1,0;1.5708rad)
  shape: bbox 0.1 x 0.25 x 0.3 mm, 6 faces (baked)
FEATURE [Part::Feature] Part__Feature156  label="SMD Capacitor, Configurable, Raspberry Pi Zero 2 W_C156"
  Placement = pos=(-14.3,0.8,-7.2) rot=(0,1,0;1.5708rad)
  shape: bbox 0.1 x 0.25 x 0.3 mm, 6 faces (baked)
FEATURE [Part::Feature] Part__Feature157  label="SMD Capacitor, Configurable, Raspberry Pi Zero 2 W_C158"
  Placement = pos=(-14.1,0.8,-6) rot=(0,1,0;1.5708rad)
  shape: bbox 0.4 x 0.25 x 0.3 mm, 6 faces (baked)
FEATURE [Part::Feature] Part__Feature158  label="SMD Capacitor, Configurable, Raspberry Pi Zero 2 W_C159"
  Placement = pos=(-14.1,0.8,-6) rot=(0,1,0;1.5708rad)
  shape: bbox 0.1 x 0.25 x 0.3 mm, 6 faces (baked)
FEATURE [Part::Feature] Part__Feature159  label="SMD Capacitor, Configurable, Raspberry Pi Zero 2 W_C160"
  Placement = pos=(-14.1,0.8,-6) rot=(0,1,0;1.5708rad)
  shape: bbox 0.1 x 0.25 x 0.3 mm, 6 faces (baked)
FEATURE [Part::Feature] Part__Feature160  label="SMD Capacitor, Configurable, Raspberry Pi Zero 2 W_C162"
  Placement = pos=(-13.3,0.8,1.7) rot=(0,0,1;0rad)
  shape: bbox 0.3 x 0.25 x 0.4 mm, 6 faces (baked)
FEATURE [Part::Feature] Part__Feature161  label="SMD Capacitor, Configurable, Raspberry Pi Zero 2 W_C163"
  Placement = pos=(-13.3,0.8,1.7) rot=(0,0,1;0rad)
  shape: bbox 0.3 x 0.25 x 0.1 mm, 6 faces (baked)
FEATURE [Part::Feature] Part__Feature162  label="SMD Capacitor, Configurable, Raspberry Pi Zero 2 W_C164"
  Placement = pos=(-13.3,0.8,1.7) rot=(0,0,1;0rad)
  shape: bbox 0.3 x 0.25 x 0.1 mm, 6 faces (baked)
FEATURE [Part::Feature] Part__Feature163  label="SMD Capacitor, Configurable, Raspberry Pi Zero 2 W_C166"
  Placement = pos=(-13.3,0.8,-0.9) rot=(0,0,1;0rad)
  shape: bbox 0.3 x 0.25 x 0.4 mm, 6 faces (baked)
FEATURE [Part::Feature] Part__Feature164  label="SMD Capacitor, Configurable, Raspberry Pi Zero 2 W_C167"
  Placement = pos=(-13.3,0.8,-0.9) rot=(0,0,1;0rad)
  shape: bbox 0.3 x 0.25 x 0.1 mm, 6 faces (baked)
FEATURE [Part::Feature] Part__Feature165  label="SMD Capacitor, Configurable, Raspberry Pi Zero 2 W_C168"
  Placement = pos=(-13.3,0.8,-0.9) rot=(0,0,1;0rad)
  shape: bbox 0.3 x 0.25 x 0.1 mm, 6 faces (baked)
FEATURE [Part::Feature] Part__Feature166  label="SMD Capacitor, Configurable, Raspberry Pi Zero 2 W_C170"
  Placement = pos=(-14.2,0.8,-2.7) rot=(0,1,0;1.5708rad)
  shape: bbox 0.4 x 0.25 x 0.3 mm, 6 faces (baked)
FEATURE [Part::Feature] Part__Feature167  label="SMD Capacitor, Configurable, Raspberry Pi Zero 2 W_C171"
  Placement = pos=(-14.2,0.8,-2.7) rot=(0,1,0;1.5708rad)
  shape: bbox 0.1 x 0.25 x 0.3 mm, 6 faces (baked)
FEATURE [Part::Feature] Part__Feature168  label="SMD Capacitor, Configurable, Raspberry Pi Zero 2 W_C172"
  Placement = pos=(-14.2,0.8,-2.7) rot=(0,1,0;1.5708rad)
  shape: bbox 0.1 x 0.25 x 0.3 mm, 6 faces (baked)
FEATURE [Part::Feature] Part__Feature169  label="SMD Capacitor, Configurable, Raspberry Pi Zero 2 W_C174"
  Placement = pos=(-14.2,0.8,-3.3) rot=(0,1,0;1.5708rad)
  shape: bbox 0.4 x 0.25 x 0.3 mm, 6 faces (baked)
FEATURE [Part::Feature] Part__Feature170  label="SMD Capacitor, Configurable, Raspberry Pi Zero 2 W_C175"
  Placement = pos=(-14.2,0.8,-3.3) rot=(0,1,0;1.5708rad)
  shape: bbox 0.1 x 0.25 x 0.3 mm, 6 faces (baked)
FEATURE [Part::Feature] Part__Feature171  label="SMD Capacitor, Configurable, Raspberry Pi Zero 2 W_C176"
  Placement = pos=(-14.2,0.8,-3.3) rot=(0,1,0;1.5708rad)
  shape: bbox 0.1 x 0.25 x 0.3 mm, 6 faces (baked)
FEATURE [Part::Feature] Part__Feature172  label="SMD Capacitor, Configurable, Raspberry Pi Zero 2 W_C178"
  Placement = pos=(-14.2,0.8,-3.9) rot=(0,1,0;1.5708rad)
  shape: bbox 0.4 x 0.25 x 0.3 mm, 6 faces (baked)
FEATURE [Part::Feature] Part__Feature173  label="SMD Capacitor, Configurable, Raspberry Pi Zero 2 W_C179"
  Placement = pos=(-14.2,0.8,-3.9) rot=(0,1,0;1.5708rad)
  shape: bbox 0.1 x 0.25 x 0.3 mm, 6 faces (baked)
FEATURE [Part::Feature] Part__Feature174  label="SMD Capacitor, Configurable, Raspberry Pi Zero 2 W_C180"
  Placement = pos=(-14.2,0.8,-3.9) rot=(0,1,0;1.5708rad)
  shape: bbox 0.1 x 0.25 x 0.3 mm, 6 faces (baked)
FEATURE [Part::Feature] Part__Feature175  label="SMD Capacitor, Configurable, Raspberry Pi Zero 2 W_C182"
  Placement = pos=(-14.1,0.8,3.7) rot=(0,1,0;1.5708rad)
  shape: bbox 0.4 x 0.25 x 0.3 mm, 6 faces (baked)
FEATURE [Part::Feature] Part__Feature176  label="SMD Capacitor, Configurable, Raspberry Pi Zero 2 W_C183"
  Placement = pos=(-14.1,0.8,3.7) rot=(0,1,0;1.5708rad)
  shape: bbox 0.1 x 0.25 x 0.3 mm, 6 faces (baked)
FEATURE [Part::Feature] Part__Feature177  label="SMD Capacitor, Configurable, Raspberry Pi Zero 2 W_C184"
  Placement = pos=(-14.1,0.8,3.7) rot=(0,1,0;1.5708rad)
  shape: bbox 0.1 x 0.25 x 0.3 mm, 6 faces (baked)
FEATURE [Part::Feature] Part__Feature178  label="SMD Capacitor, Configurable, Raspberry Pi Zero 2 W_C186"
  Placement = pos=(-15,0.8,3) rot=(0,0,1;0rad)
  shape: bbox 0.3 x 0.25 x 0.4 mm, 6 faces (baked)
FEATURE [Part::Feature] Part__Feature179  label="SMD Capacitor, Configurable, Raspberry Pi Zero 2 W_C187"
  Placement = pos=(-15,0.8,3) rot=(0,0,1;0rad)
  shape: bbox 0.3 x 0.25 x 0.1 mm, 6 faces (baked)
FEATURE [Part::Feature] Part__Feature180  label="SMD Capacitor, Configurable, Raspberry Pi Zero 2 W_C188"
  Placement = pos=(-15,0.8,3) rot=(0,0,1;0rad)
  shape: bbox 0.3 x 0.25 x 0.1 mm, 6 faces (baked)
FEATURE [Part::Feature] Part__Feature181  label="SMD Capacitor, Configurable, Raspberry Pi Zero 2 W_C190"
  Placement = pos=(-15.8,0.8,3) rot=(0,0,1;0rad)
  shape: bbox 0.3 x 0.25 x 0.4 mm, 6 faces (baked)
FEATURE [Part::Feature] Part__Feature182  label="SMD Capacitor, Configurable, Raspberry Pi Zero 2 W_C191"
  Placement = pos=(-15.8,0.8,3) rot=(0,0,1;0rad)
  shape: bbox 0.3 x 0.25 x 0.1 mm, 6 faces (baked)
FEATURE [Part::Feature] Part__Feature183  label="SMD Capacitor, Configurable, Raspberry Pi Zero 2 W_C192"
  Placement = pos=(-15.8,0.8,3) rot=(0,0,1;0rad)
  shape: bbox 0.3 x 0.25 x 0.1 mm, 6 faces (baked)
FEATURE [Part::Feature] Part__Feature184  label="SMD Capacitor, Configurable, Raspberry Pi Zero 2 W_C194"
  Placement = pos=(25.8,0.8,-5.6) rot=(0,1,0;1.5708rad)
  shape: bbox 0.4 x 0.25 x 0.3 mm, 6 faces (baked)
FEATURE [Part::Feature] Part__Feature185  label="SMD Capacitor, Configurable, Raspberry Pi Zero 2 W_C195"
  Placement = pos=(25.8,0.8,-5.6) rot=(0,1,0;1.5708rad)
  shape: bbox 0.1 x 0.25 x 0.3 mm, 6 faces (baked)
FEATURE [Part::Feature] Part__Feature186  label="SMD Capacitor, Configurable, Raspberry Pi Zero 2 W_C196"
  Placement = pos=(25.8,0.8,-5.6) rot=(0,1,0;1.5708rad)
  shape: bbox 0.1 x 0.25 x 0.3 mm, 6 faces (baked)
FEATURE [Part::Feature] Part__Feature187  label="SMD Capacitor, Configurable, Raspberry Pi Zero 2 W_C198"
  Placement = pos=(25.1,0.8,-6.5) rot=(0,0,1;0rad)
  shape: bbox 0.3 x 0.25 x 0.4 mm, 6 faces (baked)
FEATURE [Part::Feature] Part__Feature188  label="SMD Capacitor, Configurable, Raspberry Pi Zero 2 W_C199"
  Placement = pos=(25.1,0.8,-6.5) rot=(0,0,1;0rad)
  shape: bbox 0.3 x 0.25 x 0.1 mm, 6 faces (baked)
FEATURE [Part::Feature] Part__Feature189  label="SMD Capacitor, Configurable, Raspberry Pi Zero 2 W_C200"
  Placement = pos=(25.1,0.8,-6.5) rot=(0,0,1;0rad)
  shape: bbox 0.3 x 0.25 x 0.1 mm, 6 faces (baked)
FEATURE [Part::Feature] Part__Feature190  label="SMD Capacitor, Configurable, Raspberry Pi Zero 2 W_C202"
  Placement = pos=(25.3,0.8,4.9) rot=(0,1,0;1.5708rad)
  shape: bbox 0.4 x 0.25 x 0.3 mm, 6 faces (baked)
FEATURE [Part::Feature] Part__Feature191  label="SMD Capacitor, Configurable, Raspberry Pi Zero 2 W_C203"
  Placement = pos=(25.3,0.8,4.9) rot=(0,1,0;1.5708rad)
  shape: bbox 0.1 x 0.25 x 0.3 mm, 6 faces (baked)
FEATURE [Part::Feature] Part__Feature192  label="SMD Capacitor, Configurable, Raspberry Pi Zero 2 W_C204"
  Placement = pos=(25.3,0.8,4.9) rot=(0,1,0;1.5708rad)
  shape: bbox 0.1 x 0.25 x 0.3 mm, 6 faces (baked)
FEATURE [Part::Feature] Part__Feature193  label="SMD Capacitor, Configurable, Raspberry Pi Zero 2 W_C206"
  Placement = pos=(18.7,0.8,-3) rot=(0,0,1;0rad)
  shape: bbox 0.3 x 0.25 x 0.4 mm, 6 faces (baked)
FEATURE [Part::Feature] Part__Feature194  label="SMD Capacitor, Configurable, Raspberry Pi Zero 2 W_C207"
  Placement = pos=(18.7,0.8,-3) rot=(0,0,1;0rad)
  shape: bbox 0.3 x 0.25 x 0.1 mm, 6 faces (baked)
FEATURE [Part::Feature] Part__Feature195  label="SMD Capacitor, Configurable, Raspberry Pi Zero 2 W_C208"
  Placement = pos=(18.7,0.8,-3) rot=(0,0,1;0rad)
  shape: bbox 0.3 x 0.25 x 0.1 mm, 6 faces (baked)
FEATURE [Part::Feature] Part__Feature196  label="SMD Capacitor, Configurable, Raspberry Pi Zero 2 W_C210"
  Placement = pos=(6.92687,0.8,8.9) rot=(0,1,0;1.5708rad)
  shape: bbox 0.4 x 0.25 x 0.3 mm, 6 faces (baked)
FEATURE [Part::Feature] Part__Feature197  label="SMD Capacitor, Configurable, Raspberry Pi Zero 2 W_C211"
  Placement = pos=(6.92687,0.8,8.9) rot=(0,1,0;1.5708rad)
  shape: bbox 0.1 x 0.25 x 0.3 mm, 6 faces (baked)
FEATURE [Part::Feature] Part__Feature198  label="SMD Capacitor, Configurable, Raspberry Pi Zero 2 W_C212"
  Placement = pos=(6.92687,0.8,8.9) rot=(0,1,0;1.5708rad)
  shape: bbox 0.1 x 0.25 x 0.3 mm, 6 faces (baked)
FEATURE [Part::Feature] Part__Feature199  label="SMD Capacitor, Configurable, Raspberry Pi Zero 2 W_C214"
  Placement = pos=(3.5,0.8,-1.5) rot=(0,1,0;3.14159rad)
  shape: bbox 0.3 x 0.25 x 0.4 mm, 6 faces (baked)
FEATURE [Part::Feature] Part__Feature200  label="SMD Capacitor, Configurable, Raspberry Pi Zero 2 W_C215"
  Placement = pos=(3.5,0.8,-1.5) rot=(0,1,0;3.14159rad)
  shape: bbox 0.3 x 0.25 x 0.1 mm, 6 faces (baked)
FEATURE [Part::Feature] Part__Feature201  label="SMD Capacitor, Configurable, Raspberry Pi Zero 2 W_C216"
  Placement = pos=(3.5,0.8,-1.5) rot=(0,1,0;3.14159rad)
  shape: bbox 0.3 x 0.25 x 0.1 mm, 6 faces (baked)
FEATURE [Part::Feature] Part__Feature202  label="SMD Resistor, Configurable, Raspberry Pi Zero 2 W_R1"
  Placement = pos=(-18.4,0.8,-8.2) rot=(0,0,1;0rad)
  shape: bbox 0.5 x 0.35 x 0.6 mm, 6 faces (baked)
FEATURE [Part::Feature] Part__Feature203  label="SMD Resistor, Configurable, Raspberry Pi Zero 2 W_R002"
  Placement = pos=(-18.4,0.8,-8.2) rot=(0,0,1;0rad)
  shape: bbox 0.5 x 0.35 x 0.2 mm, 6 faces (baked)
FEATURE [Part::Feature] Part__Feature204  label="SMD Resistor, Configurable, Raspberry Pi Zero 2 W_R003"
  Placement = pos=(-18.4,0.8,-8.2) rot=(0,0,1;0rad)
  shape: bbox 0.5 x 0.35 x 0.2 mm, 6 faces (baked)
FEATURE [Part::Feature] Part__Feature205  label="SMD Resistor, Configurable, Raspberry Pi Zero 2 W_R005"
  Placement = pos=(-17.1,0.8,-8.2) rot=(0,0,1;0rad)
  shape: bbox 0.5 x 0.35 x 0.6 mm, 6 faces (baked)
FEATURE [Part::Feature] Part__Feature206  label="SMD Resistor, Configurable, Raspberry Pi Zero 2 W_R006"
  Placement = pos=(-17.1,0.8,-8.2) rot=(0,0,1;0rad)
  shape: bbox 0.5 x 0.35 x 0.2 mm, 6 faces (baked)
FEATURE [Part::Feature] Part__Feature207  label="SMD Resistor, Configurable, Raspberry Pi Zero 2 W_R007"
  Placement = pos=(-17.1,0.8,-8.2) rot=(0,0,1;0rad)
  shape: bbox 0.5 x 0.35 x 0.2 mm, 6 faces (baked)
FEATURE [Part::Feature] Part__Feature208  label="SMD Resistor, Configurable, Raspberry Pi Zero 2 W_R009"
  Placement = pos=(23.9,0.8,-8) rot=(0,0,1;0rad)
  shape: bbox 0.5 x 0.35 x 0.6 mm, 6 faces (baked)
FEATURE [Part::Feature] Part__Feature209  label="SMD Resistor, Configurable, Raspberry Pi Zero 2 W_R010"
  Placement = pos=(23.9,0.8,-8) rot=(0,0,1;0rad)
  shape: bbox 0.5 x 0.35 x 0.2 mm, 6 faces (baked)
FEATURE [Part::Feature] Part__Feature210  label="SMD Resistor, Configurable, Raspberry Pi Zero 2 W_R011"
  Placement = pos=(23.9,0.8,-8) rot=(0,0,1;0rad)
  shape: bbox 0.5 x 0.35 x 0.2 mm, 6 faces (baked)
FEATURE [Part::Feature] Part__Feature211  label="SMD Resistor, Configurable, Raspberry Pi Zero 2 W_R12"
  Placement = pos=(24.9,0.8,-8) rot=(0,0,1;0rad)
  shape: bbox 0.3 x 0.23 x 0.4 mm, 6 faces (baked)
FEATURE [Part::Feature] Part__Feature212  label="SMD Resistor, Configurable, Raspberry Pi Zero 2 W_R013"
  Placement = pos=(24.9,0.8,-8) rot=(0,0,1;0rad)
  shape: bbox 0.3 x 0.23 x 0.1 mm, 6 faces (baked)
FEATURE [Part::Feature] Part__Feature213  label="SMD Resistor, Configurable, Raspberry Pi Zero 2 W_R014"
  Placement = pos=(24.9,0.8,-8) rot=(0,0,1;0rad)
  shape: bbox 0.3 x 0.23 x 0.1 mm, 6 faces (baked)
FEATURE [Part::Feature] Part__Feature214  label="SMD Resistor, Configurable, Raspberry Pi Zero 2 W_R016"
  Placement = pos=(-10.8,0.8,-7.3) rot=(0,-1,0;1.5708rad)
  shape: bbox 0.6 x 0.35 x 0.5 mm, 6 faces (baked)
FEATURE [Part::Feature] Part__Feature215  label="SMD Resistor, Configurable, Raspberry Pi Zero 2 W_R017"
  Placement = pos=(-10.8,0.8,-7.3) rot=(0,-1,0;1.5708rad)
  shape: bbox 0.2 x 0.35 x 0.5 mm, 6 faces (baked)
FEATURE [Part::Feature] Part__Feature216  label="SMD Resistor, Configurable, Raspberry Pi Zero 2 W_R018"
  Placement = pos=(-10.8,0.8,-7.3) rot=(0,-1,0;1.5708rad)
  shape: bbox 0.2 x 0.35 x 0.5 mm, 6 faces (baked)
FEATURE [Part::Feature] Part__Feature217  label="SMD Resistor, Configurable, Raspberry Pi Zero 2 W_R020"
  Placement = pos=(-14.3,0.8,-4.7) rot=(0,-1,0;1.5708rad)
  shape: bbox 0.6 x 0.35 x 0.5 mm, 6 faces (baked)
FEATURE [Part::Feature] Part__Feature218  label="SMD Resistor, Configurable, Raspberry Pi Zero 2 W_R021"
  Placement = pos=(-14.3,0.8,-4.7) rot=(0,-1,0;1.5708rad)
  shape: bbox 0.2 x 0.35 x 0.5 mm, 6 faces (baked)
FEATURE [Part::Feature] Part__Feature219  label="SMD Resistor, Configurable, Raspberry Pi Zero 2 W_R022"
  Placement = pos=(-14.3,0.8,-4.7) rot=(0,-1,0;1.5708rad)
  shape: bbox 0.2 x 0.35 x 0.5 mm, 6 faces (baked)
FEATURE [Part::Feature] Part__Feature220  label="SMD Resistor, Configurable, Raspberry Pi Zero 2 W_R024"
  Placement = pos=(-13.3,0.8,-7.3) rot=(0,-1,0;1.5708rad)
  shape: bbox 0.6 x 0.35 x 0.5 mm, 6 faces (baked)
FEATURE [Part::Feature] Part__Feature221  label="SMD Resistor, Configurable, Raspberry Pi Zero 2 W_R025"
  Placement = pos=(-13.3,0.8,-7.3) rot=(0,-1,0;1.5708rad)
  shape: bbox 0.2 x 0.35 x 0.5 mm, 6 faces (baked)
FEATURE [Part::Feature] Part__Feature222  label="SMD Resistor, Configurable, Raspberry Pi Zero 2 W_R026"
  Placement = pos=(-13.3,0.8,-7.3) rot=(0,-1,0;1.5708rad)
  shape: bbox 0.2 x 0.35 x 0.5 mm, 6 faces (baked)
FEATURE [Part::Feature] Part__Feature223  label="SMD Resistor, Configurable, Raspberry Pi Zero 2 W_R028"
  Placement = pos=(-17.7,0.8,-5.8) rot=(0,-1,0;1.5708rad)
  shape: bbox 0.6 x 0.35 x 0.5 mm, 6 faces (baked)
FEATURE [Part::Feature] Part__Feature224  label="SMD Resistor, Configurable, Raspberry Pi Zero 2 W_R029"
  Placement = pos=(-17.7,0.8,-5.8) rot=(0,-1,0;1.5708rad)
  shape: bbox 0.2 x 0.35 x 0.5 mm, 6 faces (baked)
FEATURE [Part::Feature] Part__Feature225  label="SMD Resistor, Configurable, Raspberry Pi Zero 2 W_R030"
  Placement = pos=(-17.7,0.8,-5.8) rot=(0,-1,0;1.5708rad)
  shape: bbox 0.2 x 0.35 x 0.5 mm, 6 faces (baked)
FEATURE [Part::Feature] Part__Feature226  label="SMD Resistor, Configurable, Raspberry Pi Zero 2 W_R032"
  Placement = pos=(-17.7,0.8,-4.8) rot=(0,-1,0;1.5708rad)
  shape: bbox 0.6 x 0.35 x 0.5 mm, 6 faces (baked)
FEATURE [Part::Feature] Part__Feature227  label="SMD Resistor, Configurable, Raspberry Pi Zero 2 W_R033"
  Placement = pos=(-17.7,0.8,-4.8) rot=(0,-1,0;1.5708rad)
  shape: bbox 0.2 x 0.35 x 0.5 mm, 6 faces (baked)
FEATURE [Part::Feature] Part__Feature228  label="SMD Resistor, Configurable, Raspberry Pi Zero 2 W_R034"
  Placement = pos=(-17.7,0.8,-4.8) rot=(0,-1,0;1.5708rad)
  shape: bbox 0.2 x 0.35 x 0.5 mm, 6 faces (baked)
FEATURE [Part::Feature] Part__Feature229  label="SMD Resistor, Configurable, Raspberry Pi Zero 2 W_R036"
  Placement = pos=(-27.7,0.8,4.8) rot=(0,-1,0;1.5708rad)
  shape: bbox 0.6 x 0.35 x 0.5 mm, 6 faces (baked)
FEATURE [Part::Feature] Part__Feature230  label="SMD Resistor, Configurable, Raspberry Pi Zero 2 W_R037"
  Placement = pos=(-27.7,0.8,4.8) rot=(0,-1,0;1.5708rad)
  shape: bbox 0.2 x 0.35 x 0.5 mm, 6 faces (baked)
FEATURE [Part::Feature] Part__Feature231  label="SMD Resistor, Configurable, Raspberry Pi Zero 2 W_R038"
  Placement = pos=(-27.7,0.8,4.8) rot=(0,-1,0;1.5708rad)
  shape: bbox 0.2 x 0.35 x 0.5 mm, 6 faces (baked)
FEATURE [Part::Feature] Part__Feature232  label="SMD Resistor, Configurable, Raspberry Pi Zero 2 W_R040"
  Placement = pos=(-15,0.8,5.4) rot=(0,-1,0;1.5708rad)
  shape: bbox 0.6 x 0.35 x 0.5 mm, 6 faces (baked)
FEATURE [Part::Feature] Part__Feature233  label="SMD Resistor, Configurable, Raspberry Pi Zero 2 W_R041"
  Placement = pos=(-15,0.8,5.4) rot=(0,-1,0;1.5708rad)
  shape: bbox 0.2 x 0.35 x 0.5 mm, 6 faces (baked)
FEATURE [Part::Feature] Part__Feature234  label="SMD Resistor, Configurable, Raspberry Pi Zero 2 W_R042"
  Placement = pos=(-15,0.8,5.4) rot=(0,-1,0;1.5708rad)
  shape: bbox 0.2 x 0.35 x 0.5 mm, 6 faces (baked)
FEATURE [Part::Feature] Part__Feature235  label="SMD Resistor, Configurable, Raspberry Pi Zero 2 W_R044"
  Placement = pos=(-6.7,0.8,9.69578) rot=(0,-1,0;1.5708rad)
  shape: bbox 0.6 x 0.35 x 0.5 mm, 6 faces (baked)
FEATURE [Part::Feature] Part__Feature236  label="SMD Resistor, Configurable, Raspberry Pi Zero 2 W_R045"
  Placement = pos=(-6.7,0.8,9.69578) rot=(0,-1,0;1.5708rad)
  shape: bbox 0.2 x 0.35 x 0.5 mm, 6 faces (baked)
FEATURE [Part::Feature] Part__Feature237  label="SMD Resistor, Configurable, Raspberry Pi Zero 2 W_R046"
  Placement = pos=(-6.7,0.8,9.69578) rot=(0,-1,0;1.5708rad)
  shape: bbox 0.2 x 0.35 x 0.5 mm, 6 faces (baked)
FEATURE [Part::Feature] Part__Feature238  label="SMD Resistor, Configurable, Raspberry Pi Zero 2 W_R048"
  Placement = pos=(-11.7,0.8,8.9) rot=(0,-1,0;1.5708rad)
  shape: bbox 0.6 x 0.35 x 0.5 mm, 6 faces (baked)
FEATURE [Part::Feature] Part__Feature239  label="SMD Resistor, Configurable, Raspberry Pi Zero 2 W_R049"
  Placement = pos=(-11.7,0.8,8.9) rot=(0,-1,0;1.5708rad)
  shape: bbox 0.2 x 0.35 x 0.5 mm, 6 faces (baked)
FEATURE [Part::Feature] Part__Feature240  label="SMD Resistor, Configurable, Raspberry Pi Zero 2 W_R050"
  Placement = pos=(-11.7,0.8,8.9) rot=(0,-1,0;1.5708rad)
  shape: bbox 0.2 x 0.35 x 0.5 mm, 6 faces (baked)
FEATURE [Part::Feature] Part__Feature241  label="SMD Resistor, Configurable, Raspberry Pi Zero 2 W_R052"
  Placement = pos=(24.8,0.8,5.7) rot=(0,-1,0;1.5708rad)
  shape: bbox 0.6 x 0.35 x 0.5 mm, 6 faces (baked)
FEATURE [Part::Feature] Part__Feature242  label="SMD Resistor, Configurable, Raspberry Pi Zero 2 W_R053"
  Placement = pos=(24.8,0.8,5.7) rot=(0,-1,0;1.5708rad)
  shape: bbox 0.2 x 0.35 x 0.5 mm, 6 faces (baked)
FEATURE [Part::Feature] Part__Feature243  label="SMD Resistor, Configurable, Raspberry Pi Zero 2 W_R054"
  Placement = pos=(24.8,0.8,5.7) rot=(0,-1,0;1.5708rad)
  shape: bbox 0.2 x 0.35 x 0.5 mm, 6 faces (baked)
FEATURE [Part::Feature] Part__Feature244  label="SMD Resistor, Configurable, Raspberry Pi Zero 2 W_R056"
  Placement = pos=(27.2,0.8,4.3) rot=(0,-1,0;1.5708rad)
  shape: bbox 0.6 x 0.35 x 0.5 mm, 6 faces (baked)
FEATURE [Part::Feature] Part__Feature245  label="SMD Resistor, Configurable, Raspberry Pi Zero 2 W_R057"
  Placement = pos=(27.2,0.8,4.3) rot=(0,-1,0;1.5708rad)
  shape: bbox 0.2 x 0.35 x 0.5 mm, 6 faces (baked)
FEATURE [Part::Feature] Part__Feature246  label="SMD Resistor, Configurable, Raspberry Pi Zero 2 W_R058"
  Placement = pos=(27.2,0.8,4.3) rot=(0,-1,0;1.5708rad)
  shape: bbox 0.2 x 0.35 x 0.5 mm, 6 faces (baked)
FEATURE [Part::Feature] Part__Feature247  label="SMD Resistor, Configurable, Raspberry Pi Zero 2 W_R060"
  Placement = pos=(27.2,0.8,5.3) rot=(0,-1,0;1.5708rad)
  shape: bbox 0.6 x 0.35 x 0.5 mm, 6 faces (baked)
FEATURE [Part::Feature] Part__Feature248  label="SMD Resistor, Configurable, Raspberry Pi Zero 2 W_R061"
  Placement = pos=(27.2,0.8,5.3) rot=(0,-1,0;1.5708rad)
  shape: bbox 0.2 x 0.35 x 0.5 mm, 6 faces (baked)
FEATURE [Part::Feature] Part__Feature249  label="SMD Resistor, Configurable, Raspberry Pi Zero 2 W_R062"
  Placement = pos=(27.2,0.8,5.3) rot=(0,-1,0;1.5708rad)
  shape: bbox 0.2 x 0.35 x 0.5 mm, 6 faces (baked)
FEATURE [Part::Feature] Part__Feature250  label="SMD Resistor, Configurable, Raspberry Pi Zero 2 W_R064"
  Placement = pos=(27.2,0.8,6.4) rot=(0,-1,0;1.5708rad)
  shape: bbox 0.6 x 0.35 x 0.5 mm, 6 faces (baked)
FEATURE [Part::Feature] Part__Feature251  label="SMD Resistor, Configurable, Raspberry Pi Zero 2 W_R065"
  Placement = pos=(27.2,0.8,6.4) rot=(0,-1,0;1.5708rad)
  shape: bbox 0.2 x 0.35 x 0.5 mm, 6 faces (baked)
FEATURE [Part::Feature] Part__Feature252  label="SMD Resistor, Configurable, Raspberry Pi Zero 2 W_R066"
  Placement = pos=(27.2,0.8,6.4) rot=(0,-1,0;1.5708rad)
  shape: bbox 0.2 x 0.35 x 0.5 mm, 6 faces (baked)
FEATURE [Part::Feature] Part__Feature253  label="SMD Resistor, Configurable, Raspberry Pi Zero 2 W_R068"
  Placement = pos=(26.5,0.8,-6.5) rot=(0,-1,0;1.5708rad)
  shape: bbox 0.6 x 0.35 x 0.5 mm, 6 faces (baked)
FEATURE [Part::Feature] Part__Feature254  label="SMD Resistor, Configurable, Raspberry Pi Zero 2 W_R069"
  Placement = pos=(26.5,0.8,-6.5) rot=(0,-1,0;1.5708rad)
  shape: bbox 0.2 x 0.35 x 0.5 mm, 6 faces (baked)
FEATURE [Part::Feature] Part__Feature255  label="SMD Resistor, Configurable, Raspberry Pi Zero 2 W_R070"
  Placement = pos=(26.5,0.8,-6.5) rot=(0,-1,0;1.5708rad)
  shape: bbox 0.2 x 0.35 x 0.5 mm, 6 faces (baked)
FEATURE [Part::Feature] Part__Feature256  label="SMD Resistor, Configurable, Raspberry Pi Zero 2 W_R072"
  Placement = pos=(26.5,0.8,-7.4) rot=(0,-1,0;1.5708rad)
  shape: bbox 0.6 x 0.35 x 0.5 mm, 6 faces (baked)
FEATURE [Part::Feature] Part__Feature257  label="SMD Resistor, Configurable, Raspberry Pi Zero 2 W_R073"
  Placement = pos=(26.5,0.8,-7.4) rot=(0,-1,0;1.5708rad)
  shape: bbox 0.2 x 0.35 x 0.5 mm, 6 faces (baked)
FEATURE [Part::Feature] Part__Feature258  label="SMD Resistor, Configurable, Raspberry Pi Zero 2 W_R074"
  Placement = pos=(26.5,0.8,-7.4) rot=(0,-1,0;1.5708rad)
  shape: bbox 0.2 x 0.35 x 0.5 mm, 6 faces (baked)
FEATURE [Part::Feature] Part__Feature259  label="SMD Resistor, Configurable, Raspberry Pi Zero 2 W_R076"
  Placement = pos=(26.5,0.8,-8.6) rot=(0,-1,0;1.5708rad)
  shape: bbox 0.6 x 0.35 x 0.5 mm, 6 faces (baked)
FEATURE [Part::Feature] Part__Feature260  label="SMD Resistor, Configurable, Raspberry Pi Zero 2 W_R077"
  Placement = pos=(26.5,0.8,-8.6) rot=(0,-1,0;1.5708rad)
  shape: bbox 0.2 x 0.35 x 0.5 mm, 6 faces (baked)
FEATURE [Part::Feature] Part__Feature261  label="SMD Resistor, Configurable, Raspberry Pi Zero 2 W_R078"
  Placement = pos=(26.5,0.8,-8.6) rot=(0,-1,0;1.5708rad)
  shape: bbox 0.2 x 0.35 x 0.5 mm, 6 faces (baked)
FEATURE [Part::Feature] Part__Feature262  label="SMD Resistor, Configurable, Raspberry Pi Zero 2 W_R080"
  Placement = pos=(3.5,0.8,-6.6) rot=(0,-1,0;0.785398rad)
  shape: bbox 0.7778 x 0.35 x 0.7778 mm, 6 faces (baked)
FEATURE [Part::Feature] Part__Feature263  label="SMD Resistor, Configurable, Raspberry Pi Zero 2 W_R081"
  Placement = pos=(3.5,0.8,-6.6) rot=(0,-1,0;0.785398rad)
  shape: bbox 0.495 x 0.35 x 0.495 mm, 6 faces (baked)
FEATURE [Part::Feature] Part__Feature264  label="SMD Resistor, Configurable, Raspberry Pi Zero 2 W_R082"
  Placement = pos=(3.5,0.8,-6.6) rot=(0,-1,0;0.785398rad)
  shape: bbox 0.495 x 0.35 x 0.495 mm, 6 faces (baked)
FEATURE [Part::Feature] Part__Feature265  label="SMD Capacitor, Configurable, Raspberry Pi Zero 2 W_C218"
  Placement = pos=(14.6,0.8,-8.3) rot=(0,1,0;1.5708rad)
  shape: bbox 0.4 x 0.25 x 0.3 mm, 6 faces (baked)
FEATURE [Part::Feature] Part__Feature266  label="SMD Capacitor, Configurable, Raspberry Pi Zero 2 W_C219"
  Placement = pos=(14.6,0.8,-8.3) rot=(0,1,0;1.5708rad)
  shape: bbox 0.1 x 0.25 x 0.3 mm, 6 faces (baked)
FEATURE [Part::Feature] Part__Feature267  label="SMD Capacitor, Configurable, Raspberry Pi Zero 2 W_C220"
  Placement = pos=(14.6,0.8,-8.3) rot=(0,1,0;1.5708rad)
  shape: bbox 0.1 x 0.25 x 0.3 mm, 6 faces (baked)
FEATURE [Part::Feature] Part__Feature268  label="40 pin header male Raspberry PI v1"
  Placement = pos=(1.27,1,-11.49) rot=(0,1,0;1.5708rad)
  shape: bbox 50.8 x 11.5 x 5 mm, 684 faces (baked)
FEATURE [App::Part] SD_Card_Slot__Raspberry_Pi_Zero_2_W  label="SD Card Slot, Raspberry Pi Zero 2 W010"
  Group = -> [Part__Feature448,Part__Feature449,Part__Feature450,Part__Feature451,Part__Feature452,Part__Feature453,Part__Feature454,Part__Feature455,Part__Feature456,Part__Feature457]
  Origin = -> Origin068
FEATURE [App::Part] SMD_Capacitor__Configurable__Raspberry_Pi_Zero_2_W_C004  label="SMD Capacitor, Configurable, Raspberry Pi Zero 2 W_C011"
  Group = -> [Part__Feature482,Part__Feature483,Part__Feature484]
  Origin = -> Origin072
FEATURE [App::Part] SMD_Capacitor__Configurable__Raspberry_Pi_Zero_2_W_C005  label="SMD Capacitor, Configurable, Raspberry Pi Zero 2 W_C015"
  Group = -> [Part__Feature485,Part__Feature486,Part__Feature487]
  Origin = -> Origin073
FEATURE [App::Part] SMD_Capacitor__Configurable__Raspberry_Pi_Zero_2_W_C006  label="SMD Capacitor, Configurable, Raspberry Pi Zero 2 W_C019"
  Group = -> [Part__Feature488,Part__Feature489,Part__Feature490]
  Origin = -> Origin074
FEATURE [App::Part] SMD_Capacitor__Configurable__Raspberry_Pi_Zero_2_W_C007  label="SMD Capacitor, Configurable, Raspberry Pi Zero 2 W_C023"
  Group = -> [Part__Feature491,Part__Feature492,Part__Feature493]
  Origin = -> Origin075
FEATURE [App::Part] SMD_Capacitor__Configurable__Raspberry_Pi_Zero_2_W_C008  label="SMD Capacitor, Configurable, Raspberry Pi Zero 2 W_C027"
  Group = -> [Part__Feature494,Part__Feature495,Part__Feature496]
  Origin = -> Origin076
FEATURE [App::Part] SMD_Capacitor__Configurable__Raspberry_Pi_Zero_2_W_C009  label="SMD Capacitor, Configurable, Raspberry Pi Zero 2 W_C031"
  Group = -> [Part__Feature497,Part__Feature498,Part__Feature499]
  Origin = -> Origin077
FEATURE [App::Part] SMD_Capacitor__Configurable__Raspberry_Pi_Zero_2_W_C010  label="SMD Capacitor, Configurable, Raspberry Pi Zero 2 W_C035"
  Group = -> [Part__Feature500,Part__Feature501,Part__Feature502]
  Origin = -> Origin078
FEATURE [App::Part] SMD_Capacitor__Configurable__Raspberry_Pi_Zero_2_W_C011  label="SMD Capacitor, Configurable, Raspberry Pi Zero 2 W_C039"
  Group = -> [Part__Feature503,Part__Feature504,Part__Feature505]
  Origin = -> Origin079
FEATURE [App::Part] SMD_Capacitor__Configurable__Raspberry_Pi_Zero_2_W_C012  label="SMD Capacitor, Configurable, Raspberry Pi Zero 2 W_C049"
  Group = -> [Part__Feature512,Part__Feature513,Part__Feature514]
  Origin = -> Origin082
FEATURE [App::Part] SMD_Capacitor__Configurable__Raspberry_Pi_Zero_2_W_C013  label="SMD Capacitor, Configurable, Raspberry Pi Zero 2 W_C053"
  Group = -> [Part__Feature515,Part__Feature516,Part__Feature517]
  Origin = -> Origin083
FEATURE [App::Part] SMD_Capacitor__Configurable__Raspberry_Pi_Zero_2_W_C014  label="SMD Capacitor, Configurable, Raspberry Pi Zero 2 W_C057"
  Group = -> [Part__Feature518,Part__Feature519,Part__Feature520]
  Origin = -> Origin017
FEATURE [App::Part] SMD_Capacitor__Configurable__Raspberry_Pi_Zero_2_W_C015  label="SMD Capacitor, Configurable, Raspberry Pi Zero 2 W_C061"
  Group = -> [Part__Feature521,Part__Feature522,Part__Feature523]
  Origin = -> Origin018
FEATURE [App::Part] SMD_Capacitor__Configurable__Raspberry_Pi_Zero_2_W_C016  label="SMD Capacitor, Configurable, Raspberry Pi Zero 2 W_C065"
  Group = -> [Part__Feature524,Part__Feature525,Part__Feature526]
  Origin = -> Origin084
FEATURE [App::Part] SMD_Capacitor__Configurable__Raspberry_Pi_Zero_2_W_C017  label="SMD Capacitor, Configurable, Raspberry Pi Zero 2 W_C069"
  Group = -> [Part__Feature527,Part__Feature528,Part__Feature529]
  Origin = -> Origin085
FEATURE [App::Part] SMD_Capacitor__Configurable__Raspberry_Pi_Zero_2_W_C018  label="SMD Capacitor, Configurable, Raspberry Pi Zero 2 W_C073"
  Group = -> [Part__Feature530,Part__Feature531,Part__Feature532]
  Origin = -> Origin021
FEATURE [App::Part] SMD_Capacitor__Configurable__Raspberry_Pi_Zero_2_W_C019  label="SMD Capacitor, Configurable, Raspberry Pi Zero 2 W_C077"
  Group = -> [Part__Feature533,Part__Feature534,Part__Feature535]
  Origin = -> Origin022
FEATURE [App::Part] SMD_Capacitor__Configurable__Raspberry_Pi_Zero_2_W_C020  label="SMD Capacitor, Configurable, Raspberry Pi Zero 2 W_C081"
  Group = -> [Part__Feature536,Part__Feature537,Part__Feature538]
  Origin = -> Origin023
FEATURE [App::Part] SMD_Capacitor__Configurable__Raspberry_Pi_Zero_2_W_C021  label="SMD Capacitor, Configurable, Raspberry Pi Zero 2 W_C085"
  Group = -> [Part__Feature539,Part__Feature540,Part__Feature541]
  Origin = -> Origin024
FEATURE [App::Part] SMD_Capacitor__Configurable__Raspberry_Pi_Zero_2_W_C022  label="SMD Capacitor, Configurable, Raspberry Pi Zero 2 W_C089"
  Group = -> [Part__Feature542,Part__Feature543,Part__Feature544]
  Origin = -> Origin025
FEATURE [App::Part] SMD_Capacitor__Configurable__Raspberry_Pi_Zero_2_W_C023  label="SMD Capacitor, Configurable, Raspberry Pi Zero 2 W_C093"
  Group = -> [Part__Feature545,Part__Feature546,Part__Feature547]
  Origin = -> Origin026
FEATURE [App::Part] SMD_Capacitor__Configurable__Raspberry_Pi_Zero_2_W_C024  label="SMD Capacitor, Configurable, Raspberry Pi Zero 2 W_C097"
  Group = -> [Part__Feature548,Part__Feature549,Part__Feature550]
  Origin = -> Origin027
FEATURE [App::Part] SMD_Capacitor__Configurable__Raspberry_Pi_Zero_2_W_C025  label="SMD Capacitor, Configurable, Raspberry Pi Zero 2 W_C101"
  Group = -> [Part__Feature551,Part__Feature552,Part__Feature553]
  Origin = -> Origin028
FEATURE [App::Part] SMD_Capacitor__Configurable__Raspberry_Pi_Zero_2_W_C026  label="SMD Capacitor, Configurable, Raspberry Pi Zero 2 W_C105"
  Group = -> [Part__Feature554,Part__Feature555,Part__Feature556]
  Origin = -> Origin029
FEATURE [App::Part] SMD_Capacitor__Configurable__Raspberry_Pi_Zero_2_W_C027  label="SMD Capacitor, Configurable, Raspberry Pi Zero 2 W_C109"
  Group = -> [Part__Feature557,Part__Feature558,Part__Feature559]
  Origin = -> Origin030
FEATURE [App::Part] SMD_Capacitor__Configurable__Raspberry_Pi_Zero_2_W_C028  label="SMD Capacitor, Configurable, Raspberry Pi Zero 2 W_C113"
  Group = -> [Part__Feature560,Part__Feature561,Part__Feature562]
  Origin = -> Origin031
FEATURE [App::Part] SMD_Capacitor__Configurable__Raspberry_Pi_Zero_2_W_C029  label="SMD Capacitor, Configurable, Raspberry Pi Zero 2 W_C117"
  Group = -> [Part__Feature563,Part__Feature564,Part__Feature565]
  Origin = -> Origin032
FEATURE [App::Part] SMD_Capacitor__Configurable__Raspberry_Pi_Zero_2_W_C030  label="SMD Capacitor, Configurable, Raspberry Pi Zero 2 W_C121"
  Group = -> [Part__Feature566,Part__Feature567,Part__Feature129]
  Origin = -> Origin033
FEATURE [App::Part] SMD_Capacitor__Configurable__Raspberry_Pi_Zero_2_W_C031  label="SMD Capacitor, Configurable, Raspberry Pi Zero 2 W_C125"
  Group = -> [Part__Feature130,Part__Feature131,Part__Feature132]
  Origin = -> Origin034
FEATURE [App::Part] SMD_Capacitor__Configurable__Raspberry_Pi_Zero_2_W_C032  label="SMD Capacitor, Configurable, Raspberry Pi Zero 2 W_C129"
  Group = -> [Part__Feature133,Part__Feature134,Part__Feature135]
  Origin = -> Origin035
FEATURE [App::Part] SMD_Capacitor__Configurable__Raspberry_Pi_Zero_2_W_C033  label="SMD Capacitor, Configurable, Raspberry Pi Zero 2 W_C133"
  Group = -> [Part__Feature136,Part__Feature137,Part__Feature138]
  Origin = -> Origin036
FEATURE [App::Part] SMD_Capacitor__Configurable__Raspberry_Pi_Zero_2_W_C034  label="SMD Capacitor, Configurable, Raspberry Pi Zero 2 W_C137"
  Group = -> [Part__Feature139,Part__Feature140,Part__Feature141]
  Origin = -> Origin037
FEATURE [App::Part] SMD_Capacitor__Configurable__Raspberry_Pi_Zero_2_W_C035  label="SMD Capacitor, Configurable, Raspberry Pi Zero 2 W_C141"
  Group = -> [Part__Feature142,Part__Feature143,Part__Feature144]
  Origin = -> Origin086
FEATURE [App::Part] SMD_Capacitor__Configurable__Raspberry_Pi_Zero_2_W_C036  label="SMD Capacitor, Configurable, Raspberry Pi Zero 2 W_C145"
  Group = -> [Part__Feature145,Part__Feature146,Part__Feature147]
  Origin = -> Origin087
FEATURE [App::Part] SMD_Capacitor__Configurable__Raspberry_Pi_Zero_2_W_C037  label="SMD Capacitor, Configurable, Raspberry Pi Zero 2 W_C149"
  Group = -> [Part__Feature148,Part__Feature149,Part__Feature150]
  Origin = -> Origin088
FEATURE [App::Part] SMD_Capacitor__Configurable__Raspberry_Pi_Zero_2_W_C038  label="SMD Capacitor, Configurable, Raspberry Pi Zero 2 W_C153"
  Group = -> [Part__Feature151,Part__Feature152,Part__Feature153]
  Origin = -> Origin089
FEATURE [App::Part] SMD_Capacitor__Configurable__Raspberry_Pi_Zero_2_W_C039  label="SMD Capacitor, Configurable, Raspberry Pi Zero 2 W_C157"
  Group = -> [Part__Feature154,Part__Feature155,Part__Feature156]
  Origin = -> Origin090
FEATURE [App::Part] SMD_Capacitor__Configurable__Raspberry_Pi_Zero_2_W_C040  label="SMD Capacitor, Configurable, Raspberry Pi Zero 2 W_C161"
  Group = -> [Part__Feature157,Part__Feature158,Part__Feature159]
  Origin = -> Origin091
FEATURE [App::Part] SMD_Capacitor__Configurable__Raspberry_Pi_Zero_2_W_C041  label="SMD Capacitor, Configurable, Raspberry Pi Zero 2 W_C165"
  Group = -> [Part__Feature160,Part__Feature161,Part__Feature162]
  Origin = -> Origin092
FEATURE [App::Part] SMD_Capacitor__Configurable__Raspberry_Pi_Zero_2_W_C042  label="SMD Capacitor, Configurable, Raspberry Pi Zero 2 W_C169"
  Group = -> [Part__Feature163,Part__Feature164,Part__Feature165]
  Origin = -> Origin093
FEATURE [App::Part] SMD_Capacitor__Configurable__Raspberry_Pi_Zero_2_W_C043  label="SMD Capacitor, Configurable, Raspberry Pi Zero 2 W_C173"
  Group = -> [Part__Feature166,Part__Feature167,Part__Feature168]
  Origin = -> Origin094
FEATURE [App::Part] SMD_Capacitor__Configurable__Raspberry_Pi_Zero_2_W_C044  label="SMD Capacitor, Configurable, Raspberry Pi Zero 2 W_C177"
  Group = -> [Part__Feature169,Part__Feature170,Part__Feature171]
  Origin = -> Origin095
FEATURE [App::Part] SMD_Capacitor__Configurable__Raspberry_Pi_Zero_2_W_C045  label="SMD Capacitor, Configurable, Raspberry Pi Zero 2 W_C181"
  Group = -> [Part__Feature172,Part__Feature173,Part__Feature174]
  Origin = -> Origin096
FEATURE [App::Part] SMD_Capacitor__Configurable__Raspberry_Pi_Zero_2_W_C046  label="SMD Capacitor, Configurable, Raspberry Pi Zero 2 W_C185"
  Group = -> [Part__Feature175,Part__Feature176,Part__Feature177]
  Origin = -> Origin097
FEATURE [App::Part] SMD_Capacitor__Configurable__Raspberry_Pi_Zero_2_W_C047  label="SMD Capacitor, Configurable, Raspberry Pi Zero 2 W_C189"
  Group = -> [Part__Feature178,Part__Feature179,Part__Feature180]
  Origin = -> Origin098
FEATURE [App::Part] SMD_Capacitor__Configurable__Raspberry_Pi_Zero_2_W_C048  label="SMD Capacitor, Configurable, Raspberry Pi Zero 2 W_C193"
  Group = -> [Part__Feature181,Part__Feature182,Part__Feature183]
  Origin = -> Origin099
FEATURE [App::Part] SMD_Capacitor__Configurable__Raspberry_Pi_Zero_2_W_C049  label="SMD Capacitor, Configurable, Raspberry Pi Zero 2 W_C197"
  Group = -> [Part__Feature184,Part__Feature185,Part__Feature186]
  Origin = -> Origin100
FEATURE [App::Part] SMD_Capacitor__Configurable__Raspberry_Pi_Zero_2_W_C050  label="SMD Capacitor, Configurable, Raspberry Pi Zero 2 W_C201"
  Group = -> [Part__Feature187,Part__Feature188,Part__Feature189]
  Origin = -> Origin101
FEATURE [App::Part] SMD_Capacitor__Configurable__Raspberry_Pi_Zero_2_W_C051  label="SMD Capacitor, Configurable, Raspberry Pi Zero 2 W_C205"
  Group = -> [Part__Feature190,Part__Feature191,Part__Feature192]
  Origin = -> Origin102
FEATURE [App::Part] SMD_Capacitor__Configurable__Raspberry_Pi_Zero_2_W_C052  label="SMD Capacitor, Configurable, Raspberry Pi Zero 2 W_C209"
  Group = -> [Part__Feature193,Part__Feature194,Part__Feature195]
  Origin = -> Origin103
FEATURE [App::Part] SMD_Capacitor__Configurable__Raspberry_Pi_Zero_2_W_C053  label="SMD Capacitor, Configurable, Raspberry Pi Zero 2 W_C213"
  Group = -> [Part__Feature196,Part__Feature197,Part__Feature198]
  Origin = -> Origin104
FEATURE [App::Part] SMD_Capacitor__Configurable__Raspberry_Pi_Zero_2_W_C054  label="SMD Capacitor, Configurable, Raspberry Pi Zero 2 W_C217"
  Group = -> [Part__Feature199,Part__Feature200,Part__Feature201]
  Origin = -> Origin105
FEATURE [App::Part] SMD_Capacitor__Configurable__Raspberry_Pi_Zero_2_W_C055  label="SMD Capacitor, Configurable, Raspberry Pi Zero 2 W_C221"
  Group = -> [Part__Feature265,Part__Feature266,Part__Feature267]
  Origin = -> Origin127
FEATURE [App::Part] SMD_Capacitor__Configurable__Raspberry_Pi_Zero_2_W_C1  label="SMD Capacitor, Configurable, Raspberry Pi Zero 2 W_C004"
  Group = -> [Part__Feature469,Part__Feature470,Part__Feature471]
  Origin = -> Origin069
FEATURE [App::Part] SMD_Capacitor__Configurable__Raspberry_Pi_Zero_2_W_C10  label="SMD Capacitor, Configurable, Raspberry Pi Zero 2 W_C045"
  Group = -> [Part__Feature509,Part__Feature510,Part__Feature511]
  Origin = -> Origin081
FEATURE [App::Part] SMD_Capacitor__Configurable__Raspberry_Pi_Zero_2_W_C2  label="SMD Capacitor, Configurable, Raspberry Pi Zero 2 W_C042"
  Group = -> [Part__Feature506,Part__Feature507,Part__Feature508]
  Origin = -> Origin080
FEATURE [App::Part] SMD_Capacitor__Configurable__Raspberry_Pi_Zero_2_W_C3  label="SMD Capacitor, Configurable, Raspberry Pi Zero 2 W_C007"
  Group = -> [Part__Feature479,Part__Feature480,Part__Feature481]
  Origin = -> Origin071
FEATURE [App::Part] SMD_Resistor__Configurable__Raspberry_Pi_Zero_2_W_R002  label="SMD Resistor, Configurable, Raspberry Pi Zero 2 W_R008"
  Group = -> [Part__Feature205,Part__Feature206,Part__Feature207]
  Origin = -> Origin107
FEATURE [App::Part] SMD_Resistor__Configurable__Raspberry_Pi_Zero_2_W_R003  label="SMD Resistor, Configurable, Raspberry Pi Zero 2 W_R012"
  Group = -> [Part__Feature208,Part__Feature209,Part__Feature210]
  Origin = -> Origin108
FEATURE [App::Part] SMD_Resistor__Configurable__Raspberry_Pi_Zero_2_W_R004  label="SMD Resistor, Configurable, Raspberry Pi Zero 2 W_R019"
  Group = -> [Part__Feature214,Part__Feature215,Part__Feature216]
  Origin = -> Origin110
FEATURE [App::Part] SMD_Resistor__Configurable__Raspberry_Pi_Zero_2_W_R005  label="SMD Resistor, Configurable, Raspberry Pi Zero 2 W_R023"
  Group = -> [Part__Feature217,Part__Feature218,Part__Feature219]
  Origin = -> Origin111
FEATURE [App::Part] SMD_Resistor__Configurable__Raspberry_Pi_Zero_2_W_R006  label="SMD Resistor, Configurable, Raspberry Pi Zero 2 W_R027"
  Group = -> [Part__Feature220,Part__Feature221,Part__Feature222]
  Origin = -> Origin112
FEATURE [App::Part] SMD_Resistor__Configurable__Raspberry_Pi_Zero_2_W_R007  label="SMD Resistor, Configurable, Raspberry Pi Zero 2 W_R031"
  Group = -> [Part__Feature223,Part__Feature224,Part__Feature225]
  Origin = -> Origin113
FEATURE [App::Part] SMD_Resistor__Configurable__Raspberry_Pi_Zero_2_W_R008  label="SMD Resistor, Configurable, Raspberry Pi Zero 2 W_R035"
  Group = -> [Part__Feature226,Part__Feature227,Part__Feature228]
  Origin = -> Origin114
FEATURE [App::Part] SMD_Resistor__Configurable__Raspberry_Pi_Zero_2_W_R009  label="SMD Resistor, Configurable, Raspberry Pi Zero 2 W_R039"
  Group = -> [Part__Feature229,Part__Feature230,Part__Feature231]
  Origin = -> Origin115
FEATURE [App::Part] SMD_Resistor__Configurable__Raspberry_Pi_Zero_2_W_R010  label="SMD Resistor, Configurable, Raspberry Pi Zero 2 W_R043"
  Group = -> [Part__Feature232,Part__Feature233,Part__Feature234]
  Origin = -> Origin116
FEATURE [App::Part] SMD_Resistor__Configurable__Raspberry_Pi_Zero_2_W_R011  label="SMD Resistor, Configurable, Raspberry Pi Zero 2 W_R047"
  Group = -> [Part__Feature235,Part__Feature236,Part__Feature237]
  Origin = -> Origin117
FEATURE [App::Part] SMD_Resistor__Configurable__Raspberry_Pi_Zero_2_W_R012  label="SMD Resistor, Configurable, Raspberry Pi Zero 2 W_R051"
  Group = -> [Part__Feature238,Part__Feature239,Part__Feature240]
  Origin = -> Origin118
FEATURE [App::Part] SMD_Resistor__Configurable__Raspberry_Pi_Zero_2_W_R013  label="SMD Resistor, Configurable, Raspberry Pi Zero 2 W_R055"
  Group = -> [Part__Feature241,Part__Feature242,Part__Feature243]
  Origin = -> Origin119
FEATURE [App::Part] SMD_Resistor__Configurable__Raspberry_Pi_Zero_2_W_R014  label="SMD Resistor, Configurable, Raspberry Pi Zero 2 W_R059"
  Group = -> [Part__Feature244,Part__Feature245,Part__Feature246]
  Origin = -> Origin120
FEATURE [App::Part] SMD_Resistor__Configurable__Raspberry_Pi_Zero_2_W_R015  label="SMD Resistor, Configurable, Raspberry Pi Zero 2 W_R063"
  Group = -> [Part__Feature247,Part__Feature248,Part__Feature249]
  Origin = -> Origin121
FEATURE [App::Part] SMD_Resistor__Configurable__Raspberry_Pi_Zero_2_W_R016  label="SMD Resistor, Configurable, Raspberry Pi Zero 2 W_R067"
  Group = -> [Part__Feature250,Part__Feature251,Part__Feature252]
  Origin = -> Origin122
FEATURE [App::Part] SMD_Resistor__Configurable__Raspberry_Pi_Zero_2_W_R017  label="SMD Resistor, Configurable, Raspberry Pi Zero 2 W_R071"
  Group = -> [Part__Feature253,Part__Feature254,Part__Feature255]
  Origin = -> Origin123
FEATURE [App::Part] SMD_Resistor__Configurable__Raspberry_Pi_Zero_2_W_R018  label="SMD Resistor, Configurable, Raspberry Pi Zero 2 W_R075"
  Group = -> [Part__Feature256,Part__Feature257,Part__Feature258]
  Origin = -> Origin124
FEATURE [App::Part] SMD_Resistor__Configurable__Raspberry_Pi_Zero_2_W_R019  label="SMD Resistor, Configurable, Raspberry Pi Zero 2 W_R079"
  Group = -> [Part__Feature259,Part__Feature260,Part__Feature261]
  Origin = -> Origin125
FEATURE [App::Part] SMD_Resistor__Configurable__Raspberry_Pi_Zero_2_W_R020  label="SMD Resistor, Configurable, Raspberry Pi Zero 2 W_R083"
  Group = -> [Part__Feature262,Part__Feature263,Part__Feature264]
  Origin = -> Origin126
FEATURE [App::Part] SMD_Resistor__Configurable__Raspberry_Pi_Zero_2_W_R1  label="SMD Resistor, Configurable, Raspberry Pi Zero 2 W_R004"
  Group = -> [Part__Feature202,Part__Feature203,Part__Feature204]
  Origin = -> Origin106
FEATURE [App::Part] SMD_Resistor__Configurable__Raspberry_Pi_Zero_2_W_R12  label="SMD Resistor, Configurable, Raspberry Pi Zero 2 W_R015"
  Group = -> [Part__Feature211,Part__Feature212,Part__Feature213]
  Origin = -> Origin109
FEATURE [App::Part] Raspberry_Pi_Zero_2_W_with_40_pin_male_connector_v4  label="RaspberryPiZero2W"
  Group = -> [Part__Feature439,Part__Feature440,MicroUSB_Port__Raspberry_Pi_Zero_2_W,SD_Card_Slot__Raspberry_Pi_Zero_2_W,Part__Feature458,Part__Feature459,Part__Feature460,Part__Feature461,Part__Feature462,Part__Feature463,Part__Feature464,Part__Feature465,Part__Feature466,Part__Feature467,Part__Feature468,SMD_Capacitor__Configurable__Raspberry_Pi_Zero_2_W_C1,MicroUSB_Port__Raspberry_Pi_Zero_2_W001,+77 more]
  Origin = -> Origin128
  Placement = pos=(127.9,-102.5,-146) rot=(0.57735,0.57735,0.57735;2.0944rad)
FEATURE [Part::Feature] Part__Feature568  label="fan"
  Placement = pos=(22.5475,33.2927,6) rot=(-0.588042,0.808831,0;3.14159rad)
  shape: bbox 15 x 15 x 4.502 mm, 133 faces (baked)
FEATURE [Part::Feature] Part__Feature569  label="plastic"
  Placement = pos=(22,36,-5.99e-13) rot=(1,0,0;3.14159rad)
  shape: bbox 1 x 1 x 12 mm, 5 faces (baked)
FEATURE [Part::Feature] Part__Feature570  label="plastic001"
  Placement = pos=(22,36,-5.99e-13) rot=(1,0,0;3.14159rad)
  shape: bbox 1 x 1 x 12 mm, 5 faces (baked)
FEATURE [Part::Feature] Part__Feature571  label="plastic002"
  Placement = pos=(22,36,-5.99e-13) rot=(1,0,0;3.14159rad)
  shape: bbox 1 x 1 x 12 mm, 5 faces (baked)
FEATURE [Part::Feature] Part__Feature572  label="plastic003"
  Placement = pos=(22,36,-5.99e-13) rot=(1,0,0;3.14159rad)
  shape: bbox 1 x 1 x 12 mm, 5 faces (baked)
FEATURE [Part::Feature] Part__Feature573  label="plastic004"
  Placement = pos=(22,36,-5.99e-13) rot=(1,0,0;3.14159rad)
  shape: bbox 7 x 11 x 3.1 mm, 19 faces (baked)
FEATURE [Part::Feature] Part__Feature574  label="plastic005"
  Placement = pos=(22,36,-5.99e-13) rot=(1,0,0;3.14159rad)
  shape: bbox 1.4 x 1 x 1.7 mm, 6 faces (baked)
FEATURE [Part::Feature] Part__Feature575  label="plastic006"
  Placement = pos=(22,36,-5.99e-13) rot=(1,0,0;3.14159rad)
  shape: bbox 1 x 1.4 x 1.7 mm, 6 faces (baked)
FEATURE [Part::Feature] Part__Feature576  label="plastic007"
  Placement = pos=(22,36,-5.99e-13) rot=(1,0,0;3.14159rad)
  shape: bbox 1 x 1.4 x 1.7 mm, 6 faces (baked)
FEATURE [Part::Feature] Part__Feature577  label="plastic008"
  Placement = pos=(22,36,-5.99e-13) rot=(1,0,0;3.14159rad)
  shape: bbox 1.4 x 1 x 1.7 mm, 6 faces (baked)
FEATURE [Part::Feature] Part__Feature578  label="plastic009"
  Placement = pos=(22,36,-5.99e-13) rot=(1,0,0;3.14159rad)
  shape: bbox 1 x 1.4 x 1.7 mm, 6 faces (baked)
FEATURE [Part::Feature] Part__Feature579  label="plastic010"
  Placement = pos=(22,36,-5.99e-13) rot=(1,0,0;3.14159rad)
  shape: bbox 1 x 1.4 x 1.7 mm, 6 faces (baked)
FEATURE [Part::Feature] Part__Feature580  label="plastic011"
  Placement = pos=(22,36,-5.99e-13) rot=(1,0,0;3.14159rad)
  shape: bbox 1 x 1.4 x 1.7 mm, 6 faces (baked)
FEATURE [Part::Feature] Part__Feature581  label="plastic012"
  Placement = pos=(22,36,-5.99e-13) rot=(1,0,0;3.14159rad)
  shape: bbox 1 x 1.4 x 1.7 mm, 6 faces (baked)
FEATURE [Part::Feature] Part__Feature582  label="plastic013"
  Placement = pos=(22,36,-5.99e-13) rot=(1,0,0;3.14159rad)
  shape: bbox 1.4 x 1 x 1.7 mm, 6 faces (baked)
FEATURE [Part::Feature] Part__Feature583  label="plastic014"
  Placement = pos=(22,36,-5.99e-13) rot=(1,0,0;3.14159rad)
  shape: bbox 1.4 x 1 x 1.7 mm, 6 faces (baked)
FEATURE [Part::Feature] Part__Feature584  label="plastic015"
  Placement = pos=(22,36,-5.99e-13) rot=(1,0,0;3.14159rad)
  shape: bbox 1.4 x 1 x 1.7 mm, 6 faces (baked)
FEATURE [Part::Feature] Part__Feature585  label="plastic016"
  Placement = pos=(22,36,-5.99e-13) rot=(1,0,0;3.14159rad)
  shape: bbox 1 x 1.4 x 1.7 mm, 6 faces (baked)
FEATURE [Part::Feature] Part__Feature586  label="plastic017"
  Placement = pos=(22,36,-5.99e-13) rot=(1,0,0;3.14159rad)
  shape: bbox 1.4 x 1 x 1.7 mm, 6 faces (baked)
FEATURE [Part::Feature] Part__Feature587  label="plastic018"
  Placement = pos=(22,36,-5.99e-13) rot=(1,0,0;3.14159rad)
  shape: bbox 1 x 1.4 x 1.7 mm, 6 faces (baked)
FEATURE [Part::Feature] Part__Feature588  label="plastic019"
  Placement = pos=(22,36,-5.99e-13) rot=(1,0,0;3.14159rad)
  shape: bbox 12.54 x 4.701 x 4.3 mm, 21 faces (baked)
FEATURE [Part::Feature] Part__Feature589  label="plastic020"
  Placement = pos=(22,36,-5.99e-13) rot=(1,0,0;3.14159rad)
  shape: bbox 16.75 x 16 x 6.5 mm, 18 faces (baked)
FEATURE [Part::Feature] Part__Feature590  label="metal_cover_connector"
  Placement = pos=(-2,18.5,11.5) rot=(0,0.707107,0.707107;3.14159rad)
  shape: bbox 48 x 37 x 6 mm, 58 faces (baked)
FEATURE [Part::Feature] Part__Feature591  label="metal_cover_fan"
  Placement = pos=(-2,18.5,0.5) rot=(0,-0.707107,0.707107;3.14159rad)
  shape: bbox 48 x 37 x 6 mm, 63 faces (baked)
FEATURE [Part::Feature] Part__Feature592  label="1_27mm_pin_right_angle"
  Placement = pos=(-0.770082,-1.65718,-0.233527) rot=(0,0,1;0rad)
  shape: bbox 2.2 x 4.2 x 0.4 mm, 17 faces (baked)
FEATURE [Part::Feature] Part__Feature593  label="1_27mm_plastic_for_pin"
  Placement = pos=(-0.452582,-1.45718,-0.233527) rot=(0,1,0;1.5708rad)
  shape: bbox 1.905 x 1 x 1.27 mm, 10 faces (baked)
FEATURE [Part::Feature] Part__Feature594  label="1_27mm_pin_right_angle001"
  Placement = pos=(-0.770082,-1.65718,-0.233527) rot=(0,0,1;0rad)
  shape: bbox 2.2 x 4.2 x 0.4 mm, 17 faces (baked)
FEATURE [Part::Feature] Part__Feature595  label="1_27mm_plastic_for_pin001"
  Placement = pos=(-0.452582,-1.45718,-0.233527) rot=(0,1,0;1.5708rad)
  shape: bbox 1.905 x 1 x 1.27 mm, 10 faces (baked)
FEATURE [Part::Feature] Part__Feature596  label="1_27mm_pin_right_angle002"
  Placement = pos=(-0.770082,-1.65718,-0.233527) rot=(0,0,1;0rad)
  shape: bbox 2.2 x 4.2 x 0.4 mm, 17 faces (baked)
FEATURE [Part::Feature] Part__Feature597  label="1_27mm_plastic_for_pin002"
  Placement = pos=(-0.452582,-1.45718,-0.233527) rot=(0,1,0;1.5708rad)
  shape: bbox 1.905 x 1 x 1.27 mm, 10 faces (baked)
FEATURE [Part::Feature] Part__Feature598  label="1_27mm_pin_right_angle003"
  Placement = pos=(-0.770082,-1.65718,-0.233527) rot=(0,0,1;0rad)
  shape: bbox 2.2 x 4.2 x 0.4 mm, 17 faces (baked)
FEATURE [Part::Feature] Part__Feature599  label="1_27mm_plastic_for_pin003"
  Placement = pos=(-0.452582,-1.45718,-0.233527) rot=(0,1,0;1.5708rad)
  shape: bbox 1.905 x 1 x 1.27 mm, 10 faces (baked)
FEATURE [Part::Feature] Part__Feature600  label="1_27mm_pin_right_angle004"
  Placement = pos=(-0.770082,-1.65718,-0.233527) rot=(0,0,1;0rad)
  shape: bbox 2.2 x 4.2 x 0.4 mm, 17 faces (baked)
FEATURE [Part::Feature] Part__Feature601  label="1_27mm_plastic_for_pin004"
  Placement = pos=(-0.452582,-1.45718,-0.233527) rot=(0,1,0;1.5708rad)
  shape: bbox 1.905 x 1 x 1.27 mm, 10 faces (baked)
FEATURE [Part::Feature] Part__Feature602  label="1_27mm_pin_right_angle005"
  Placement = pos=(-0.770082,-1.65718,-0.233527) rot=(0,0,1;0rad)
  shape: bbox 2.2 x 4.2 x 0.4 mm, 17 faces (baked)
FEATURE [Part::Feature] Part__Feature603  label="1_27mm_plastic_for_pin005"
  Placement = pos=(-0.452582,-1.45718,-0.233527) rot=(0,1,0;1.5708rad)
  shape: bbox 1.905 x 1 x 1.27 mm, 10 faces (baked)
FEATURE [Part::Feature] Part__Feature604  label="1_27mm_pin_right_angle006"
  Placement = pos=(-0.770082,-1.65718,-0.233527) rot=(0,0,1;0rad)
  shape: bbox 2.2 x 4.2 x 0.4 mm, 17 faces (baked)
FEATURE [Part::Feature] Part__Feature605  label="1_27mm_plastic_for_pin006"
  Placement = pos=(-0.452582,-1.45718,-0.233527) rot=(0,1,0;1.5708rad)
  shape: bbox 1.905 x 1 x 1.27 mm, 10 faces (baked)
FEATURE [Part::Feature] Part__Feature606  label="1_27mm_pin_right_angle007"
  Placement = pos=(-0.770082,-1.65718,-0.233527) rot=(0,0,1;0rad)
  shape: bbox 2.2 x 4.2 x 0.4 mm, 17 faces (baked)
FEATURE [Part::Feature] Part__Feature607  label="1_27mm_plastic_for_pin007"
  Placement = pos=(-0.452582,-1.45718,-0.233527) rot=(0,1,0;1.5708rad)
  shape: bbox 1.905 x 1 x 1.27 mm, 10 faces (baked)
FEATURE [Part::Feature] Part__Feature608  label="1_27mm_pin_right_angle008"
  Placement = pos=(-0.770082,-1.65718,-0.233527) rot=(0,0,1;0rad)
  shape: bbox 2.2 x 4.2 x 0.4 mm, 17 faces (baked)
FEATURE [Part::Feature] Part__Feature609  label="1_27mm_plastic_for_pin008"
  Placement = pos=(-0.452582,-1.45718,-0.233527) rot=(0,1,0;1.5708rad)
  shape: bbox 1.905 x 1 x 1.27 mm, 10 faces (baked)
FEATURE [Part::Feature] Part__Feature610  label="1_27mm_pin_right_angle009"
  Placement = pos=(-0.770082,-1.65718,-0.233527) rot=(0,0,1;0rad)
  shape: bbox 2.2 x 4.2 x 0.4 mm, 17 faces (baked)
FEATURE [Part::Feature] Part__Feature611  label="1_27mm_plastic_for_pin009"
  Placement = pos=(-0.452582,-1.45718,-0.233527) rot=(0,1,0;1.5708rad)
  shape: bbox 1.905 x 1 x 1.27 mm, 10 faces (baked)
FEATURE [App::Part] __27mm_single_pin_assembled  label="1_27mm_single_pin_assembled"
  Group = -> [Part__Feature592,Part__Feature593]
  Origin = -> Origin130
  Placement = pos=(-0.361489,-0.21886,0.454215) rot=(0,0,1;0rad)
FEATURE [App::Part] __27mm_single_pin_assembled001  label="1_27mm_single_pin_assembled001"
  Group = -> [Part__Feature594,Part__Feature595]
  Origin = -> Origin131
  Placement = pos=(-0.361489,-0.21886,-0.795785) rot=(0,0,1;0rad)
FEATURE [App::Part] __27mm_single_pin_assembled002  label="1_27mm_single_pin_assembled002"
  Group = -> [Part__Feature596,Part__Feature597]
  Origin = -> Origin132
  Placement = pos=(-0.361489,-0.21886,-2.04579) rot=(0,0,1;0rad)
FEATURE [App::Part] __27mm_single_pin_assembled003  label="1_27mm_single_pin_assembled003"
  Group = -> [Part__Feature598,Part__Feature599]
  Origin = -> Origin133
  Placement = pos=(-0.361489,-0.21886,-3.29579) rot=(0,0,1;0rad)
FEATURE [App::Part] __27mm_single_pin_assembled004  label="1_27mm_single_pin_assembled004"
  Group = -> [Part__Feature600,Part__Feature601]
  Origin = -> Origin134
  Placement = pos=(-0.361489,-0.21886,-4.54579) rot=(0,0,1;0rad)
FEATURE [App::Part] __27mm_single_pin_assembled005  label="1_27mm_single_pin_assembled005"
  Group = -> [Part__Feature602,Part__Feature603]
  Origin = -> Origin135
  Placement = pos=(-3.17165,-0.21886,-3.76284) rot=(0,1,0;3.14159rad)
FEATURE [App::Part] __27mm_single_pin_assembled006  label="1_27mm_single_pin_assembled006"
  Group = -> [Part__Feature604,Part__Feature605]
  Origin = -> Origin136
  Placement = pos=(-3.17165,-0.21886,-5.01284) rot=(0,1,0;3.14159rad)
FEATURE [App::Part] __27mm_single_pin_assembled007  label="1_27mm_single_pin_assembled007"
  Group = -> [Part__Feature606,Part__Feature607]
  Origin = -> Origin137
  Placement = pos=(-3.17165,-0.21886,-0.0128383) rot=(0,1,0;3.14159rad)
FEATURE [App::Part] __27mm_single_pin_assembled008  label="1_27mm_single_pin_assembled008"
  Group = -> [Part__Feature608,Part__Feature609]
  Origin = -> Origin138
  Placement = pos=(-3.17165,-0.21886,-2.51284) rot=(0,1,0;3.14159rad)
FEATURE [App::Part] __27mm_single_pin_assembled009  label="1_27mm_single_pin_assembled009"
  Group = -> [Part__Feature610,Part__Feature611]
  Origin = -> Origin139
  Placement = pos=(-3.17165,-0.21886,-1.26284) rot=(0,1,0;3.14159rad)
FEATURE [App::Part] __27mm_2x10pin  label="1_27mm_2x10pin"
  Group = -> [__27mm_single_pin_assembled,__27mm_single_pin_assembled001,__27mm_single_pin_assembled002,__27mm_single_pin_assembled003,__27mm_single_pin_assembled004,__27mm_single_pin_assembled005,__27mm_single_pin_assembled006,__27mm_single_pin_assembled007,__27mm_single_pin_assembled008,__27mm_single_pin_assembled009]
  Origin = -> Origin140
  Placement = pos=(18.0516,5.67069,10.176) rot=(1,0,0;1.5708rad)
FEATURE [App::Part] plastic  label="plastic021"
  Group = -> [Part__Feature569,Part__Feature570,Part__Feature571,Part__Feature572,Part__Feature573,Part__Feature574,Part__Feature575,Part__Feature576,Part__Feature577,Part__Feature578,Part__Feature579,Part__Feature580,Part__Feature581,Part__Feature582,Part__Feature583,Part__Feature584,Part__Feature585,Part__Feature586,Part__Feature587,Part__Feature588,Part__Feature589]
  Origin = -> Origin129
FEATURE [App::Part] pms7003
  Group = -> [Part__Feature568,plastic,Part__Feature590,Part__Feature591,__27mm_2x10pin]
  Origin = -> Origin141
  Placement = pos=(10,-61,-53) rot=(0,0,1;3.14159rad)
FEATURE [Part::Box] Box216  label="Cube216"
  AttacherType = Attacher::AttachEngine3D
  Height = 65
  Length = 15
  Placement = pos=(-22,0,-142) rot=(0,0,1;0rad)
  Width = 15
FEATURE [Part::Box] Box217  label="Cube217"
  AttacherType = Attacher::AttachEngine3D
  Height = 65
  Length = 15
  Placement = pos=(22,0,-142) rot=(0,0,1;0rad)
  Width = 15
FEATURE [Part::Box] Box218  label="Cube218"
  AttacherType = Attacher::AttachEngine3D
  Height = 65
  Length = 15
  Placement = pos=(69,0,-142) rot=(0,0,1;0rad)
  Width = 15
FEATURE [Part::Box] Box220  label="Cube220"
  AttacherType = Attacher::AttachEngine3D
  Height = 65
  Length = 15
  Placement = pos=(113,0,-142) rot=(0,0,1;0rad)
  Width = 15
FEATURE [Part::MultiFuse] Fusion129  label="Vertical_front"
  Placement = pos=(-0.5,-58.5,0) rot=(0,0,1;0rad)
  Shapes = -> [Box216,Box217,Box218,Box220]
FEATURE [Sketcher::SketchObject] Sketch012
  FullyConstrained = true
  Placement = pos=(0,0,0) rot=(0,0.707107,0.707107;3.14159rad)
  sketch-geometry (16):
    g0: LineSegment StartX=-80.36 StartY=-110.5 StartZ=0 EndX=-68.5 EndY=-110.5 EndZ=0
    g1: LineSegment StartX=-68.5 StartY=-110.5 StartZ=0 EndX=-68.5 EndY=-114.5 EndZ=0
    g2: LineSegment StartX=-68.5 StartY=-114.5 StartZ=0 EndX=-76.36 EndY=-114.5 EndZ=0
    g3: LineSegment StartX=-76.36 StartY=-114.5 StartZ=0 EndX=-76.36 EndY=-127.5 EndZ=0
    g4: LineSegment StartX=-80.36 StartY=-131.5 StartZ=0 EndX=-80.36 EndY=-110.5 EndZ=0
    g5: LineSegment StartX=-76.36 StartY=-127.5 StartZ=0 EndX=-68.56 EndY=-127.5 EndZ=0
    g6: LineSegment StartX=-68.56 StartY=-127.5 StartZ=0 EndX=-68.56 EndY=-131.5 EndZ=0
    g7: LineSegment StartX=-68.56 StartY=-131.5 StartZ=0 EndX=-80.36 EndY=-131.5 EndZ=0
    g8: LineSegment StartX=-36.5 StartY=-127.5 StartZ=0 EndX=-36.5 EndY=-131.5 EndZ=0
    g9: LineSegment StartX=-36.5 StartY=-131.5 StartZ=0 EndX=-23.5 EndY=-131.5 EndZ=0
    g10: LineSegment StartX=-23.5 StartY=-131.5 StartZ=0 EndX=-23.5 EndY=-110.5 EndZ=0
    g11: LineSegment StartX=-27.5 StartY=-114.5 StartZ=0 EndX=-27.5 EndY=-127.5 EndZ=0
    g12: LineSegment StartX=-27.5 StartY=-127.5 StartZ=0 EndX=-36.5 EndY=-127.5 EndZ=0
    g13: LineSegment StartX=-27.5 StartY=-114.5 StartZ=0 EndX=-36.5 EndY=-114.5 EndZ=0
    g14: LineSegment StartX=-36.5 StartY=-114.5 StartZ=0 EndX=-36.5 EndY=-110.5 EndZ=0
    g15: LineSegment StartX=-36.5 StartY=-110.5 StartZ=0 EndX=-23.5 EndY=-110.5 EndZ=0
  constraints (48):
    c: Horizontal(g0)
    c: Coincident(g1,g0)
    c: Coincident(g2,g1)
    c: Horizontal(g2)
    c: Vertical(g3)
    c: Coincident(g4,g0)
    c: Vertical(g4)
    c: Vertical(g1)
    c: Distance(g1) = 4
    c: Coincident(g2,g3)
    c: Coincident(g5,g3)
    c: Horizontal(g5)
    c: Coincident(g6,g5)
    c: Vertical(g6)
    c: Coincident(g7,g6)
    c: Coincident(g7,g4)
    c: Horizontal(g7)
    c: Distance(g6) = 4
    c: Distance(g0,g-1) = 110.5
    c: Distance(g4) = 21
    c: Distance(g2) = 7.86
    c: Distance(g5) = 7.8
    c: Distance(g2,g4) = 4
    c: Distance(g5,g-2) = 68.56
    c: Vertical(g8)
    c: Coincident(g9,g8)
    c: Horizontal(g9)
    c: Coincident(g10,g9)
    c: Vertical(g10)
    c: Vertical(g11)
    c: Coincident(g12,g11)
    c: Coincident(g12,g8)
    c: Horizontal(g12)
    c: Distance(g12) = 9
    c: Distance(g9,g-1) = 131.5
    c: Distance(g8) = 4
    c: Distance(g11,g-2) = 27.5
    c: Coincident(g13,g11)
    c: Horizontal(g13)
    c: Coincident(g14,g13)
    c: Vertical(g14)
    c: Coincident(g15,g14)
    c: Horizontal(g15)
    c: Coincident(g15,g10)
    c: Distance(g14) = 4
    c: Distance(g11,g10) = 4
    c: Distance(g14,g-1) = 110.5
    c: Distance(g13) = 9
FEATURE [Part::Extrusion] Extrude012
  Base = -> Sketch012
  Dir = (0,1,0)
  DirMode = 2
  FaceMakerClass = Part::FaceMakerBullseye
  LengthFwd = 45.5
  LengthRev = 0
  Placement = pos=(0,2,0) rot=(0,0,1;0rad)
  Reversed = true
  Solid = true
  Symmetric = false
FEATURE [Part::Box] Box221  label="Cube221"
  AttacherType = Attacher::AttachEngine3D
  Height = 10
  Length = 10
  Placement = pos=(27.5,-21,-114.5) rot=(0,0,1;0rad)
  Width = 23
FEATURE [Part::Cut] Cut016
  Base = -> Extrude012
  Placement = pos=(47.14,-60.5,0) rot=(0,0,1;0rad)
  Tool = -> Box221
FEATURE [Sketcher::SketchObject] Sketch013
  FullyConstrained = true
  Placement = pos=(0,0,0) rot=(0,0.707107,0.707107;3.14159rad)
  sketch-geometry (6):
    g0: Circle CenterX=-29 CenterY=-99.75 CenterZ=0 NormalX=0 NormalY=0 NormalZ=1 AngleXU=0 Radius=2
    g1: Circle CenterX=15 CenterY=-99.75 CenterZ=0 NormalX=0 NormalY=0 NormalZ=1 AngleXU=0 Radius=2
    g2: Circle CenterX=15 CenterY=-124.75 CenterZ=0 NormalX=0 NormalY=0 NormalZ=1 AngleXU=0 Radius=2
    g3: Circle CenterX=-76 CenterY=-105.5 CenterZ=0 NormalX=0 NormalY=0 NormalZ=1 AngleXU=0 Radius=2
    g4: Circle CenterX=-119.5 CenterY=-105.5 CenterZ=0 NormalX=0 NormalY=0 NormalZ=1 AngleXU=0 Radius=2
    g5: Circle CenterX=-97.75 CenterY=-67.8279 CenterZ=0 NormalX=0 NormalY=0 NormalZ=1 AngleXU=0 Radius=2
  constraints (18):
    c: Equal(g0,g1)
    c: Equal(g0,g2)
    c: Diameter(g0) = 4
    c: Distance(g0,g-2) = 29
    c: Distance(g0,g-1) = 99.75
    c: Distance(g1,g-1) = 99.75
    c: Distance(g0,g1) = 44
    c: Distance(g2,g1) = 25
    c: Distance(g2,g-2) = 15
    c: Distance(g3,g-2) = 76
    c: Distance(g3,g-1) = 105.5
    c: Equal(g3,g5)
    c: Equal(g3,g4)
    c: Diameter(g3) = 4
    c: Distance(g4,g-1) = 105.5
    c: Distance(g4,g3) = 43.5
    c: Distance(g3,g5) = 43.5
    c: Distance(g5,g4) = 43.5
FEATURE [Part::Extrusion] Extrude013  label="screw_cut_vertiical"
  Base = -> Sketch013
  Dir = (0,1,0)
  DirMode = 2
  FaceMakerClass = Part::FaceMakerBullseye
  LengthFwd = 30
  LengthRev = 0
  Placement = pos=(0,-36,0) rot=(0,0,1;0rad)
  Reversed = true
  Solid = true
  Symmetric = false
FEATURE [Part::Cut] Cut017
  Base = -> Fusion129
  Tool = -> Extrude013
FEATURE [Part::Box] Box222  label="Cube222"
  AttacherType = Attacher::AttachEngine3D
  Height = 65
  Length = 10
  Placement = pos=(-4.5,0,-142) rot=(0,0,1;0rad)
  Width = 15
FEATURE [Part::Box] Box223  label="Cube223"
  AttacherType = Attacher::AttachEngine3D
  Height = 65
  Length = 11
  Placement = pos=(36,0,-142) rot=(0,0,1;0rad)
  Width = 15
FEATURE [Part::Box] Box224  label="Cube224"
  AttacherType = Attacher::AttachEngine3D
  Height = 65
  Length = 15
  Placement = pos=(93,0,-142) rot=(0,0,1;0rad)
  Width = 15
FEATURE [Part::Box] Box225  label="Cube225"
  AttacherType = Attacher::AttachEngine3D
  Height = 65
  Length = 15
  Placement = pos=(143,15,-142) rot=(0,0,1;0rad)
  Width = 15
FEATURE [Part::Box] Box226  label="Cube226"
  AttacherType = Attacher::AttachEngine3D
  Height = 65
  Length = 15
  Placement = pos=(-37,45,-142) rot=(0,0,1;0rad)
  Width = 15
FEATURE [Part::Box] Box227  label="Cube227"
  AttacherType = Attacher::AttachEngine3D
  Height = 65
  Length = 15
  Placement = pos=(143,75,-142) rot=(0,0,1;0rad)
  Width = 15
FEATURE [Part::MultiFuse] Fusion130  label="Vertical_back"
  Placement = pos=(-0.5,-148.5,0) rot=(0,0,1;0rad)
  Shapes = -> [Box222,Box223,Box224,Box225,Box226,Box227]
FEATURE [Sketcher::SketchObject] Sketch014
  FullyConstrained = true
  Placement = pos=(0,0,0) rot=(0.57735,-0.57735,-0.57735;2.0944rad)
  sketch-geometry (2):
    g0: Circle CenterX=114.65 CenterY=-69.85 CenterZ=0 NormalX=0 NormalY=0 NormalZ=1 AngleXU=0 Radius=1.5
    g1: Circle CenterX=127.35 CenterY=-69.85 CenterZ=0 NormalX=0 NormalY=0 NormalZ=1 AngleXU=0 Radius=1.5
  constraints (6):
    c: Equal(g0,g1)
    c: Diameter(g0) = 3
    c: Distance(g0,g-1) = 69.85
    c: Distance(g0,g-2) = 114.65
    c: Distance(g1,g-1) = 69.85
    c: Distance(g0,g1) = 12.7
FEATURE [Part::Extrusion] Extrude014
  Base = -> Sketch014
  Dir = (-1,0,0)
  DirMode = 2
  FaceMakerClass = Part::FaceMakerBullseye
  LengthFwd = 30
  LengthRev = 0
  Placement = pos=(-15,0,0) rot=(0,0,1;0rad)
  Solid = true
  Symmetric = false
FEATURE [Part::Cut] Cut018  label="Sensor_Top"
  Base = -> Extrude010
  Tool = -> Extrude014
FEATURE [Part::MultiFuse] Fusion131  label="Sensor_hold"
  Shapes = -> [Cut018,Extrude009,Fusion130,Cut017,Cut016]
FEATURE [Part::Box] Box228  label="Cube228"
  AttacherType = Attacher::AttachEngine3D
  Height = 10
  Length = 10
  Placement = pos=(-7,-69,0) rot=(0,0,1;0rad)
  Width = 25
FEATURE [Part::Box] Box229  label="Cube229"
  AttacherType = Attacher::AttachEngine3D
  Height = 10
  Length = 10
  Placement = pos=(48,-69,0) rot=(0,0,1;0rad)
  Width = 25
FEATURE [Part::MultiFuse] Fusion132  label="ips_hold"
  Placement = pos=(0,0,-62) rot=(0,0,1;0rad)
  Shapes = -> [Box228,Box229]
FEATURE [Part::MultiFuse] Fusion133  label="Sensor_Hold"
  Shapes = -> [Fusion131,Fusion132]
FEATURE [Sketcher::SketchObject] Sketch015
  FullyConstrained = true
  sketch-geometry (44):
    g0: LineSegment StartX=156 StartY=-46 StartZ=0 EndX=-36.5 EndY=-46 EndZ=0
    g1: LineSegment StartX=146 StartY=-66 StartZ=0 EndX=132 EndY=-66 EndZ=0
    g2: LineSegment StartX=132 StartY=-66 StartZ=0 EndX=132 EndY=-81 EndZ=0
    g3: LineSegment StartX=132 StartY=-81 StartZ=0 EndX=144.5 EndY=-81 EndZ=0
    g4: LineSegment StartX=144.5 StartY=-81 StartZ=0 EndX=144.5 EndY=-122.5 EndZ=0
    g5: LineSegment StartX=144.5 StartY=-122.5 StartZ=0 EndX=131.5 EndY=-122.5 EndZ=0
    g6: LineSegment StartX=93 StartY=-133.5 StartZ=0 EndX=93 EndY=-89.5 EndZ=0
    g7: LineSegment StartX=93 StartY=-89.5 StartZ=0 EndX=82 EndY=-89.5 EndZ=0
    g8: LineSegment StartX=82 StartY=-89.5 StartZ=0 EndX=82 EndY=-133.5 EndZ=0
    g9: LineSegment StartX=82 StartY=-133.5 StartZ=0 EndX=72 EndY=-133.5 EndZ=0
    g10: LineSegment StartX=72 StartY=-133.5 StartZ=0 EndX=72 EndY=-89.5 EndZ=0
    g11: LineSegment StartX=72 StartY=-89.5 StartZ=0 EndX=62 EndY=-89.5 EndZ=0
    g12: LineSegment StartX=62 StartY=-89.5 StartZ=0 EndX=62 EndY=-133.5 EndZ=0
    g13: LineSegment StartX=12 StartY=-148.5 StartZ=0 EndX=156 EndY=-148.5 EndZ=0
    g14: LineSegment StartX=-36.5 StartY=-46 StartZ=0 EndX=-36.5 EndY=-56 EndZ=0
    g15: LineSegment StartX=-36.5 StartY=-56 StartZ=0 EndX=146 EndY=-56 EndZ=0
    g16: LineSegment StartX=146 StartY=-56 StartZ=0 EndX=146 EndY=-66 EndZ=0
    g17: LineSegment StartX=93 StartY=-133.5 StartZ=0 EndX=110 EndY=-133.5 EndZ=0
    g18: LineSegment StartX=110 StartY=-133.5 StartZ=0 EndX=110 EndY=-127.5 EndZ=0
    g19: LineSegment StartX=110 StartY=-127.5 StartZ=0 EndX=122.5 EndY=-127.5 EndZ=0
    g20: LineSegment StartX=122.5 StartY=-127.5 StartZ=0 EndX=122.5 EndY=-132.5 EndZ=0
    g21: LineSegment StartX=122.5 StartY=-132.5 StartZ=0 EndX=131.5 EndY=-132.5 EndZ=0
    g22: LineSegment StartX=131.5 StartY=-132.5 StartZ=0 EndX=131.5 EndY=-122.5 EndZ=0
    g23: LineSegment StartX=12 StartY=-133.5 StartZ=0 EndX=62 EndY=-133.5 EndZ=0
    g24: LineSegment StartX=12 StartY=-133.5 StartZ=0 EndX=12 EndY=-148.5 EndZ=0
    g25: LineSegment StartX=156 StartY=-148.5 StartZ=0 EndX=156 EndY=-46 EndZ=0
    g26: Circle CenterX=60 CenterY=-141 CenterZ=0 NormalX=0 NormalY=0 NormalZ=1 AngleXU=0 Radius=1.75
    g27: Circle CenterX=150 CenterY=-141 CenterZ=0 NormalX=0 NormalY=0 NormalZ=1 AngleXU=0 Radius=1.75
    g28: Circle CenterX=150 CenterY=-81 CenterZ=0 NormalX=0 NormalY=0 NormalZ=1 AngleXU=0 Radius=1.75
    g29: Circle CenterX=150 CenterY=-51 CenterZ=0 NormalX=0 NormalY=0 NormalZ=1 AngleXU=0 Radius=1.75
    g30: Circle CenterX=60 CenterY=-51 CenterZ=0 NormalX=0 NormalY=0 NormalZ=1 AngleXU=0 Radius=1.75
    g31: Circle CenterX=-30 CenterY=-51 CenterZ=0 NormalX=0 NormalY=0 NormalZ=1 AngleXU=0 Radius=1.75
    g32: Circle CenterX=67.32 CenterY=-127.35 CenterZ=0 NormalX=0 NormalY=0 NormalZ=1 AngleXU=0 Radius=1.375
    g33: Circle CenterX=87.65 CenterY=-127.35 CenterZ=0 NormalX=0 NormalY=0 NormalZ=1 AngleXU=0 Radius=1.375
    g34: Circle CenterX=87.65 CenterY=-114.65 CenterZ=0 NormalX=0 NormalY=0 NormalZ=1 AngleXU=0 Radius=1.375
    g35: Circle CenterX=67.32 CenterY=-114.65 CenterZ=0 NormalX=0 NormalY=0 NormalZ=1 AngleXU=0 Radius=1.375
    g36: Circle CenterX=67.32 CenterY=-93.3 CenterZ=0 NormalX=0 NormalY=0 NormalZ=1 AngleXU=0 Radius=1.45
    g37: Circle CenterX=87.65 CenterY=-93.3 CenterZ=0 NormalX=0 NormalY=0 NormalZ=1 AngleXU=0 Radius=1.45
    g38: Circle CenterX=67.32 CenterY=-106 CenterZ=0 NormalX=0 NormalY=0 NormalZ=1 AngleXU=0 Radius=1.45
    g39: Circle CenterX=87.65 CenterY=-106 CenterZ=0 NormalX=0 NormalY=0 NormalZ=1 AngleXU=0 Radius=1.45
    g40: Circle CenterX=116.4 CenterY=-131.5 CenterZ=0 NormalX=0 NormalY=0 NormalZ=1 AngleXU=0 Radius=1.45
    g41: Circle CenterX=139.4 CenterY=-131.5 CenterZ=0 NormalX=0 NormalY=0 NormalZ=1 AngleXU=0 Radius=1.45
    g42: Circle CenterX=139.4 CenterY=-73.5 CenterZ=0 NormalX=0 NormalY=0 NormalZ=1 AngleXU=0 Radius=1.45
    g43: Circle CenterX=150 CenterY=-111 CenterZ=0 NormalX=0 NormalY=0 NormalZ=1 AngleXU=0 Radius=1.75
  constraints (132):
    c: Horizontal(g0)
    c: Horizontal(g1)
    c: Vertical(g2)
    c: Coincident(g3,g2)
    c: Horizontal(g3)
    c: Coincident(g4,g3)
    c: Vertical(g4)
    c: Horizontal(g5)
    c: Vertical(g6)
    c: Horizontal(g7)
    c: Coincident(g8,g7)
    c: Vertical(g8)
    c: Coincident(g9,g8)
    c: Horizontal(g9)
    c: Coincident(g10,g9)
    c: Vertical(g10)
    c: Horizontal(g11)
    c: Vertical(g12)
    c: Horizontal(g13)
    c: Coincident(g14,g0)
    c: Vertical(g14)
    c: Coincident(g15,g14)
    c: Horizontal(g15)
    c: Coincident(g16,g15)
    c: Coincident(g16,g1)
    c: Vertical(g16)
    c: Distance(g23,g-1) = 133.5
    c: Distance(g13) = 144
    c: Distance(g12) = 44
    c: Coincident(g11,g12)
    c: Coincident(g11,g10)
    c: Distance(g10) = 44
    c: Distance(g9) = 10
    c: Distance(g8) = 44
    c: Coincident(g6,g7)
    c: Distance(g7) = 11
    c: Distance(g6) = 44
    c: Coincident(g17,g6)
    c: Horizontal(g17)
    c: Coincident(g18,g17)
    c: Vertical(g18)
    c: Coincident(g19,g18)
    c: Horizontal(g19)
    c: Coincident(g20,g19)
    c: Vertical(g20)
    c: Coincident(g21,g20)
    c: Horizontal(g21)
    c: Coincident(g22,g21)
    c: Coincident(g22,g5)
    c: Vertical(g22)
    c: Distance(g17) = 17
    c: Distance(g18) = 6
    c: Distance(g20) = 5
    c: Distance(g21) = 9
    c: Distance(g22) = 10
    c: Distance(g5) = 13
    c: Coincident(g5,g4)
    c: Distance(g0) = 192.5
    c: Distance(g14) = 10
    c: Distance(g15) = 182.5
    c: Distance(g16) = 10
    c: Distance(g1) = 14
    c: Coincident(g1,g2)
    c: Distance(g2) = 15
    c: Coincident(g23,g12)
    c: Horizontal(g23)
    c: Distance(g23,g-2) = 12
    c: Coincident(g24,g23)
    c: Coincident(g24,g13)
    c: Vertical(g24)
    c: Distance(g24) = 15
    c: Distance(g23) = 50
    c: Coincident(g25,g0)
    c: Vertical(g25)
    c: Coincident(g13,g25)
    c: Distance(g25) = 102.5
    c: Diameter(g31) = 3.5
    c: Distance(g31,g-1) = 51
    c: Distance(g31,g-2) = 30
    c: Distance(g30,g-1) = 51
    c: Distance(g31,g30) = 90
    c: Diameter(g30) = 3.5
    c: Distance(g29,g-1) = 51
    c: Distance(g30,g29) = 90
    c: Diameter(g29) = 3.5
    c: Diameter(g28) = 3.5
    c: Distance(g28,g-2) = 150
    c: Distance(g28,g29) = 30
    c: Distance(g43,g28) = 30
    c: Distance(g43,g27) = 30
    c: Diameter(g43) = 3.5
    c: Distance(g43,g-2) = 150
    c: Distance(g27,g-2) = 150
    c: Diameter(g27) = 3.5
    c: Distance(g26,g27) = 90
    c: Distance(g26,g-1) = 141
    c: Diameter(g26) = 3.5
    c: Distance(g32,g-1) = 127.35
    c: Distance(g32,g-2) = 67.32
    c: Distance(g33,g-1) = 127.35
    c: Distance(g32,g33) = 20.33
    c: Distance(g32,g35) = 12.7
    c: Distance(g35,g-2) = 67.32
    c: Distance(g35,g34) = 20.33
    c: Distance(g33,g34) = 12.7
    c: Distance(g38,g-2) = 67.32
    c: Distance(g38,g39) = 20.33
    c: Equal(g32,g33)
    c: Equal(g32,g34)
    c: Equal(g32,g35)
    c: Diameter(g32) = 2.75
    c: Distance(g39,g-1) = 106
    c: Distance(g39,g37) = 12.7
    c: Distance(g38,g36) = 12.7
    c: Distance(g36,g37) = 20.33
    c: Distance(g38,g-1) = 106
    c: Equal(g36,g37)
    c: Equal(g36,g38)
    c: Equal(g36,g39)
    c: Diameter(g36) = 2.9
    c: Distance(g36,g-1) = 93.3
    c: Distance(g40,g-2) = 116.4
    c: Distance(g40,g-1) = 131.5
    c: Distance(g41,g-1) = 131.5
    c: Distance(g40,g41) = 23
    c: Distance(g41,g42) = 58
    c: Distance(g42,g-2) = 139.4
    c: Equal(g42,g41)
    c: Equal(g42,g40)
    c: Diameter(g42) = 2.9
    c: Distance(g19) = 12.5
    c: Distance(g11) = 10
FEATURE [Part::Extrusion] Extrude015
  Base = -> Sketch015
  Dir = (0,0,1)
  DirMode = 2
  FaceMakerClass = Part::FaceMakerBullseye
  LengthFwd = 10
  LengthRev = 0
  Placement = pos=(0,0,-157) rot=(0,0,1;0rad)
  Solid = true
  Symmetric = false
FEATURE [Sketcher::SketchObject] Sketch016
  FullyConstrained = true
  Placement = pos=(0,0,0) rot=(0,0.707107,0.707107;3.14159rad)
  sketch-geometry (18):
    g0: LineSegment StartX=16.53 StartY=-147 StartZ=0 EndX=16.53 EndY=-53.5 EndZ=0
    g1: LineSegment StartX=-42 StartY=-102 StartZ=0 EndX=-42 EndY=-147 EndZ=0
    g2: LineSegment StartX=-42 StartY=-147 StartZ=0 EndX=-27.47 EndY=-147 EndZ=0
    g3: LineSegment StartX=-27.47 StartY=-147 StartZ=0 EndX=-27.47 EndY=-117 EndZ=0
    g4: LineSegment StartX=-27.47 StartY=-117 StartZ=0 EndX=2.53 EndY=-117 EndZ=0
    g5: LineSegment StartX=2.53 StartY=-117 StartZ=0 EndX=2.53 EndY=-147 EndZ=0
    g6: LineSegment StartX=2.53 StartY=-147 StartZ=0 EndX=16.53 EndY=-147 EndZ=0
    g7: LineSegment StartX=-8.5 StartY=-76.5 StartZ=0 EndX=-8.5 EndY=-83.5 EndZ=0
    g8: LineSegment StartX=-8.5 StartY=-83.5 StartZ=0 EndX=0 EndY=-83.5 EndZ=0
    g9: LineSegment StartX=0 StartY=-83.5 StartZ=0 EndX=0 EndY=-102 EndZ=0
    g10: LineSegment StartX=-42 StartY=-102 StartZ=0 EndX=0 EndY=-102 EndZ=0
    g11: Circle CenterX=9.55 CenterY=-110.25 CenterZ=0 NormalX=0 NormalY=0 NormalZ=1 AngleXU=0 Radius=3.25
    g12: Circle CenterX=9.55 CenterY=-135.25 CenterZ=0 NormalX=0 NormalY=0 NormalZ=1 AngleXU=0 Radius=3.25
    g13: Circle CenterX=-34.45 CenterY=-135.25 CenterZ=0 NormalX=0 NormalY=0 NormalZ=1 AngleXU=0 Radius=3.25
    g14: Circle CenterX=-34.45 CenterY=-110.25 CenterZ=0 NormalX=0 NormalY=0 NormalZ=1 AngleXU=0 Radius=3.25
    g15: LineSegment StartX=16.53 StartY=-53.5 StartZ=0 EndX=3.53 EndY=-53.5 EndZ=0
    g16: LineSegment StartX=3.53 StartY=-53.5 StartZ=0 EndX=3.53 EndY=-76.5 EndZ=0
    g17: LineSegment StartX=3.53 StartY=-76.5 StartZ=0 EndX=-8.5 EndY=-76.5 EndZ=0
  constraints (54):
    c: Vertical(g0)
    c: Vertical(g1)
    c: Coincident(g2,g1)
    c: Horizontal(g2)
    c: Coincident(g3,g2)
    c: Vertical(g3)
    c: Coincident(g4,g3)
    c: Horizontal(g4)
    c: Vertical(g5)
    c: Coincident(g6,g5)
    c: Coincident(g6,g0)
    c: Horizontal(g6)
    c: Vertical(g7)
    c: Coincident(g8,g7)
    c: Horizontal(g8)
    c: Coincident(g9,g8)
    c: PointOnObject(g9,g-2)
    c: Vertical(g9)
    c: Coincident(g10,g1)
    c: Coincident(g10,g9)
    c: Horizontal(g10)
    c: Distance(g0,g-1) = 147
    c: Coincident(g4,g5)
    c: Distance(g2,g-1) = 147
    c: Distance(g6) = 14
    c: Distance(g0) = 93.5
    c: Distance(g7) = 7
    c: Distance(g8) = 8.5
    c: Distance(g9) = 18.5
    c: Distance(g5) = 30
    c: Distance(g4) = 30
    c: Distance(g10) = 42
    c: Diameter(g14) = 6.5
    c: Distance(g14,g-1) = 110.25
    c: Distance(g14,g-2) = 34.45
    c: Distance(g13,g-2) = 34.45
    c: Distance(g13,g-1) = 135.25
    c: Diameter(g13) = 6.5
    c: Distance(g11,g-2) = 9.55
    c: Distance(g11,g-1) = 110.25
    c: Distance(g12,g-1) = 135.25
    c: Distance(g12,g-2) = 9.55
    c: Diameter(g11) = 6.5
    c: Diameter(g12) = 6.5
    c: Coincident(g15,g0)
    c: Horizontal(g15)
    c: Coincident(g16,g15)
    c: Vertical(g16)
    c: Coincident(g17,g16)
    c: Coincident(g17,g7)
    c: Horizontal(g17)
    c: Distance(g15) = 13
    c: Distance(g17) = 12.03
    c: Distance(g16) = 23
FEATURE [Part::Extrusion] Extrude016
  Base = -> Sketch016
  Dir = (0,1,0)
  DirMode = 2
  FaceMakerClass = Part::FaceMakerBullseye
  LengthFwd = 10
  LengthRev = 0
  Placement = pos=(0,-46,0) rot=(0,0,1;0rad)
  Reversed = true
  Solid = true
  Symmetric = false
FEATURE [Part::Box] Box230  label="Cube230"
  AttacherType = Attacher::AttachEngine3D
  Height = 10
  Length = 10
  Placement = pos=(27.5,-21,-114.5) rot=(0,0,1;0rad)
  Width = 23
FEATURE [Sketcher::SketchObject] Sketch017
  FullyConstrained = true
  Placement = pos=(0,0,0) rot=(0,0.707107,0.707107;3.14159rad)
  sketch-geometry (16):
    g0: LineSegment StartX=-80.36 StartY=-110.5 StartZ=0 EndX=-68.5 EndY=-110.5 EndZ=0
    g1: LineSegment StartX=-68.5 StartY=-110.5 StartZ=0 EndX=-68.5 EndY=-114.5 EndZ=0
    g2: LineSegment StartX=-68.5 StartY=-114.5 StartZ=0 EndX=-76.36 EndY=-114.5 EndZ=0
    g3: LineSegment StartX=-76.36 StartY=-114.5 StartZ=0 EndX=-76.36 EndY=-127.5 EndZ=0
    g4: LineSegment StartX=-80.36 StartY=-131.5 StartZ=0 EndX=-80.36 EndY=-110.5 EndZ=0
    g5: LineSegment StartX=-76.36 StartY=-127.5 StartZ=0 EndX=-68.56 EndY=-127.5 EndZ=0
    g6: LineSegment StartX=-68.56 StartY=-127.5 StartZ=0 EndX=-68.56 EndY=-131.5 EndZ=0
    g7: LineSegment StartX=-68.56 StartY=-131.5 StartZ=0 EndX=-80.36 EndY=-131.5 EndZ=0
    g8: LineSegment StartX=-36.5 StartY=-127.5 StartZ=0 EndX=-36.5 EndY=-131.5 EndZ=0
    g9: LineSegment StartX=-36.5 StartY=-131.5 StartZ=0 EndX=-23.5 EndY=-131.5 EndZ=0
    g10: LineSegment StartX=-23.5 StartY=-131.5 StartZ=0 EndX=-23.5 EndY=-110.5 EndZ=0
    g11: LineSegment StartX=-27.5 StartY=-114.5 StartZ=0 EndX=-27.5 EndY=-127.5 EndZ=0
    g12: LineSegment StartX=-27.5 StartY=-127.5 StartZ=0 EndX=-36.5 EndY=-127.5 EndZ=0
    g13: LineSegment StartX=-27.5 StartY=-114.5 StartZ=0 EndX=-36.5 EndY=-114.5 EndZ=0
    g14: LineSegment StartX=-36.5 StartY=-114.5 StartZ=0 EndX=-36.5 EndY=-110.5 EndZ=0
    g15: LineSegment StartX=-36.5 StartY=-110.5 StartZ=0 EndX=-23.5 EndY=-110.5 EndZ=0
  constraints (48):
    c: Horizontal(g0)
    c: Coincident(g1,g0)
    c: Coincident(g2,g1)
    c: Horizontal(g2)
    c: Vertical(g3)
    c: Coincident(g4,g0)
    c: Vertical(g4)
    c: Vertical(g1)
    c: Distance(g1) = 4
    c: Coincident(g2,g3)
    c: Coincident(g5,g3)
    c: Horizontal(g5)
    c: Coincident(g6,g5)
    c: Vertical(g6)
    c: Coincident(g7,g6)
    c: Coincident(g7,g4)
    c: Horizontal(g7)
    c: Distance(g6) = 4
    c: Distance(g0,g-1) = 110.5
    c: Distance(g4) = 21
    c: Distance(g2) = 7.86
    c: Distance(g5) = 7.8
    c: Distance(g2,g4) = 4
    c: Distance(g5,g-2) = 68.56
    c: Vertical(g8)
    c: Coincident(g9,g8)
    c: Horizontal(g9)
    c: Coincident(g10,g9)
    c: Vertical(g10)
    c: Vertical(g11)
    c: Coincident(g12,g11)
    c: Coincident(g12,g8)
    c: Horizontal(g12)
    c: Distance(g12) = 9
    c: Distance(g9,g-1) = 131.5
    c: Distance(g8) = 4
    c: Distance(g11,g-2) = 27.5
    c: Coincident(g13,g11)
    c: Horizontal(g13)
    c: Coincident(g14,g13)
    c: Vertical(g14)
    c: Coincident(g15,g14)
    c: Horizontal(g15)
    c: Coincident(g15,g10)
    c: Distance(g14) = 4
    c: Distance(g11,g10) = 4
    c: Distance(g14,g-1) = 110.5
    c: Distance(g13) = 9
FEATURE [Part::Extrusion] Extrude017
  Base = -> Sketch017
  Dir = (0,1,0)
  DirMode = 2
  FaceMakerClass = Part::FaceMakerBullseye
  LengthFwd = 45.5
  LengthRev = 0
  Placement = pos=(0,2,0) rot=(0,0,1;0rad)
  Reversed = true
  Solid = true
  Symmetric = false
FEATURE [Part::Cut] Cut019
  Base = -> Extrude017
  Placement = pos=(-40,-58,74) rot=(0,0,1;0rad)
  Tool = -> Box230
FEATURE [Part::Box] Box231  label="Cube231"
  AttacherType = Attacher::AttachEngine3D
  Height = 70
  Length = 12
  Placement = pos=(12,-148.5,-147) rot=(0,0,1;0rad)
  Width = 15
FEATURE [Part::Box] Box232  label="Cube232"
  AttacherType = Attacher::AttachEngine3D
  Height = 70
  Length = 14
  Placement = pos=(31,-148.5,-147) rot=(0,0,1;0rad)
  Width = 15
FEATURE [Part::Box] Box233  label="Cube233"
  AttacherType = Attacher::AttachEngine3D
  Height = 46
  Length = 10
  Placement = pos=(35,-87.5,-87) rot=(1,0,0;1.5708rad)
  Width = 10
FEATURE [Part::Box] Box234  label="Cube234"
  AttacherType = Attacher::AttachEngine3D
  Height = 25
  Length = 10
  Placement = pos=(93,-56,-87) rot=(1,0,0;1.5708rad)
  Width = 10
FEATURE [Part::Box] Box235  label="Cube235"
  AttacherType = Attacher::AttachEngine3D
  Height = 25
  Length = 10
  Placement = pos=(72.25,-56,-87) rot=(1,0,0;1.5708rad)
  Width = 10
FEATURE [Part::Box] Box236  label="Cube236"
  AttacherType = Attacher::AttachEngine3D
  Height = 25
  Length = 10
  Placement = pos=(50.25,-56,-87) rot=(1,0,0;1.5708rad)
  Width = 10
FEATURE [Part::MultiFuse] Fusion134
  Placement = pos=(0,0,-70) rot=(0,0,1;0rad)
  Shapes = -> [Box234,Box235,Box236]
FEATURE [Part::Box] Box237  label="Cube237"
  AttacherType = Attacher::AttachEngine3D
  Height = 6
  Length = 10
  Placement = pos=(93,-74,-87) rot=(1,0,0;1.5708rad)
  Width = 15
FEATURE [Part::Box] Box238  label="Cube238"
  AttacherType = Attacher::AttachEngine3D
  Height = 6
  Length = 10
  Placement = pos=(72.25,-74,-87) rot=(1,0,0;1.5708rad)
  Width = 53
FEATURE [Part::Box] Box239  label="Cube239"
  AttacherType = Attacher::AttachEngine3D
  Height = 6
  Length = 10
  Placement = pos=(50.25,-74,-87) rot=(1,0,0;1.5708rad)
  Width = 15
FEATURE [Part::MultiFuse] Fusion135
  Placement = pos=(0,-1,-60) rot=(0,0,1;0rad)
  Shapes = -> [Box237,Box238,Box239]
FEATURE [Part::MultiFuse] Fusion136
  Shapes = -> [Fusion134,Fusion135]
FEATURE [Part::Box] Box240  label="Cube240"
  AttacherType = Attacher::AttachEngine3D
  Height = 10
  Length = 61.5
  Placement = pos=(-16.5,-111.5,-57.5) rot=(0,0,1;0rad)
  Width = 10
FEATURE [Part::MultiFuse] Fusion137
  Shapes = -> [Extrude015,Extrude016,Cut019,Box231,Box232,Box233,Fusion136,Box240]
FEATURE [Part::Box] Box241  label="Cube241"
  AttacherType = Attacher::AttachEngine3D
  Height = 19.5
  Length = 10
  Placement = pos=(35,-111.5,-77) rot=(0,0,1;0rad)
  Width = 10
FEATURE [Part::Cylinder] Cylinder109  label="ips_screw1"
  Angle = 360
  AttacherType = Attacher::AttachEngine3D
  FirstAngle = 0
  Height = 20
  Placement = pos=(2.7,-51.2,-90) rot=(0,0,1;0rad)
  Radius = 1.125
  SecondAngle = 0
FEATURE [Part::Cylinder] Cylinder110  label="ips_screw_2"
  Angle = 360
  AttacherType = Attacher::AttachEngine3D
  FirstAngle = 0
  Height = 80
  Placement = pos=(39.96,-91.55,-90) rot=(0,0,1;0rad)
  Radius = 1.25
  SecondAngle = 0
FEATURE [Part::MultiFuse] Fusion138  label="Pre_ips_hole_cut"
  Shapes = -> [Fusion137,Box241]
FEATURE [Part::Cut] Cut020
  Base = -> Fusion138
  Tool = -> Cylinder110
FEATURE [Part::Cut] Cut021
  Base = -> Cut020
  Tool = -> Cylinder109
FEATURE [Part::Cylinder] Cylinder111
  Angle = 360
  AttacherType = Attacher::AttachEngine3D
  FirstAngle = 0
  Height = 20
  Placement = pos=(77.25,-79,-99.75) rot=(-1,0,0;1.5708rad)
  Radius = 1.75
  SecondAngle = 0
FEATURE [Part::Cylinder] Cylinder112
  Angle = 360
  AttacherType = Attacher::AttachEngine3D
  FirstAngle = 0
  Height = 20
  Placement = pos=(98.9,-79,-137.1) rot=(-1,0,0;1.5708rad)
  Radius = 1.75
  SecondAngle = 0
FEATURE [Part::Cylinder] Cylinder113
  Angle = 360
  AttacherType = Attacher::AttachEngine3D
  FirstAngle = 0
  Height = 20
  Placement = pos=(55.7,-79,-137.25) rot=(-1,0,0;1.5708rad)
  Radius = 1.75
  SecondAngle = 0
FEATURE [Part::MultiFuse] Fusion139
  Placement = pos=(0,-7,0) rot=(0,0,1;0rad)
  Shapes = -> [Cylinder111,Cylinder112,Cylinder113]
FEATURE [Part::Cut] Cut022
  Base = -> Cut021
  Tool = -> Fusion139
FEATURE [Part::Cylinder] Cylinder114
  Angle = 360
  AttacherType = Attacher::AttachEngine3D
  FirstAngle = 0
  Height = 10
  Placement = pos=(17.55,-141,0) rot=(0,0,1;0rad)
  Radius = 1.45
  SecondAngle = 0
FEATURE [Part::Cylinder] Cylinder115
  Angle = 360
  AttacherType = Attacher::AttachEngine3D
  FirstAngle = 0
  Height = 10
  Placement = pos=(37.85,-141,0) rot=(0,0,1;0rad)
  Radius = 1.45
  SecondAngle = 0
FEATURE [Part::MultiFuse] Fusion140
  Placement = pos=(0,0,-82) rot=(0,0,1;0rad)
  Shapes = -> [Cylinder114,Cylinder115]
FEATURE [Part::Cut] Cut023  label="cut"
  Base = -> Cut022
  Tool = -> Fusion140
FEATURE [Part::Box] Box242  label="Cube242"
  AttacherType = Attacher::AttachEngine3D
  Height = 11
  Length = 4
  Placement = pos=(36.36,-111.5,-47.5) rot=(0,0,1;0rad)
  Width = 10
FEATURE [Part::Box] Box243  label="Cube243"
  AttacherType = Attacher::AttachEngine3D
  Height = 17
  Length = 4
  Placement = pos=(-16.53,-56,-53.5) rot=(0,0,1;0rad)
  Width = 10
FEATURE [Part::MultiFuse] Fusion141  label="New_sensor_hold"
  Shapes = -> [Cut023,Box242,Box243]
FEATURE [Part::Fillet] Fillet013  label="4mm_fillet_edges"
  Base = -> Fusion141
  Edges = 46 edges r=4: [Edge26,Edge58,Edge61,Edge104,Edge170,Edge173,Edge174,Edge175,Edge180,Edge182,Edge186,Edge187,Edge188,Edge189,Edge190,Edge191,Edge197,Edge203,Edge205,Edge210,Edge211,Edge317,Edge321,Edge322,Edge323,Edge329,Edge330,Edge332,Edge334,Edge335,Edge337,Edge339,Edge340,Edge341,Edge344,Edge345,Edge347,+9 more]
